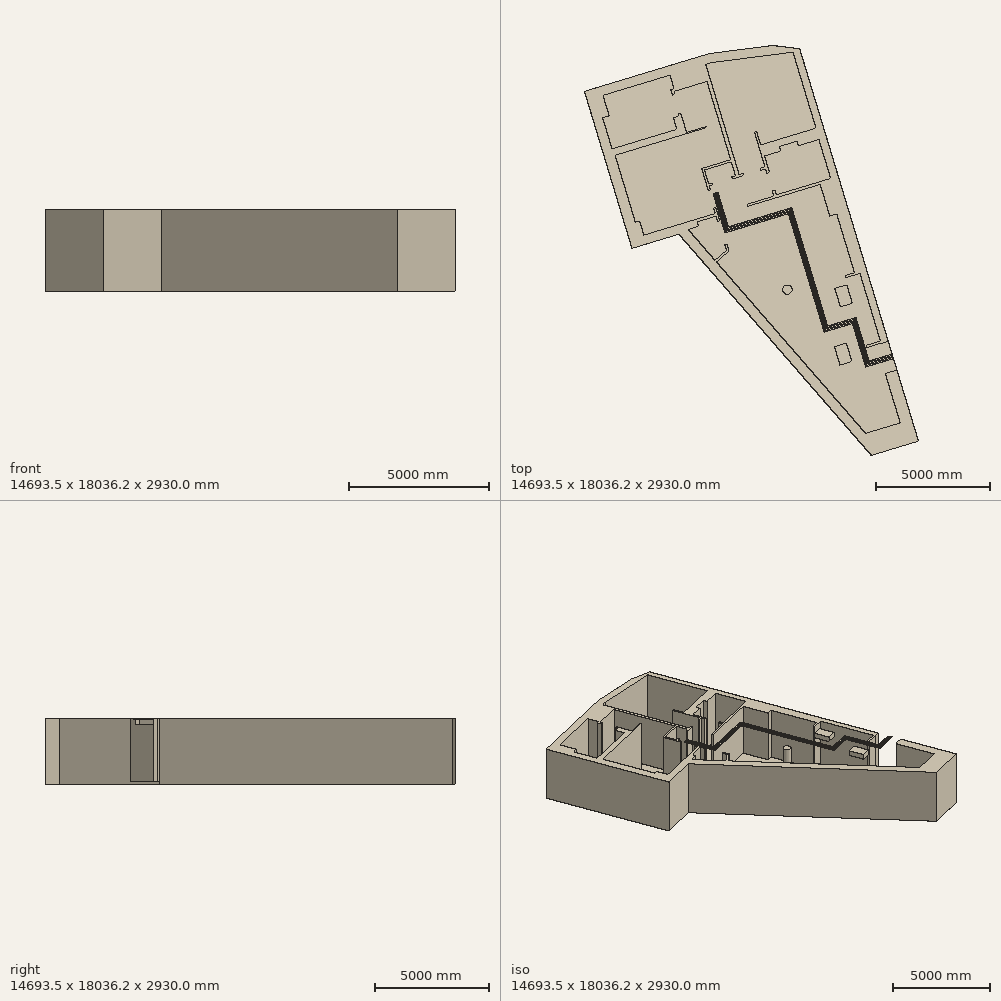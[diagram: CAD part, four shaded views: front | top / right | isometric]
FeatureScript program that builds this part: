
annotation { "Feature Type Name" : "Feature", "Feature Type Description" : "" }
export const myFeature = defineFeature(function(context is Context, id is Id, definition is map)
    precondition{}
    {
        {
            var Q0;
            Q0=qCreatedBy(makeId("Top.planeOp"),FACE);
            var sketch = newSketch(context, id + "F0", { "sketchPlane" : qUnion([Q0])});
            skLineSegment(sketch, "E0", {"start": v(688.47, 32038.93) * mm, "end": v(503.96, 32648.57) * mm});
            skLineSegment(sketch, "E1", {"start": v(503.96, 32648.57) * mm, "end": v(1685.98, 33006.34) * mm});
            skLineSegment(sketch, "E2", {"start": v(1685.98, 33006.34) * mm, "end": v(1870.5, 32396.71) * mm});
            skLineSegment(sketch, "E3", {"start": v(1870.5, 32396.71) * mm, "end": v(688.47, 32038.93) * mm});
            skLineSegment(sketch, "E4", {"start": v(975.28, 28670.43) * mm, "end": v(-209.3, 30031.2) * mm});
            skLineSegment(sketch, "E5", {"start": v(-209.3, 30031.2) * mm, "end": v(247, 30169.35) * mm});
            skLineSegment(sketch, "E6", {"start": v(247, 30169.35) * mm, "end": v(187.3, 30366.58) * mm});
            skLineSegment(sketch, "E7", {"start": v(187.3, 30366.58) * mm, "end": v(1017.23, 30617.78) * mm});
            skLineSegment(sketch, "E8", {"start": v(1017.23, 30617.78) * mm, "end": v(1474.96, 29105.4) * mm});
            skLineSegment(sketch, "E9", {"start": v(1474.96, 29105.4) * mm, "end": v(975.28, 28670.43) * mm});
            skLineSegment(sketch, "E10", {"start": v(2976.11, 33751) * mm, "end": v(2796.5, 34344.43) * mm});
            skLineSegment(sketch, "E11", {"start": v(2796.5, 34344.43) * mm, "end": v(5232.35, 35081.71) * mm});
            skLineSegment(sketch, "E12", {"start": v(5232.35, 35081.71) * mm, "end": v(5411.97, 34488.28) * mm});
            skLineSegment(sketch, "E13", {"start": v(5411.97, 34488.28) * mm, "end": v(2976.11, 33751) * mm});
            skLineSegment(sketch, "E14", {"start": v(1038.97, 28597.26) * mm, "end": v(1585.97, 29073.44) * mm});
            skLineSegment(sketch, "E15", {"start": v(1585.97, 29073.44) * mm, "end": v(1107.2, 30655.36) * mm});
            skLineSegment(sketch, "E16", {"start": v(1107.2, 30655.36) * mm, "end": v(5663.61, 32034.54) * mm});
            skLineSegment(sketch, "E17", {"start": v(5663.61, 32034.54) * mm, "end": v(6064.95, 30708.6) * mm});
            skLineSegment(sketch, "E18", {"start": v(6064.95, 30708.6) * mm, "end": v(6370.27, 30801.02) * mm});
            skLineSegment(sketch, "E19", {"start": v(6370.27, 30801.02) * mm, "end": v(7173.28, 28148.02) * mm});
            skLineSegment(sketch, "E20", {"start": v(7173.28, 28148.02) * mm, "end": v(2627.74, 26772.17) * mm});
            skLineSegment(sketch, "E21", {"start": v(2627.74, 26772.17) * mm, "end": v(1038.97, 28597.26) * mm});
            skLineSegment(sketch, "E22", {"start": v(7648.03, 21005.12) * mm, "end": v(9204.22, 21476.13) * mm});
            skLineSegment(sketch, "E23", {"start": v(9204.22, 21476.13) * mm, "end": v(8546.54, 23648.8) * mm});
            skLineSegment(sketch, "E24", {"start": v(8546.54, 23648.8) * mm, "end": v(8680.59, 23689.38) * mm});
            skLineSegment(sketch, "E25", {"start": v(8680.59, 23689.38) * mm, "end": v(8275.24, 25028.58) * mm});
            skLineSegment(sketch, "E26", {"start": v(8275.24, 25028.58) * mm, "end": v(7643.52, 24837.37) * mm});
            skLineSegment(sketch, "E27", {"start": v(7643.52, 24837.37) * mm, "end": v(7615.16, 24931.08) * mm});
            skLineSegment(sketch, "E28", {"start": v(7615.16, 24931.08) * mm, "end": v(8246.85, 25122.28) * mm});
            skLineSegment(sketch, "E29", {"start": v(8246.85, 25122.28) * mm, "end": v(7345.9, 28098.92) * mm});
            skLineSegment(sketch, "E30", {"start": v(7345.9, 28098.92) * mm, "end": v(6714.19, 27907.71) * mm});
            skLineSegment(sketch, "E31", {"start": v(6714.19, 27907.71) * mm, "end": v(6686.09, 28000.55) * mm});
            skLineSegment(sketch, "E32", {"start": v(6686.09, 28000.55) * mm, "end": v(2627.74, 26772.17) * mm});
            skLineSegment(sketch, "E33", {"start": v(2627.74, 26772.17) * mm, "end": v(7648.03, 21005.12) * mm});
            skLineSegment(sketch, "E34", {"start": v(1953.77, 32421.91) * mm, "end": v(484.9, 37274.77) * mm});
            skLineSegment(sketch, "E35", {"start": v(484.9, 37274.77) * mm, "end": v(817.35, 37375.45) * mm});
            skLineSegment(sketch, "E36", {"start": v(817.35, 37375.45) * mm, "end": v(4399.01, 37834.91) * mm});
            skLineSegment(sketch, "E37", {"start": v(4399.01, 37834.91) * mm, "end": v(5232.35, 35081.71) * mm});
            skLineSegment(sketch, "E38", {"start": v(5232.35, 35081.71) * mm, "end": v(2703.65, 34316.33) * mm});
            skLineSegment(sketch, "E39", {"start": v(2703.65, 34316.33) * mm, "end": v(3166, 32788.83) * mm});
            skLineSegment(sketch, "E40", {"start": v(3166, 32788.83) * mm, "end": v(1953.77, 32421.91) * mm});
            skLineSegment(sketch, "E41", {"start": v(-3492.5, 33275.5) * mm, "end": v(592.96, 34511.99) * mm});
            skLineSegment(sketch, "E42", {"start": v(592.96, 34511.99) * mm, "end": v(1074.07, 32922.48) * mm});
            skLineSegment(sketch, "E43", {"start": v(1074.07, 32922.48) * mm, "end": v(383.02, 32713.3) * mm});
            skLineSegment(sketch, "E44", {"start": v(383.02, 32713.3) * mm, "end": v(981.9, 30734.55) * mm});
            skLineSegment(sketch, "E45", {"start": v(981.9, 30734.55) * mm, "end": v(-2157.46, 29784.33) * mm});
            skLineSegment(sketch, "E46", {"start": v(-2157.46, 29784.33) * mm, "end": v(-2347.02, 30410.5) * mm});
            skLineSegment(sketch, "E47", {"start": v(-2347.02, 30410.5) * mm, "end": v(-2601.66, 30332.35) * mm});
            skLineSegment(sketch, "E48", {"start": v(-2601.66, 30332.35) * mm, "end": v(-3492.5, 33275.5) * mm});
            skLineSegment(sketch, "E49", {"start": v(-710, 34438.17) * mm, "end": v(-3559.9, 33575.84) * mm});
            skLineSegment(sketch, "E50", {"start": v(-3559.9, 33575.84) * mm, "end": v(-3973.74, 34943.1) * mm});
            skLineSegment(sketch, "E51", {"start": v(-3973.74, 34943.1) * mm, "end": v(-3685.65, 35030.3) * mm});
            skLineSegment(sketch, "E52", {"start": v(-3685.65, 35030.3) * mm, "end": v(-3957.95, 35930) * mm});
            skLineSegment(sketch, "E53", {"start": v(-3957.95, 35930) * mm, "end": v(-1009.44, 36822.46) * mm});
            skLineSegment(sketch, "E54", {"start": v(-1009.44, 36822.46) * mm, "end": v(-831.43, 36230.92) * mm});
            skLineSegment(sketch, "E55", {"start": v(-831.43, 36230.92) * mm, "end": v(-977.95, 36186.57) * mm});
            skLineSegment(sketch, "E56", {"start": v(-977.95, 36186.57) * mm, "end": v(-622.8, 35013.09) * mm});
            skLineSegment(sketch, "E57", {"start": v(-622.8, 35013.09) * mm, "end": v(-861.8, 34940.5) * mm});
            skLineSegment(sketch, "E58", {"start": v(-861.8, 34940.5) * mm, "end": v(-710, 34438.17) * mm});
            skLineSegment(sketch, "E59", {"start": v(1107.2, 30655.36) * mm, "end": v(2396.47, 31045.6) * mm});
            skLineSegment(sketch, "E60", {"start": v(2396.47, 31045.6) * mm, "end": v(2368.65, 31137.53) * mm});
            skLineSegment(sketch, "E61", {"start": v(2368.65, 31137.53) * mm, "end": v(3556.94, 31497.2) * mm});
            skLineSegment(sketch, "E62", {"start": v(3556.94, 31497.2) * mm, "end": v(3194.1, 32695.99) * mm});
            skLineSegment(sketch, "E63", {"start": v(3194.1, 32695.99) * mm, "end": v(716.57, 31946.1) * mm});
            skLineSegment(sketch, "E64", {"start": v(716.57, 31946.1) * mm, "end": v(1107.2, 30655.36) * mm});
            skLineSegment(sketch, "E65", {"start": v(-828.96, 36106.8) * mm, "end": v(-267.45, 34251.56) * mm});
            skLineSegment(sketch, "E66", {"start": v(-267.45, 34251.56) * mm, "end": v(583.39, 34509.09) * mm});
            skLineSegment(sketch, "E67", {"start": v(583.39, 34509.09) * mm, "end": v(1064.5, 32919.58) * mm});
            skLineSegment(sketch, "E68", {"start": v(1064.5, 32919.58) * mm, "end": v(1657.88, 33099.18) * mm});
            skLineSegment(sketch, "E69", {"start": v(1657.88, 33099.18) * mm, "end": v(615.22, 36543.93) * mm});
            skLineSegment(sketch, "E70", {"start": v(615.22, 36543.93) * mm, "end": v(-828.96, 36106.8) * mm});
            skLineSegment(sketch, "E71", {"start": v(2521, 36867.94) * mm, "end": v(2477.55, 37011.51) * mm});
            skLineSegment(sketch, "E72", {"start": v(2477.55, 37011.51) * mm, "end": v(2621.12, 37054.97) * mm});
            skLineSegment(sketch, "E73", {"start": v(2621.12, 37054.97) * mm, "end": v(2664.57, 36911.4) * mm});
            skLineSegment(sketch, "E74", {"start": v(2664.57, 36911.4) * mm, "end": v(2521, 36867.94) * mm});
            skCircle(sketch, "E75", {"center": v(2571.06, 36961.45) * mm, "radius": 75 * mm});
            skLineSegment(sketch, "E76", {"start": v(6682.01, 27897.97) * mm, "end": v(2720.36, 26698.86) * mm});
            skLineSegment(sketch, "E77", {"start": v(2845.75, 34181.7) * mm, "end": v(5281.61, 34918.98) * mm});
            skLineSegment(sketch, "E78", {"start": v(6128.04, 25871.52) * mm, "end": v(6340.42, 26268.26) * mm});
            skCircle(sketch, "E79", {"center": v(6234.23, 26069.9) * mm, "radius": 225 * mm});
            skCircle(sketch, "E80", {"center": v(-1847.03, 34397.83) * mm, "radius": 70 * mm});
            skCircle(sketch, "E81", {"center": v(-1031.48, 34644.68) * mm, "radius": 70 * mm});
            skCircle(sketch, "E82", {"center": v(-2662.4, 34151.03) * mm, "radius": 70 * mm});
            skCircle(sketch, "E83", {"center": v(-3282.71, 33963.28) * mm, "radius": 70 * mm});
            skCircle(sketch, "E84", {"center": v(1346.97, 36590.95) * mm, "radius": 70 * mm});
            skCircle(sketch, "E85", {"center": v(1919, 34705.78) * mm, "radius": 70 * mm});
            skCircle(sketch, "E86", {"center": v(4106.18, 35367.8) * mm, "radius": 70 * mm});
            skCircle(sketch, "E87", {"center": v(4291.3, 37482.1) * mm, "radius": 24.96 * mm});
            skCircle(sketch, "E88", {"center": v(4291.3, 37482.1) * mm, "radius": 89.6 * mm});
            skCircle(sketch, "E89", {"center": v(3702.85, 29215.68) * mm, "radius": 50 * mm});
            skLineSegment(sketch, "E90", {"start": v(3774.64, 29237.4) * mm, "end": v(3631.07, 29193.95) * mm});
            skLineSegment(sketch, "E91", {"start": v(3681.12, 29287.46) * mm, "end": v(3724.58, 29143.9) * mm});
            skLineSegment(sketch, "E92", {"start": v(4947.02, 28251.96) * mm, "end": v(4903.56, 28395.53) * mm});
            skLineSegment(sketch, "E93", {"start": v(4903.56, 28395.53) * mm, "end": v(5047.13, 28438.98) * mm});
            skLineSegment(sketch, "E94", {"start": v(5047.13, 28438.98) * mm, "end": v(5090.59, 28295.41) * mm});
            skLineSegment(sketch, "E95", {"start": v(5090.59, 28295.41) * mm, "end": v(4947.02, 28251.96) * mm});
            skCircle(sketch, "E96", {"center": v(4997.08, 28345.47) * mm, "radius": 75 * mm});
            skCircle(sketch, "E97", {"center": v(4647.16, 29501.5) * mm, "radius": 50 * mm});
            skCircle(sketch, "E98", {"center": v(4647.16, 29501.5) * mm, "radius": 185.02 * mm});
            skCircle(sketch, "E99", {"center": v(5731.95, 25917.86) * mm, "radius": 50 * mm});
            skCircle(sketch, "E100", {"center": v(5731.95, 25917.86) * mm, "radius": 185.02 * mm});
            skCircle(sketch, "E101", {"center": v(-1220.67, 35372.03) * mm, "radius": 23.22 * mm});
            skCircle(sketch, "E102", {"center": v(-3689, 35802.45) * mm, "radius": 52 * mm});
            skCircle(sketch, "E103", {"center": v(2856.43, 36018.65) * mm, "radius": 50 * mm});
            skLineSegment(sketch, "E104", {"start": v(2928.21, 36040.38) * mm, "end": v(2784.64, 35996.93) * mm});
            skLineSegment(sketch, "E105", {"start": v(2834.7, 36090.44) * mm, "end": v(2878.16, 35946.87) * mm});
            skCircle(sketch, "E106", {"center": v(2789.14, 31831.37) * mm, "radius": 70 * mm});
            skCircle(sketch, "E107", {"center": v(2325.79, 33360.78) * mm, "radius": 70 * mm});
            skCircle(sketch, "E108", {"center": v(-3089.6, 33189.85) * mm, "radius": 24.96 * mm});
            skCircle(sketch, "E109", {"center": v(-3089.61, 33189.85) * mm, "radius": 89.6 * mm});
            skCircle(sketch, "E110", {"center": v(-694.3, 33908.01) * mm, "radius": 24.96 * mm});
            skCircle(sketch, "E111", {"center": v(-694.3, 33908.01) * mm, "radius": 89.6 * mm});
            skCircle(sketch, "E112", {"center": v(5238.28, 31100.14) * mm, "radius": 70 * mm});
            skCircle(sketch, "E113", {"center": v(-2823.66, 32311.65) * mm, "radius": 70 * mm});
            skLineSegment(sketch, "E114", {"start": v(-1847.07, 31588.32) * mm, "end": v(-1803.62, 31444.75) * mm});
            skLineSegment(sketch, "E115", {"start": v(-1803.62, 31444.75) * mm, "end": v(-1947.18, 31401.3) * mm});
            skLineSegment(sketch, "E116", {"start": v(-1947.18, 31401.3) * mm, "end": v(-1990.64, 31544.87) * mm});
            skLineSegment(sketch, "E117", {"start": v(-1990.64, 31544.87) * mm, "end": v(-1847.07, 31588.32) * mm});
            skCircle(sketch, "E118", {"center": v(-1897.13, 31494.81) * mm, "radius": 75 * mm});
            skLineSegment(sketch, "E119", {"start": v(-798.77, 31748.9) * mm, "end": v(-842.22, 31892.47) * mm});
            skLineSegment(sketch, "E120", {"start": v(-842.22, 31892.47) * mm, "end": v(-698.66, 31935.92) * mm});
            skLineSegment(sketch, "E121", {"start": v(-698.66, 31935.92) * mm, "end": v(-655.2, 31792.36) * mm});
            skLineSegment(sketch, "E122", {"start": v(-655.2, 31792.36) * mm, "end": v(-798.77, 31748.9) * mm});
            skCircle(sketch, "E123", {"center": v(-748.71, 31842.41) * mm, "radius": 75 * mm});
            skCircle(sketch, "E124", {"center": v(-1322.96, 31668.6) * mm, "radius": 50 * mm});
            skLineSegment(sketch, "E125", {"start": v(-1251.18, 31690.33) * mm, "end": v(-1394.75, 31646.87) * mm});
            skLineSegment(sketch, "E126", {"start": v(-1344.7, 31740.38) * mm, "end": v(-1301.24, 31596.82) * mm});
            skCircle(sketch, "E127", {"center": v(1916.85, 30094.8) * mm, "radius": 70 * mm});
            skLineSegment(sketch, "E128", {"start": v(5408.3, 27246.02) * mm, "end": v(5451.75, 27102.45) * mm});
            skLineSegment(sketch, "E129", {"start": v(5451.75, 27102.45) * mm, "end": v(5308.19, 27059) * mm});
            skLineSegment(sketch, "E130", {"start": v(5308.19, 27059) * mm, "end": v(5264.73, 27202.57) * mm});
            skLineSegment(sketch, "E131", {"start": v(5264.73, 27202.57) * mm, "end": v(5408.3, 27246.02) * mm});
            skCircle(sketch, "E132", {"center": v(5358.24, 27152.51) * mm, "radius": 75 * mm});
            skCircle(sketch, "E133", {"center": v(7896.13, 22311.4) * mm, "radius": 50 * mm});
            skLineSegment(sketch, "E134", {"start": v(7967.91, 22333.12) * mm, "end": v(7824.34, 22289.67) * mm});
            skLineSegment(sketch, "E135", {"start": v(7874.4, 22383.18) * mm, "end": v(7917.86, 22239.6) * mm});
            skLineSegment(sketch, "E136", {"start": v(7346.13, 23869.61) * mm, "end": v(7302.67, 24013.18) * mm});
            skLineSegment(sketch, "E137", {"start": v(7302.67, 24013.18) * mm, "end": v(7446.24, 24056.63) * mm});
            skLineSegment(sketch, "E138", {"start": v(7446.24, 24056.63) * mm, "end": v(7489.7, 23913.07) * mm});
            skLineSegment(sketch, "E139", {"start": v(7489.7, 23913.07) * mm, "end": v(7346.13, 23869.61) * mm});
            skCircle(sketch, "E140", {"center": v(7396.18, 23963.12) * mm, "radius": 75 * mm});
            skCircle(sketch, "E141", {"center": v(7193.06, 26360.11) * mm, "radius": 50 * mm});
            skLineSegment(sketch, "E142", {"start": v(7240.92, 26374.6) * mm, "end": v(7514.25, 26457.33) * mm});
            skLineSegment(sketch, "E143", {"start": v(7365.6, 26307.86) * mm, "end": v(7240.92, 26374.6) * mm});
            skLineSegment(sketch, "E144", {"start": v(7240.92, 26374.6) * mm, "end": v(7307.66, 26499.27) * mm});
            skLineSegment(sketch, "E145", {"start": v(7307.66, 26499.27) * mm, "end": v(7365.6, 26307.86) * mm});
            skLineSegment(sketch, "E146", {"start": v(575.66, 33236.57) * mm, "end": v(546.8, 33331.8) * mm});
            skLineSegment(sketch, "E147", {"start": v(546.8, 33331.8) * mm, "end": v(655.88, 33364.87) * mm});
            skLineSegment(sketch, "E148", {"start": v(655.88, 33364.87) * mm, "end": v(684.75, 33269.65) * mm});
            skLineSegment(sketch, "E149", {"start": v(684.75, 33269.65) * mm, "end": v(575.66, 33236.57) * mm});
            skLineSegment(sketch, "E150", {"start": v(546.79, 33331.8) * mm, "end": v(517.92, 33427.01) * mm});
            skLineSegment(sketch, "E151", {"start": v(517.92, 33427.01) * mm, "end": v(627.01, 33460.09) * mm});
            skLineSegment(sketch, "E152", {"start": v(627.01, 33460.09) * mm, "end": v(655.88, 33364.87) * mm});
            skLineSegment(sketch, "E153", {"start": v(655.88, 33364.87) * mm, "end": v(546.79, 33331.8) * mm});
            skLineSegment(sketch, "E154", {"start": v(3585.52, 37346.87) * mm, "end": v(3628.97, 37203.3) * mm});
            skLineSegment(sketch, "E155", {"start": v(3628.97, 37203.3) * mm, "end": v(3485.4, 37159.85) * mm});
            skLineSegment(sketch, "E156", {"start": v(3485.4, 37159.85) * mm, "end": v(3441.95, 37303.42) * mm});
            skLineSegment(sketch, "E157", {"start": v(3441.95, 37303.42) * mm, "end": v(3585.52, 37346.87) * mm});
            skCircle(sketch, "E158", {"center": v(3535.46, 37253.36) * mm, "radius": 75 * mm});
            skLineSegment(sketch, "E159", {"start": v(-4301.45, 33405.9) * mm, "end": v(-4393.43, 33709.79) * mm});
            skEllipse(sketch, "E160", {"center": v(-4253.27, 33246.73) * mm, "majorRadius": 182.04 * mm, "minorRadius": 182.04 * mm, "majorAxis": v(0.7, 0.7)});
            skLineSegment(sketch, "E161", {"start": v(-4393.43, 33709.79) * mm, "end": v(-3952.33, 34533.82) * mm});
            skLineSegment(sketch, "E162", {"start": v(-4064.75, 34413.93) * mm, "end": v(-3952.33, 34533.82) * mm});
            skLineSegment(sketch, "E163", {"start": v(-3952.33, 34533.82) * mm, "end": v(-3989.74, 34373.78) * mm});
            skLineSegment(sketch, "E164", {"start": v(-3989.74, 34373.78) * mm, "end": v(-4064.75, 34413.93) * mm});
            skLineSegment(sketch, "E165", {"start": v(-3654.18, 34799.3) * mm, "end": v(-3257.44, 34586.93) * mm});
            skCircle(sketch, "E166", {"center": v(-3455.8, 34693.11) * mm, "radius": 225 * mm});
            skLineSegment(sketch, "E167", {"start": v(-2284.17, 37866.22) * mm, "end": v(-2192.19, 37562.34) * mm});
            skEllipse(sketch, "E168", {"center": v(-2332.35, 38025.4) * mm, "majorRadius": 182.04 * mm, "minorRadius": 182.04 * mm, "majorAxis": v(1, 0)});
            skLineSegment(sketch, "E169", {"start": v(-2192.19, 37562.34) * mm, "end": v(-2055.36, 37110.28) * mm});
            skLineSegment(sketch, "E170", {"start": v(-2060.64, 37274.55) * mm, "end": v(-2055.36, 37110.28) * mm});
            skLineSegment(sketch, "E171", {"start": v(-2055.36, 37110.28) * mm, "end": v(-2142.06, 37249.9) * mm});
            skLineSegment(sketch, "E172", {"start": v(-2142.06, 37249.9) * mm, "end": v(-2060.64, 37274.55) * mm});
            skLineSegment(sketch, "E173", {"start": v(6324.7, 31290.66) * mm, "end": v(6411.61, 31003.53) * mm});
            skLineSegment(sketch, "E174", {"start": v(6411.61, 31003.53) * mm, "end": v(6124.47, 30916.62) * mm});
            skLineSegment(sketch, "E175", {"start": v(6124.47, 30916.62) * mm, "end": v(6037.56, 31203.75) * mm});
            skLineSegment(sketch, "E176", {"start": v(6037.56, 31203.75) * mm, "end": v(6324.7, 31290.66) * mm});
            skLineSegment(sketch, "E177", {"start": v(6324.7, 31290.66) * mm, "end": v(6124.47, 30916.62) * mm});
            skCircle(sketch, "E178", {"center": v(-3095.59, 35982.06) * mm, "radius": 52 * mm});
            skCircle(sketch, "E179", {"center": v(-2502.17, 36161.68) * mm, "radius": 52 * mm});
            skCircle(sketch, "E180", {"center": v(-1908.76, 36341.3) * mm, "radius": 52 * mm});
            skCircle(sketch, "E181", {"center": v(-1315.35, 36520.9) * mm, "radius": 52 * mm});
            skCircle(sketch, "E182", {"center": v(2532.3, 27643.33) * mm, "radius": 70 * mm});
            skCircle(sketch, "E183", {"center": v(1875.7, 28397.58) * mm, "radius": 70 * mm});
            skLineSegment(sketch, "E184", {"start": v(1609.88, 32773.32) * mm, "end": v(1696.79, 32486.2) * mm});
            skLineSegment(sketch, "E185", {"start": v(1696.79, 32486.2) * mm, "end": v(1409.64, 32399.28) * mm});
            skLineSegment(sketch, "E186", {"start": v(1409.64, 32399.28) * mm, "end": v(1322.74, 32686.4) * mm});
            skLineSegment(sketch, "E187", {"start": v(1322.74, 32686.4) * mm, "end": v(1609.88, 32773.32) * mm});
            skLineSegment(sketch, "E188", {"start": v(1609.88, 32773.32) * mm, "end": v(1409.64, 32399.28) * mm});
            skCircle(sketch, "E189", {"center": v(6011.32, 23646.8) * mm, "radius": 70 * mm});
            skCircle(sketch, "E190", {"center": v(3459.78, 26577.88) * mm, "radius": 70 * mm});
            skCircle(sketch, "E191", {"center": v(8590.03, 22521.42) * mm, "radius": 70 * mm});
            skCircle(sketch, "E192", {"center": v(6714.5, 26215.26) * mm, "radius": 70 * mm});
            skCircle(sketch, "E193", {"center": v(7043.04, 25129.83) * mm, "radius": 70 * mm});
            skCircle(sketch, "E194", {"center": v(4413.86, 26866.66) * mm, "radius": 50 * mm});
            skLineSegment(sketch, "E195", {"start": v(4485.64, 26888.4) * mm, "end": v(4342.07, 26844.94) * mm});
            skLineSegment(sketch, "E196", {"start": v(4392.13, 26938.45) * mm, "end": v(4435.58, 26794.88) * mm});
            skCircle(sketch, "E197", {"center": v(5979.71, 28642.9) * mm, "radius": 70 * mm});
            skLineSegment(sketch, "E198", {"start": v(1029.24, 34682.5) * mm, "end": v(1116.14, 34395.38) * mm});
            skLineSegment(sketch, "E199", {"start": v(1116.14, 34395.38) * mm, "end": v(829, 34308.46) * mm});
            skLineSegment(sketch, "E200", {"start": v(829, 34308.46) * mm, "end": v(742.1, 34595.59) * mm});
            skLineSegment(sketch, "E201", {"start": v(742.1, 34595.59) * mm, "end": v(1029.24, 34682.5) * mm});
            skLineSegment(sketch, "E202", {"start": v(1029.24, 34682.5) * mm, "end": v(829, 34308.46) * mm});
            skLineSegment(sketch, "E203", {"start": v(3855.94, 24986.4) * mm, "end": v(3968.37, 25106.3) * mm});
            skLineSegment(sketch, "E204", {"start": v(3968.37, 25106.3) * mm, "end": v(3930.95, 24946.26) * mm});
            skLineSegment(sketch, "E205", {"start": v(3930.95, 24946.26) * mm, "end": v(3855.94, 24986.4) * mm});
            skLineSegment(sketch, "E206", {"start": v(6167.02, 21051.64) * mm, "end": v(6075.04, 21355.52) * mm});
            skEllipse(sketch, "E207", {"center": v(6215.2, 20892.46) * mm, "majorRadius": 182.04 * mm, "minorRadius": 182.04 * mm, "majorAxis": v(0.7, 0.7)});
            skLineSegment(sketch, "E208", {"start": v(6075.04, 21355.52) * mm, "end": v(6516.14, 22179.55) * mm});
            skLineSegment(sketch, "E209", {"start": v(6403.72, 22059.66) * mm, "end": v(6516.14, 22179.55) * mm});
            skLineSegment(sketch, "E210", {"start": v(6516.14, 22179.55) * mm, "end": v(6478.72, 22019.51) * mm});
            skLineSegment(sketch, "E211", {"start": v(6478.72, 22019.51) * mm, "end": v(6403.72, 22059.66) * mm});
            skLineSegment(sketch, "E212", {"start": v(-3715.4, 37697.94) * mm, "end": v(-2680.13, 36361.95) * mm});
            skLineSegment(sketch, "E213", {"start": v(-2743.75, 36513.49) * mm, "end": v(-2680.13, 36361.95) * mm});
            skLineSegment(sketch, "E214", {"start": v(-2680.13, 36361.95) * mm, "end": v(-2811, 36461.38) * mm});
            skLineSegment(sketch, "E215", {"start": v(-2811, 36461.38) * mm, "end": v(-2743.75, 36513.49) * mm});
            skLineSegment(sketch, "E216", {"start": v(6668.7, 25183.66) * mm, "end": v(6456.33, 24786.93) * mm});
            skCircle(sketch, "E217", {"center": v(6562.52, 24985.3) * mm, "radius": 225 * mm});
            skCircle(sketch, "E218", {"center": v(860.2, 30103.67) * mm, "radius": 50 * mm});
            skLineSegment(sketch, "E219", {"start": v(908.05, 30118.16) * mm, "end": v(1181.38, 30200.89) * mm});
            skLineSegment(sketch, "E220", {"start": v(1032.72, 30051.42) * mm, "end": v(908.05, 30118.16) * mm});
            skLineSegment(sketch, "E221", {"start": v(908.05, 30118.16) * mm, "end": v(974.79, 30242.83) * mm});
            skLineSegment(sketch, "E222", {"start": v(974.79, 30242.83) * mm, "end": v(1032.72, 30051.42) * mm});
            skLineSegment(sketch, "E223", {"start": v(3665, 31553.41) * mm, "end": v(3146.69, 33265.8) * mm});
            skLineSegment(sketch, "E224", {"start": v(3146.69, 33265.8) * mm, "end": v(3864.66, 33483.1) * mm});
            skLineSegment(sketch, "E225", {"start": v(3864.66, 33483.1) * mm, "end": v(3803.84, 33684.03) * mm});
            skLineSegment(sketch, "E226", {"start": v(3803.84, 33684.03) * mm, "end": v(4569.53, 33915.8) * mm});
            skLineSegment(sketch, "E227", {"start": v(4569.53, 33915.8) * mm, "end": v(4630.34, 33714.9) * mm});
            skLineSegment(sketch, "E228", {"start": v(4630.34, 33714.9) * mm, "end": v(5539.28, 33990.02) * mm});
            skLineSegment(sketch, "E229", {"start": v(5539.28, 33990.02) * mm, "end": v(6057.79, 32277.66) * mm});
            skLineSegment(sketch, "E230", {"start": v(6057.79, 32277.66) * mm, "end": v(3665, 31553.41) * mm});
            skCircle(sketch, "E231", {"center": v(3988.93, 33314.17) * mm, "radius": 70 * mm});
            skCircle(sketch, "E232", {"center": v(5732.52, 32722.3) * mm, "radius": 52 * mm});
            skCircle(sketch, "E233", {"center": v(5479.1, 33559.56) * mm, "radius": 52 * mm});
            skCircle(sketch, "E234", {"center": v(3586.94, 33192.5) * mm, "radius": 70 * mm});
            skCircle(sketch, "E235", {"center": v(5058.95, 32518.43) * mm, "radius": 50 * mm});
            skLineSegment(sketch, "E236", {"start": v(5035.58, 32474.22) * mm, "end": v(4902.1, 32221.76) * mm});
            skLineSegment(sketch, "E237", {"start": v(4900.44, 32432.56) * mm, "end": v(5035.58, 32474.22) * mm});
            skLineSegment(sketch, "E238", {"start": v(5035.58, 32474.22) * mm, "end": v(5077.24, 32339.09) * mm});
            skLineSegment(sketch, "E239", {"start": v(5077.24, 32339.09) * mm, "end": v(4900.44, 32432.56) * mm});
            skCircle(sketch, "E240", {"center": v(3482.78, 32663.76) * mm, "radius": 23.22 * mm});
            skLineSegment(sketch, "E241", {"start": v(1963.34, 32424.81) * mm, "end": v(494.48, 37277.66) * mm});
            skLineSegment(sketch, "E242", {"start": v(494.48, 37277.66) * mm, "end": v(561.48, 37297.94) * mm});
            skLineSegment(sketch, "E243", {"start": v(561.48, 37297.94) * mm, "end": v(2030.34, 32445.09) * mm});
            skLineSegment(sketch, "E244", {"start": v(2030.34, 32445.09) * mm, "end": v(1963.34, 32424.81) * mm});
            skLineSegment(sketch, "E245", {"start": v(-3492.5, 33275.5) * mm, "end": v(-3425.5, 33295.77) * mm});
            skLineSegment(sketch, "E246", {"start": v(-3425.5, 33295.77) * mm, "end": v(-2534.67, 30352.63) * mm});
            skLineSegment(sketch, "E247", {"start": v(-2534.67, 30352.63) * mm, "end": v(-2601.66, 30332.35) * mm});
            skLineSegment(sketch, "E248", {"start": v(7627.75, 21072.12) * mm, "end": v(9116.94, 21522.85) * mm});
            skLineSegment(sketch, "E249", {"start": v(9116.94, 21522.85) * mm, "end": v(8459.27, 23695.52) * mm});
            skLineSegment(sketch, "E250", {"start": v(8459.27, 23695.52) * mm, "end": v(8660.3, 23756.37) * mm});
            skLineSegment(sketch, "E251", {"start": v(8660.3, 23756.37) * mm, "end": v(8680.59, 23689.38) * mm});
            skLineSegment(sketch, "E252", {"start": v(8680.59, 23689.38) * mm, "end": v(8546.54, 23648.8) * mm});
            skLineSegment(sketch, "E253", {"start": v(8546.54, 23648.8) * mm, "end": v(9204.22, 21476.13) * mm});
            skLineSegment(sketch, "E254", {"start": v(9204.22, 21476.13) * mm, "end": v(7648.03, 21005.12) * mm});
            skLineSegment(sketch, "E255", {"start": v(7648.03, 21005.12) * mm, "end": v(7627.75, 21072.12) * mm});
            skLineSegment(sketch, "E256", {"start": v(7173.28, 28148.02) * mm, "end": v(7106.28, 28127.74) * mm});
            skLineSegment(sketch, "E257", {"start": v(7106.28, 28127.74) * mm, "end": v(6323.55, 30713.74) * mm});
            skLineSegment(sketch, "E258", {"start": v(6323.55, 30713.74) * mm, "end": v(6018.23, 30621.33) * mm});
            skLineSegment(sketch, "E259", {"start": v(6018.23, 30621.33) * mm, "end": v(5596.86, 32013.45) * mm});
            skLineSegment(sketch, "E260", {"start": v(5596.86, 32013.45) * mm, "end": v(5663.86, 32033.73) * mm});
            skLineSegment(sketch, "E261", {"start": v(5663.86, 32033.73) * mm, "end": v(6064.95, 30708.6) * mm});
            skLineSegment(sketch, "E262", {"start": v(-6.74, 35160.65) * mm, "end": v(-35.61, 35255.87) * mm});
            skLineSegment(sketch, "E263", {"start": v(-35.61, 35255.87) * mm, "end": v(73.48, 35288.95) * mm});
            skLineSegment(sketch, "E264", {"start": v(73.48, 35288.95) * mm, "end": v(102.35, 35193.73) * mm});
            skLineSegment(sketch, "E265", {"start": v(102.35, 35193.73) * mm, "end": v(-6.74, 35160.65) * mm});
            skLineSegment(sketch, "E266", {"start": v(-35.61, 35255.87) * mm, "end": v(-64.48, 35351.09) * mm});
            skLineSegment(sketch, "E267", {"start": v(-64.48, 35351.09) * mm, "end": v(44.6, 35384.16) * mm});
            skLineSegment(sketch, "E268", {"start": v(44.6, 35384.16) * mm, "end": v(73.48, 35288.95) * mm});
            skLineSegment(sketch, "E269", {"start": v(73.48, 35288.95) * mm, "end": v(-35.61, 35255.87) * mm});
            skLineSegment(sketch, "E270", {"start": v(-281.93, 34299.42) * mm, "end": v(578.47, 34559.84) * mm});
            skLineSegment(sketch, "E271", {"start": v(8380.43, 21227.85) * mm, "end": v(8462.74, 21252.76) * mm});
            skArc(sketch, "E272", {"start": v(8462.74, 21252.76) * mm, "mid": v(8409.13, 21281.46) * mm, "end": v(8380.43, 21227.85) * mm});
            skLineSegment(sketch, "E273", {"start": v(8421.58, 21240.3) * mm, "end": v(8392.62, 21336.02) * mm});
            skLineSegment(sketch, "E274", {"start": v(8462.74, 21252.76) * mm, "end": v(8380.43, 21227.85) * mm});
            skLineSegment(sketch, "E275", {"start": v(8380.43, 21227.85) * mm, "end": v(8377.53, 21237.42) * mm});
            skLineSegment(sketch, "E276", {"start": v(8377.53, 21237.42) * mm, "end": v(8459.84, 21262.33) * mm});
            skLineSegment(sketch, "E277", {"start": v(8459.84, 21262.33) * mm, "end": v(8462.74, 21252.76) * mm});
            skCircle(sketch, "E278", {"center": v(6340.55, 27450.74) * mm, "radius": 70 * mm});
            skCircle(sketch, "E279", {"center": v(8090.05, 24173.16) * mm, "radius": 70 * mm});
            skCircle(sketch, "E280", {"center": v(4698.2, 25155.24) * mm, "radius": 70 * mm});
            skLineSegment(sketch, "E281", {"start": v(1306.25, 28829.94) * mm, "end": v(1241.38, 28773.47) * mm});
            skArc(sketch, "E282", {"start": v(1241.38, 28773.47) * mm, "mid": v(1302.05, 28769.27) * mm, "end": v(1306.25, 28829.94) * mm});
            skLineSegment(sketch, "E283", {"start": v(1273.82, 28801.7) * mm, "end": v(1339.47, 28726.28) * mm});
            skLineSegment(sketch, "E284", {"start": v(1241.38, 28773.47) * mm, "end": v(1306.25, 28829.94) * mm});
            skLineSegment(sketch, "E285", {"start": v(1306.25, 28829.94) * mm, "end": v(1312.81, 28822.4) * mm});
            skLineSegment(sketch, "E286", {"start": v(1312.81, 28822.4) * mm, "end": v(1247.95, 28765.93) * mm});
            skLineSegment(sketch, "E287", {"start": v(1247.95, 28765.93) * mm, "end": v(1241.38, 28773.47) * mm});
            skCircle(sketch, "E288", {"center": v(5629.8, 29798.92) * mm, "radius": 70 * mm});
            skLineSegment(sketch, "E289", {"start": v(6948.35, 28891.15) * mm, "end": v(6923.43, 28973.47) * mm});
            skArc(sketch, "E290", {"start": v(6923.43, 28973.47) * mm, "mid": v(6894.73, 28919.85) * mm, "end": v(6948.35, 28891.15) * mm});
            skLineSegment(sketch, "E291", {"start": v(6935.9, 28932.31) * mm, "end": v(6840.18, 28903.34) * mm});
            skLineSegment(sketch, "E292", {"start": v(6923.43, 28973.47) * mm, "end": v(6948.35, 28891.15) * mm});
            skLineSegment(sketch, "E293", {"start": v(6948.35, 28891.15) * mm, "end": v(6938.78, 28888.26) * mm});
            skLineSegment(sketch, "E294", {"start": v(6938.78, 28888.26) * mm, "end": v(6913.86, 28970.57) * mm});
            skLineSegment(sketch, "E295", {"start": v(6913.86, 28970.57) * mm, "end": v(6923.43, 28973.47) * mm});
            skCircle(sketch, "E296", {"center": v(1508.54, 31443.79) * mm, "radius": 70 * mm});
            skLineSegment(sketch, "E297", {"start": v(-746.1, 30211.52) * mm, "end": v(-663.8, 30236.44) * mm});
            skArc(sketch, "E298", {"start": v(-663.8, 30236.44) * mm, "mid": v(-717.4, 30265.14) * mm, "end": v(-746.1, 30211.52) * mm});
            skLineSegment(sketch, "E299", {"start": v(-704.95, 30223.98) * mm, "end": v(-733.92, 30319.7) * mm});
            skLineSegment(sketch, "E300", {"start": v(-663.8, 30236.44) * mm, "end": v(-746.1, 30211.52) * mm});
            skLineSegment(sketch, "E301", {"start": v(-746.1, 30211.52) * mm, "end": v(-749, 30221.1) * mm});
            skLineSegment(sketch, "E302", {"start": v(-749, 30221.1) * mm, "end": v(-666.69, 30246) * mm});
            skLineSegment(sketch, "E303", {"start": v(-666.69, 30246) * mm, "end": v(-663.8, 30236.44) * mm});
            skLineSegment(sketch, "E304", {"start": v(-2321.17, 30329.54) * mm, "end": v(-2296.26, 30247.23) * mm});
            skArc(sketch, "E305", {"start": v(-2296.26, 30247.23) * mm, "mid": v(-2267.56, 30300.84) * mm, "end": v(-2321.17, 30329.54) * mm});
            skLineSegment(sketch, "E306", {"start": v(-2308.72, 30288.38) * mm, "end": v(-2213, 30317.35) * mm});
            skLineSegment(sketch, "E307", {"start": v(-2296.26, 30247.23) * mm, "end": v(-2321.17, 30329.54) * mm});
            skLineSegment(sketch, "E308", {"start": v(-2321.17, 30329.54) * mm, "end": v(-2311.6, 30332.44) * mm});
            skLineSegment(sketch, "E309", {"start": v(-2311.6, 30332.44) * mm, "end": v(-2286.69, 30250.12) * mm});
            skLineSegment(sketch, "E310", {"start": v(-2286.69, 30250.12) * mm, "end": v(-2296.26, 30247.23) * mm});
            skCircle(sketch, "E311", {"center": v(-2520.05, 31308.13) * mm, "radius": 70 * mm});
            skCircle(sketch, "E312", {"center": v(174.15, 31038.83) * mm, "radius": 70 * mm});
            skLineSegment(sketch, "E313", {"start": v(-3106, 33392.47) * mm, "end": v(-3188.32, 33367.55) * mm});
            skArc(sketch, "E314", {"start": v(-3188.32, 33367.55) * mm, "mid": v(-3134.7, 33338.85) * mm, "end": v(-3106, 33392.47) * mm});
            skLineSegment(sketch, "E315", {"start": v(-3147.16, 33380) * mm, "end": v(-3118.2, 33284.3) * mm});
            skLineSegment(sketch, "E316", {"start": v(-3188.32, 33367.55) * mm, "end": v(-3106, 33392.47) * mm});
            skLineSegment(sketch, "E317", {"start": v(-3106, 33392.47) * mm, "end": v(-3103.11, 33382.9) * mm});
            skLineSegment(sketch, "E318", {"start": v(-3103.11, 33382.9) * mm, "end": v(-3185.42, 33357.98) * mm});
            skLineSegment(sketch, "E319", {"start": v(-3185.42, 33357.98) * mm, "end": v(-3188.32, 33367.55) * mm});
            skLineSegment(sketch, "E320", {"start": v(-712.6, 34116.9) * mm, "end": v(-794.9, 34092) * mm});
            skArc(sketch, "E321", {"start": v(-794.9, 34092) * mm, "mid": v(-741.29, 34063.3) * mm, "end": v(-712.6, 34116.9) * mm});
            skLineSegment(sketch, "E322", {"start": v(-753.75, 34104.45) * mm, "end": v(-724.78, 34008.74) * mm});
            skLineSegment(sketch, "E323", {"start": v(-794.9, 34092) * mm, "end": v(-712.6, 34116.9) * mm});
            skLineSegment(sketch, "E324", {"start": v(-712.6, 34116.9) * mm, "end": v(-709.7, 34107.33) * mm});
            skLineSegment(sketch, "E325", {"start": v(-709.7, 34107.33) * mm, "end": v(-792, 34082.42) * mm});
            skLineSegment(sketch, "E326", {"start": v(-792, 34082.42) * mm, "end": v(-794.9, 34092) * mm});
            skLineSegment(sketch, "E327", {"start": v(4535.84, 37382.88) * mm, "end": v(4510.92, 37465.2) * mm});
            skArc(sketch, "E328", {"start": v(4510.92, 37465.2) * mm, "mid": v(4482.23, 37411.58) * mm, "end": v(4535.84, 37382.88) * mm});
            skLineSegment(sketch, "E329", {"start": v(4523.38, 37424.04) * mm, "end": v(4427.67, 37395.06) * mm});
            skLineSegment(sketch, "E330", {"start": v(4510.92, 37465.2) * mm, "end": v(4535.84, 37382.88) * mm});
            skLineSegment(sketch, "E331", {"start": v(4535.84, 37382.88) * mm, "end": v(4526.27, 37379.99) * mm});
            skLineSegment(sketch, "E332", {"start": v(4526.27, 37379.99) * mm, "end": v(4501.35, 37462.3) * mm});
            skLineSegment(sketch, "E333", {"start": v(4501.35, 37462.3) * mm, "end": v(4510.92, 37465.2) * mm});
            skLineSegment(sketch, "E334", {"start": v(5039.15, 35719.61) * mm, "end": v(5014.23, 35801.92) * mm});
            skArc(sketch, "E335", {"start": v(5014.23, 35801.92) * mm, "mid": v(4985.53, 35748.3) * mm, "end": v(5039.15, 35719.61) * mm});
            skLineSegment(sketch, "E336", {"start": v(5026.69, 35760.77) * mm, "end": v(4930.98, 35731.8) * mm});
            skLineSegment(sketch, "E337", {"start": v(5014.23, 35801.92) * mm, "end": v(5039.15, 35719.61) * mm});
            skLineSegment(sketch, "E338", {"start": v(5039.15, 35719.61) * mm, "end": v(5029.58, 35716.72) * mm});
            skLineSegment(sketch, "E339", {"start": v(5029.58, 35716.72) * mm, "end": v(5004.66, 35799.03) * mm});
            skLineSegment(sketch, "E340", {"start": v(5004.66, 35799.03) * mm, "end": v(5014.23, 35801.92) * mm});
            skCircle(sketch, "E341", {"center": v(4857.02, 35595.06) * mm, "radius": 24.96 * mm});
            skCircle(sketch, "E342", {"center": v(4857.02, 35595.06) * mm, "radius": 89.6 * mm});
            skLineSegment(sketch, "E343", {"start": v(578.84, 36955.8) * mm, "end": v(603.76, 36873.5) * mm});
            skArc(sketch, "E344", {"start": v(603.76, 36873.5) * mm, "mid": v(632.45, 36927.1) * mm, "end": v(578.84, 36955.8) * mm});
            skLineSegment(sketch, "E345", {"start": v(591.3, 36914.65) * mm, "end": v(687, 36943.62) * mm});
            skLineSegment(sketch, "E346", {"start": v(603.76, 36873.5) * mm, "end": v(578.84, 36955.8) * mm});
            skLineSegment(sketch, "E347", {"start": v(578.84, 36955.8) * mm, "end": v(588.41, 36958.7) * mm});
            skLineSegment(sketch, "E348", {"start": v(588.41, 36958.7) * mm, "end": v(613.33, 36876.4) * mm});
            skLineSegment(sketch, "E349", {"start": v(613.33, 36876.4) * mm, "end": v(603.76, 36873.5) * mm});
            skCircle(sketch, "E350", {"center": v(4620.62, 33505.38) * mm, "radius": 70 * mm});
            skArc(sketch, "E351", {"start": v(4956.81, 34398.56) * mm, "mid": v(4763.36, 34417.74) * mm, "end": v(4640.12, 34568.09) * mm});
            skArc(sketch, "E352", {"start": v(4640.12, 34568.09) * mm, "mid": v(4659.3, 34761.54) * mm, "end": v(4809.65, 34884.78) * mm});
            skArc(sketch, "E353", {"start": v(4809.65, 34884.78) * mm, "mid": v(5003.1, 34865.6) * mm, "end": v(5126.34, 34715.25) * mm});
            skArc(sketch, "E354", {"start": v(5126.34, 34715.25) * mm, "mid": v(5107.16, 34521.8) * mm, "end": v(4956.81, 34398.56) * mm});
            skLineSegment(sketch, "E355", {"start": v(4956.81, 34398.56) * mm, "end": v(4809.65, 34884.78) * mm});
            skArc(sketch, "E356", {"start": v(-1994.08, 35626.89) * mm, "mid": v(-1974.9, 35820.34) * mm, "end": v(-1824.55, 35943.58) * mm});
            skArc(sketch, "E357", {"start": v(4471.25, 25817.53) * mm, "mid": v(4277.8, 25836.7) * mm, "end": v(4154.56, 25987.06) * mm});
            skArc(sketch, "E358", {"start": v(4154.56, 25987.06) * mm, "mid": v(4173.74, 26180.51) * mm, "end": v(4324.09, 26303.75) * mm});
            skArc(sketch, "E359", {"start": v(4324.09, 26303.75) * mm, "mid": v(4517.54, 26284.58) * mm, "end": v(4640.78, 26134.23) * mm});
            skArc(sketch, "E360", {"start": v(4640.78, 26134.23) * mm, "mid": v(4621.6, 25940.77) * mm, "end": v(4471.25, 25817.53) * mm});
            skLineSegment(sketch, "E361", {"start": v(4471.25, 25817.53) * mm, "end": v(4324.09, 26303.75) * mm});
            skArc(sketch, "E362", {"start": v(273.35, 36589.26) * mm, "mid": v(79.9, 36608.44) * mm, "end": v(-43.34, 36758.79) * mm});
            skCircle(sketch, "E363", {"center": v(3141.78, 35075.9) * mm, "radius": 70 * mm});
            skCircle(sketch, "E364", {"center": v(-35072.5, -36736.78) * mm, "radius": 1927.6 * mm});
            skLineSegment(sketch, "E365", {"start": v(-35072.5, -31736.78) * mm, "end": v(-35072.5, -41736.78) * mm});
            skLineSegment(sketch, "E366", {"start": v(-30072.5, -36736.78) * mm, "end": v(-40072.5, -36736.78) * mm});
            skLineSegment(sketch, "E367", {"start": v(9242.48, 21401.51) * mm, "end": v(8565.25, 23638.8) * mm});
            skLineSegment(sketch, "E368", {"start": v(9228.12, 21397.17) * mm, "end": v(8546.54, 23648.8) * mm});
            skLineSegment(sketch, "E369", {"start": v(9256.83, 21405.86) * mm, "end": v(8583.95, 23628.78) * mm});
            skLineSegment(sketch, "E370", {"start": v(9271.19, 21410.2) * mm, "end": v(8602.65, 23618.77) * mm});
            skLineSegment(sketch, "E371", {"start": v(9357.33, 21436.28) * mm, "end": v(8714.87, 23558.7) * mm});
            skLineSegment(sketch, "E372", {"start": v(9288.42, 21415.42) * mm, "end": v(8625.1, 23606.76) * mm});
            skLineSegment(sketch, "E373", {"start": v(9386.04, 21444.97) * mm, "end": v(8752.27, 23538.68) * mm});
            skLineSegment(sketch, "E374", {"start": v(-555.06, 29916.66) * mm, "end": v(7885.74, 20220.31) * mm});
            skLineSegment(sketch, "E375", {"start": v(7885.74, 20220.31) * mm, "end": v(7849.46, 20094.46) * mm});
            skLineSegment(sketch, "E376", {"start": v(7849.46, 20094.46) * mm, "end": v(-620.1, 29823.84) * mm});
            skLineSegment(sketch, "E377", {"start": v(-620.1, 29823.84) * mm, "end": v(-555.06, 29916.66) * mm});
            skLineSegment(sketch, "E378", {"start": v(7849.46, 20094.46) * mm, "end": v(7885.66, 20220.35) * mm});
            skLineSegment(sketch, "E379", {"start": v(-2682.94, 29199.46) * mm, "end": v(-2636.22, 29286.74) * mm});
            skLineSegment(sketch, "E380", {"start": v(-555.06, 29916.66) * mm, "end": v(-620.1, 29823.84) * mm});
            skLineSegment(sketch, "E381", {"start": v(-620.1, 29823.84) * mm, "end": v(-2682.94, 29199.46) * mm});
            skLineSegment(sketch, "E382", {"start": v(3515.53, 38130.64) * mm, "end": v(3524.41, 38061.2) * mm});
            skLineSegment(sketch, "E383", {"start": v(3524.41, 38061.2) * mm, "end": v(743.5, 37705.2) * mm});
            skLineSegment(sketch, "E384", {"start": v(743.5, 37705.2) * mm, "end": v(743.46, 37705.55) * mm});
            skLineSegment(sketch, "E385", {"start": v(743.46, 37705.55) * mm, "end": v(-4686.9, 36060.36) * mm});
            skLineSegment(sketch, "E386", {"start": v(-4686.9, 36060.36) * mm, "end": v(-2636.07, 29286.24) * mm});
            skLineSegment(sketch, "E387", {"start": v(-2636.07, 29286.24) * mm, "end": v(-2682.94, 29199.46) * mm});
            skLineSegment(sketch, "E388", {"start": v(-2682.94, 29199.46) * mm, "end": v(-4757.89, 36053.23) * mm});
            skLineSegment(sketch, "E389", {"start": v(-4757.89, 36053.23) * mm, "end": v(-4774.2, 36107.06) * mm});
            skLineSegment(sketch, "E390", {"start": v(-4774.2, 36107.06) * mm, "end": v(-4774.18, 36107.06) * mm});
            skLineSegment(sketch, "E391", {"start": v(-4774.18, 36107.06) * mm, "end": v(-4774.19, 36107.07) * mm});
            skLineSegment(sketch, "E392", {"start": v(-4774.19, 36107.07) * mm, "end": v(-4750.75, 36114.16) * mm});
            skLineSegment(sketch, "E393", {"start": v(-4750.75, 36114.16) * mm, "end": v(734.23, 37775.9) * mm});
            skLineSegment(sketch, "E394", {"start": v(734.23, 37775.9) * mm, "end": v(734.61, 37774.63) * mm});
            skLineSegment(sketch, "E395", {"start": v(734.61, 37774.63) * mm, "end": v(3515.53, 38130.64) * mm});
            skLineSegment(sketch, "E396", {"start": v(3768.72, 38142.6) * mm, "end": v(3798.48, 38146.42) * mm});
            skLineSegment(sketch, "E397", {"start": v(3606.47, 38071.38) * mm, "end": v(3600.1, 38120.97) * mm});
            skLineSegment(sketch, "E398", {"start": v(3768.72, 38142.6) * mm, "end": v(3741.51, 38118.95) * mm});
            skLineSegment(sketch, "E399", {"start": v(3741.51, 38118.95) * mm, "end": v(3602.65, 38101.14) * mm});
            skLineSegment(sketch, "E400", {"start": v(3804.84, 38096.83) * mm, "end": v(3798.48, 38146.42) * mm});
            skLineSegment(sketch, "E401", {"start": v(3408.1, 38045.93) * mm, "end": v(3404.28, 38075.69) * mm});
            skLineSegment(sketch, "E402", {"start": v(3543.14, 38093.5) * mm, "end": v(3404.28, 38075.69) * mm});
            skLineSegment(sketch, "E403", {"start": v(3570.35, 38117.16) * mm, "end": v(3543.14, 38093.5) * mm});
            skLineSegment(sketch, "E404", {"start": v(3600.1, 38120.97) * mm, "end": v(3570.35, 38117.16) * mm});
            skLineSegment(sketch, "E405", {"start": v(3408.1, 38045.93) * mm, "end": v(4737.2, 38216.43) * mm});
            skLineSegment(sketch, "E406", {"start": v(3801.03, 38126.58) * mm, "end": v(3939.89, 38144.4) * mm});
            skLineSegment(sketch, "E407", {"start": v(3967.1, 38168.05) * mm, "end": v(3939.89, 38144.4) * mm});
            skLineSegment(sketch, "E408", {"start": v(3996.85, 38171.87) * mm, "end": v(3967.1, 38168.05) * mm});
            skLineSegment(sketch, "E409", {"start": v(4003.22, 38122.28) * mm, "end": v(3996.85, 38171.87) * mm});
            skLineSegment(sketch, "E410", {"start": v(4201.6, 38147.72) * mm, "end": v(4195.23, 38197.32) * mm});
            skLineSegment(sketch, "E411", {"start": v(4733.39, 38246.19) * mm, "end": v(4197.77, 38177.48) * mm});
            skLineSegment(sketch, "E412", {"start": v(3348.58, 38038.33) * mm, "end": v(3342.21, 38087.92) * mm});
            skLineSegment(sketch, "E413", {"start": v(3371.97, 38091.74) * mm, "end": v(3342.21, 38087.92) * mm});
            skLineSegment(sketch, "E414", {"start": v(3348.58, 38038.33) * mm, "end": v(3408.1, 38045.93) * mm});
            skLineSegment(sketch, "E415", {"start": v(3404.28, 38075.69) * mm, "end": v(3371.97, 38091.74) * mm});
            skLineSegment(sketch, "E416", {"start": v(4165.47, 38193.5) * mm, "end": v(4138.26, 38169.84) * mm});
            skLineSegment(sketch, "E417", {"start": v(4195.23, 38197.32) * mm, "end": v(4165.47, 38193.5) * mm});
            skLineSegment(sketch, "E418", {"start": v(4138.26, 38169.84) * mm, "end": v(3999.4, 38152.03) * mm});
            skLineSegment(sketch, "E419", {"start": v(4790.35, 38273.7) * mm, "end": v(4796.71, 38224.1) * mm});
            skLineSegment(sketch, "E420", {"start": v(4733.39, 38246.19) * mm, "end": v(4737.2, 38216.43) * mm});
            skLineSegment(sketch, "E421", {"start": v(4760.6, 38269.87) * mm, "end": v(4733.39, 38246.19) * mm});
            skLineSegment(sketch, "E422", {"start": v(4790.35, 38273.7) * mm, "end": v(4760.6, 38269.87) * mm});
            skLineSegment(sketch, "E423", {"start": v(4737.2, 38216.43) * mm, "end": v(4796.71, 38224.1) * mm});
            skLineSegment(sketch, "E424", {"start": v(2753.45, 37961.99) * mm, "end": v(2747.1, 38011.58) * mm});
            skLineSegment(sketch, "E425", {"start": v(2812.97, 37969.6) * mm, "end": v(2753.45, 37961.99) * mm});
            skLineSegment(sketch, "E426", {"start": v(2809.15, 37999.35) * mm, "end": v(2776.85, 38015.4) * mm});
            skLineSegment(sketch, "E427", {"start": v(2776.85, 38015.4) * mm, "end": v(2747.1, 38011.58) * mm});
            skLineSegment(sketch, "E428", {"start": v(2812.97, 37969.6) * mm, "end": v(3348.58, 38038.3) * mm});
            skLineSegment(sketch, "E429", {"start": v(2809.15, 37999.35) * mm, "end": v(2812.97, 37969.6) * mm});
            skLineSegment(sketch, "E430", {"start": v(3344.76, 38068.05) * mm, "end": v(2809.15, 37999.35) * mm});
            skLineSegment(sketch, "E431", {"start": v(3348.58, 38038.3) * mm, "end": v(3344.76, 38068.05) * mm});
            skLineSegment(sketch, "E432", {"start": v(2471.88, 26438.95) * mm, "end": v(2603.24, 26288.13) * mm});
            skLineSegment(sketch, "E433", {"start": v(2603.24, 26288.13) * mm, "end": v(2580.61, 26268.42) * mm});
            skLineSegment(sketch, "E434", {"start": v(2580.61, 26268.42) * mm, "end": v(2488.67, 26374) * mm});
            skLineSegment(sketch, "E435", {"start": v(2488.67, 26374) * mm, "end": v(2423.72, 26357.21) * mm});
            skLineSegment(sketch, "E436", {"start": v(2423.72, 26357.21) * mm, "end": v(2404.02, 26379.84) * mm});
            skLineSegment(sketch, "E437", {"start": v(2404.02, 26379.84) * mm, "end": v(2471.88, 26438.95) * mm});
            skLineSegment(sketch, "E438", {"start": v(2603.24, 26288.13) * mm, "end": v(2734.6, 26137.3) * mm});
            skLineSegment(sketch, "E439", {"start": v(2734.6, 26137.3) * mm, "end": v(2711.97, 26117.6) * mm});
            skLineSegment(sketch, "E440", {"start": v(2711.97, 26117.6) * mm, "end": v(2620.02, 26223.18) * mm});
            skLineSegment(sketch, "E441", {"start": v(2620.02, 26223.18) * mm, "end": v(2555.07, 26206.4) * mm});
            skLineSegment(sketch, "E442", {"start": v(2555.07, 26206.4) * mm, "end": v(2535.37, 26229.02) * mm});
            skLineSegment(sketch, "E443", {"start": v(2535.37, 26229.02) * mm, "end": v(2603.24, 26288.13) * mm});
            skLineSegment(sketch, "E444", {"start": v(2734.6, 26137.3) * mm, "end": v(2865.94, 25986.49) * mm});
            skLineSegment(sketch, "E445", {"start": v(2865.94, 25986.49) * mm, "end": v(2843.32, 25966.79) * mm});
            skLineSegment(sketch, "E446", {"start": v(2843.32, 25966.79) * mm, "end": v(2751.37, 26072.36) * mm});
            skLineSegment(sketch, "E447", {"start": v(2751.37, 26072.36) * mm, "end": v(2686.43, 26055.58) * mm});
            skLineSegment(sketch, "E448", {"start": v(2686.43, 26055.58) * mm, "end": v(2666.72, 26078.2) * mm});
            skLineSegment(sketch, "E449", {"start": v(2666.72, 26078.2) * mm, "end": v(2734.6, 26137.3) * mm});
            skLineSegment(sketch, "E450", {"start": v(2865.94, 25986.49) * mm, "end": v(2997.3, 25835.67) * mm});
            skLineSegment(sketch, "E451", {"start": v(2997.3, 25835.67) * mm, "end": v(2974.67, 25815.97) * mm});
            skLineSegment(sketch, "E452", {"start": v(2974.67, 25815.97) * mm, "end": v(2882.73, 25921.54) * mm});
            skLineSegment(sketch, "E453", {"start": v(2882.73, 25921.54) * mm, "end": v(2817.78, 25904.76) * mm});
            skLineSegment(sketch, "E454", {"start": v(2817.78, 25904.76) * mm, "end": v(2798.08, 25927.38) * mm});
            skLineSegment(sketch, "E455", {"start": v(2798.08, 25927.38) * mm, "end": v(2865.94, 25986.49) * mm});
            skLineSegment(sketch, "E456", {"start": v(2077.55, 26891.72) * mm, "end": v(2116.95, 26846.47) * mm});
            skLineSegment(sketch, "E457", {"start": v(2116.95, 26846.47) * mm, "end": v(2094.33, 26826.77) * mm});
            skLineSegment(sketch, "E458", {"start": v(2094.33, 26826.77) * mm, "end": v(2029.38, 26809.99) * mm});
            skLineSegment(sketch, "E459", {"start": v(2029.38, 26809.99) * mm, "end": v(2009.68, 26832.6) * mm});
            skLineSegment(sketch, "E460", {"start": v(2009.68, 26832.6) * mm, "end": v(2077.55, 26891.72) * mm});
            skLineSegment(sketch, "E461", {"start": v(2471.6, 26439.26) * mm, "end": v(2116.95, 26846.47) * mm});
            skLineSegment(sketch, "E462", {"start": v(2094.33, 26826.77) * mm, "end": v(2448.99, 26419.56) * mm});
            skLineSegment(sketch, "E463", {"start": v(2448.99, 26419.56) * mm, "end": v(2471.6, 26439.26) * mm});
            skLineSegment(sketch, "E464", {"start": v(3036.7, 25790.42) * mm, "end": v(2997.3, 25835.67) * mm});
            skLineSegment(sketch, "E465", {"start": v(2974.67, 25815.97) * mm, "end": v(2949.13, 25753.94) * mm});
            skLineSegment(sketch, "E466", {"start": v(2949.13, 25753.94) * mm, "end": v(2968.83, 25731.32) * mm});
            skLineSegment(sketch, "E467", {"start": v(2968.83, 25731.32) * mm, "end": v(3036.7, 25790.42) * mm});
            skLineSegment(sketch, "E468", {"start": v(3430.76, 25337.97) * mm, "end": v(3391.36, 25383.21) * mm});
            skLineSegment(sketch, "E469", {"start": v(3391.36, 25383.21) * mm, "end": v(3368.73, 25363.51) * mm});
            skLineSegment(sketch, "E470", {"start": v(3368.73, 25363.51) * mm, "end": v(3343.2, 25301.48) * mm});
            skLineSegment(sketch, "E471", {"start": v(3343.2, 25301.48) * mm, "end": v(3362.9, 25278.86) * mm});
            skLineSegment(sketch, "E472", {"start": v(3362.9, 25278.86) * mm, "end": v(3430.76, 25337.97) * mm});
            skLineSegment(sketch, "E473", {"start": v(3014.08, 25770.72) * mm, "end": v(3368.73, 25363.51) * mm});
            skLineSegment(sketch, "E474", {"start": v(3368.73, 25363.51) * mm, "end": v(3391.36, 25383.21) * mm});
            skLineSegment(sketch, "E475", {"start": v(3391.36, 25383.21) * mm, "end": v(3036.7, 25790.42) * mm});
            skLineSegment(sketch, "E476", {"start": v(3036.7, 25790.42) * mm, "end": v(3014.08, 25770.72) * mm});
            skLineSegment(sketch, "E477", {"start": v(-2910.05, 30088.31) * mm, "end": v(-2881.33, 30097) * mm});
            skLineSegment(sketch, "E478", {"start": v(-2881.33, 30097) * mm, "end": v(-2636.22, 29286.74) * mm});
            skLineSegment(sketch, "E479", {"start": v(-2636.22, 29286.74) * mm, "end": v(-2656.24, 29249.34) * mm});
            skLineSegment(sketch, "E480", {"start": v(-2656.24, 29249.34) * mm, "end": v(-2910.05, 30088.31) * mm});
            skLineSegment(sketch, "E481", {"start": v(-2088.4, 29452.6) * mm, "end": v(-2079.7, 29423.88) * mm});
            skLineSegment(sketch, "E482", {"start": v(-2079.7, 29423.88) * mm, "end": v(-2656.24, 29249.34) * mm});
            skLineSegment(sketch, "E483", {"start": v(-2656.24, 29249.34) * mm, "end": v(-2636.22, 29286.74) * mm});
            skLineSegment(sketch, "E484", {"start": v(-2636.22, 29286.74) * mm, "end": v(-2088.4, 29452.6) * mm});
            skLineSegment(sketch, "E485", {"start": v(-2030.96, 29469.96) * mm, "end": v(-2016.46, 29422.11) * mm});
            skLineSegment(sketch, "E486", {"start": v(-2016.46, 29422.11) * mm, "end": v(-2045.17, 29413.41) * mm});
            skLineSegment(sketch, "E487", {"start": v(-2045.17, 29413.41) * mm, "end": v(-2079.7, 29423.88) * mm});
            skLineSegment(sketch, "E488", {"start": v(-2079.7, 29423.88) * mm, "end": v(-2088.4, 29452.6) * mm});
            skLineSegment(sketch, "E489", {"start": v(-2088.4, 29452.6) * mm, "end": v(-2030.96, 29469.96) * mm});
            skLineSegment(sketch, "E490", {"start": v(-2898.85, 30154.38) * mm, "end": v(-2946.71, 30139.92) * mm});
            skLineSegment(sketch, "E491", {"start": v(-2946.71, 30139.92) * mm, "end": v(-2938.04, 30111.2) * mm});
            skLineSegment(sketch, "E492", {"start": v(-2938.04, 30111.2) * mm, "end": v(-2910.18, 30088.28) * mm});
            skLineSegment(sketch, "E493", {"start": v(-2910.18, 30088.28) * mm, "end": v(-2881.47, 30096.96) * mm});
            skLineSegment(sketch, "E494", {"start": v(-2881.47, 30096.96) * mm, "end": v(-2898.85, 30154.38) * mm});
            skLineSegment(sketch, "E495", {"start": v(-4686.52, 36060.6) * mm, "end": v(-4635.85, 35893.73) * mm});
            skLineSegment(sketch, "E496", {"start": v(-4635.85, 35893.73) * mm, "end": v(-4664.56, 35885.04) * mm});
            skLineSegment(sketch, "E497", {"start": v(-4664.56, 35885.04) * mm, "end": v(-4723.92, 36080.62) * mm});
            skLineSegment(sketch, "E498", {"start": v(-4723.92, 36080.62) * mm, "end": v(-4399.26, 36178.88) * mm});
            skLineSegment(sketch, "E499", {"start": v(-4399.26, 36178.88) * mm, "end": v(-4390.57, 36150.17) * mm});
            skLineSegment(sketch, "E500", {"start": v(-4390.57, 36150.17) * mm, "end": v(-4686.52, 36060.6) * mm});
            skLineSegment(sketch, "E501", {"start": v(-3950.3, 36283.42) * mm, "end": v(-4141.72, 36225.48) * mm});
            skLineSegment(sketch, "E502", {"start": v(-4141.72, 36225.48) * mm, "end": v(-4150.4, 36254.2) * mm});
            skLineSegment(sketch, "E503", {"start": v(-4150.4, 36254.2) * mm, "end": v(-4016.41, 36294.75) * mm});
            skLineSegment(sketch, "E504", {"start": v(-4016.41, 36294.75) * mm, "end": v(-3993.49, 36322.58) * mm});
            skLineSegment(sketch, "E505", {"start": v(-3993.49, 36322.58) * mm, "end": v(-3964.78, 36331.27) * mm});
            skLineSegment(sketch, "E506", {"start": v(-3964.78, 36331.27) * mm, "end": v(-3950.3, 36283.42) * mm});
            skLineSegment(sketch, "E507", {"start": v(-4141.72, 36225.48) * mm, "end": v(-4333.14, 36167.55) * mm});
            skLineSegment(sketch, "E508", {"start": v(-4333.14, 36167.55) * mm, "end": v(-4341.83, 36196.26) * mm});
            skLineSegment(sketch, "E509", {"start": v(-4341.83, 36196.26) * mm, "end": v(-4207.84, 36236.81) * mm});
            skLineSegment(sketch, "E510", {"start": v(-4207.84, 36236.81) * mm, "end": v(-4184.91, 36264.65) * mm});
            skLineSegment(sketch, "E511", {"start": v(-4184.91, 36264.65) * mm, "end": v(-4156.2, 36273.34) * mm});
            skLineSegment(sketch, "E512", {"start": v(-4156.2, 36273.34) * mm, "end": v(-4141.72, 36225.48) * mm});
            skLineSegment(sketch, "E513", {"start": v(-3758.87, 36341.35) * mm, "end": v(-3950.3, 36283.42) * mm});
            skLineSegment(sketch, "E514", {"start": v(-3950.3, 36283.42) * mm, "end": v(-3958.98, 36312.13) * mm});
            skLineSegment(sketch, "E515", {"start": v(-3958.98, 36312.13) * mm, "end": v(-3824.98, 36352.68) * mm});
            skLineSegment(sketch, "E516", {"start": v(-3824.98, 36352.68) * mm, "end": v(-3802.06, 36380.52) * mm});
            skLineSegment(sketch, "E517", {"start": v(-3802.06, 36380.52) * mm, "end": v(-3773.35, 36389.2) * mm});
            skLineSegment(sketch, "E518", {"start": v(-3773.35, 36389.2) * mm, "end": v(-3758.87, 36341.35) * mm});
            skLineSegment(sketch, "E519", {"start": v(-3050.6, 36555.7) * mm, "end": v(-3567.44, 36399.28) * mm});
            skLineSegment(sketch, "E520", {"start": v(-3567.44, 36399.28) * mm, "end": v(-3576.13, 36428) * mm});
            skLineSegment(sketch, "E521", {"start": v(-3576.13, 36428) * mm, "end": v(-3059.28, 36584.42) * mm});
            skLineSegment(sketch, "E522", {"start": v(-3059.28, 36584.42) * mm, "end": v(-3050.6, 36555.7) * mm});
            skLineSegment(sketch, "E523", {"start": v(-4405.06, 36198.05) * mm, "end": v(-4376.35, 36206.74) * mm});
            skLineSegment(sketch, "E524", {"start": v(-4376.35, 36206.74) * mm, "end": v(-4341.83, 36196.26) * mm});
            skLineSegment(sketch, "E525", {"start": v(-4341.83, 36196.26) * mm, "end": v(-4333.14, 36167.55) * mm});
            skLineSegment(sketch, "E526", {"start": v(-4333.14, 36167.55) * mm, "end": v(-4390.58, 36150.2) * mm});
            skLineSegment(sketch, "E527", {"start": v(-4390.58, 36150.2) * mm, "end": v(-4405.06, 36198.05) * mm});
            skLineSegment(sketch, "E528", {"start": v(-3567.44, 36399.28) * mm, "end": v(-3758.87, 36341.35) * mm});
            skLineSegment(sketch, "E529", {"start": v(-3758.87, 36341.35) * mm, "end": v(-3767.56, 36370.06) * mm});
            skLineSegment(sketch, "E530", {"start": v(-3767.56, 36370.06) * mm, "end": v(-3633.56, 36410.62) * mm});
            skLineSegment(sketch, "E531", {"start": v(-3633.56, 36410.62) * mm, "end": v(-3610.64, 36438.45) * mm});
            skLineSegment(sketch, "E532", {"start": v(-3610.64, 36438.45) * mm, "end": v(-3581.93, 36447.14) * mm});
            skLineSegment(sketch, "E533", {"start": v(-3581.93, 36447.14) * mm, "end": v(-3567.44, 36399.28) * mm});
            skLineSegment(sketch, "E534", {"start": v(-2993.18, 36573.12) * mm, "end": v(-3050.6, 36555.7) * mm});
            skLineSegment(sketch, "E535", {"start": v(-3050.6, 36555.7) * mm, "end": v(-3059.28, 36584.42) * mm});
            skLineSegment(sketch, "E536", {"start": v(-3059.28, 36584.42) * mm, "end": v(-3036.37, 36612.28) * mm});
            skLineSegment(sketch, "E537", {"start": v(-3036.37, 36612.28) * mm, "end": v(-3007.66, 36620.97) * mm});
            skLineSegment(sketch, "E538", {"start": v(-3007.66, 36620.97) * mm, "end": v(-2993.18, 36573.12) * mm});
            skLineSegment(sketch, "E539", {"start": v(-4619.02, 35836.13) * mm, "end": v(-4636.37, 35893.57) * mm});
            skLineSegment(sketch, "E540", {"start": v(-4636.37, 35893.57) * mm, "end": v(-4665.08, 35884.88) * mm});
            skLineSegment(sketch, "E541", {"start": v(-4665.08, 35884.88) * mm, "end": v(-4675.57, 35850.36) * mm});
            skLineSegment(sketch, "E542", {"start": v(-4675.57, 35850.36) * mm, "end": v(-4666.88, 35821.65) * mm});
            skLineSegment(sketch, "E543", {"start": v(-4666.88, 35821.65) * mm, "end": v(-4619.02, 35836.13) * mm});
            skLineSegment(sketch, "E544", {"start": v(-1686.93, 37020.72) * mm, "end": v(-1666.83, 37026.8) * mm});
            skLineSegment(sketch, "E545", {"start": v(-1718.45, 36990.25) * mm, "end": v(-1686.93, 37020.72) * mm});
            skLineSegment(sketch, "E546", {"start": v(-1709.76, 36961.54) * mm, "end": v(-1718.45, 36990.25) * mm});
            skLineSegment(sketch, "E547", {"start": v(-1652.34, 36978.95) * mm, "end": v(-1709.76, 36961.54) * mm});
            skLineSegment(sketch, "E548", {"start": v(-1666.83, 37026.8) * mm, "end": v(-1652.34, 36978.95) * mm});
            skLineSegment(sketch, "E549", {"start": v(-2452.62, 36788.96) * mm, "end": v(-2432.52, 36795.05) * mm});
            skLineSegment(sketch, "E550", {"start": v(-2484.15, 36758.5) * mm, "end": v(-2452.62, 36788.96) * mm});
            skLineSegment(sketch, "E551", {"start": v(-2475.46, 36729.78) * mm, "end": v(-2484.15, 36758.5) * mm});
            skLineSegment(sketch, "E552", {"start": v(-2418.04, 36747.2) * mm, "end": v(-2475.46, 36729.78) * mm});
            skLineSegment(sketch, "E553", {"start": v(-2432.52, 36795.05) * mm, "end": v(-2418.04, 36747.2) * mm});
            skLineSegment(sketch, "E554", {"start": v(6158.14, 38449.15) * mm, "end": v(6178.97, 38451.82) * mm});
            skLineSegment(sketch, "E555", {"start": v(6122, 38424.32) * mm, "end": v(6158.14, 38449.15) * mm});
            skLineSegment(sketch, "E556", {"start": v(6125.82, 38394.56) * mm, "end": v(6122, 38424.32) * mm});
            skLineSegment(sketch, "E557", {"start": v(6185.33, 38402.23) * mm, "end": v(6125.82, 38394.56) * mm});
            skLineSegment(sketch, "E558", {"start": v(6178.97, 38451.82) * mm, "end": v(6185.33, 38402.23) * mm});
            skLineSegment(sketch, "E559", {"start": v(5364.64, 38347.36) * mm, "end": v(5385.47, 38350.03) * mm});
            skLineSegment(sketch, "E560", {"start": v(5328.5, 38322.53) * mm, "end": v(5364.64, 38347.36) * mm});
            skLineSegment(sketch, "E561", {"start": v(5332.33, 38292.77) * mm, "end": v(5328.5, 38322.53) * mm});
            skLineSegment(sketch, "E562", {"start": v(5391.83, 38300.44) * mm, "end": v(5332.33, 38292.77) * mm});
            skLineSegment(sketch, "E563", {"start": v(5385.47, 38350.03) * mm, "end": v(5391.83, 38300.44) * mm});
            skLineSegment(sketch, "E564", {"start": v(2190.65, 37940.2) * mm, "end": v(2211.48, 37942.87) * mm});
            skLineSegment(sketch, "E565", {"start": v(2154.52, 37915.37) * mm, "end": v(2190.65, 37940.2) * mm});
            skLineSegment(sketch, "E566", {"start": v(2158.33, 37885.61) * mm, "end": v(2154.52, 37915.37) * mm});
            skLineSegment(sketch, "E567", {"start": v(2217.84, 37893.28) * mm, "end": v(2158.33, 37885.61) * mm});
            skLineSegment(sketch, "E568", {"start": v(2211.48, 37942.87) * mm, "end": v(2217.84, 37893.28) * mm});
            skLineSegment(sketch, "E569", {"start": v(1397.15, 37838.41) * mm, "end": v(1417.98, 37841.08) * mm});
            skLineSegment(sketch, "E570", {"start": v(1361.02, 37813.58) * mm, "end": v(1397.15, 37838.41) * mm});
            skLineSegment(sketch, "E571", {"start": v(1364.84, 37783.82) * mm, "end": v(1361.02, 37813.58) * mm});
            skLineSegment(sketch, "E572", {"start": v(1424.35, 37791.49) * mm, "end": v(1364.84, 37783.82) * mm});
            skLineSegment(sketch, "E573", {"start": v(1417.98, 37841.08) * mm, "end": v(1424.35, 37791.49) * mm});
            skLineSegment(sketch, "E574", {"start": v(-3807.12, 32982.54) * mm, "end": v(-3815.8, 33011.25) * mm});
            skLineSegment(sketch, "E575", {"start": v(-3710.01, 32834.31) * mm, "end": v(-3757.87, 32819.83) * mm});
            skLineSegment(sketch, "E576", {"start": v(-3807.12, 32982.54) * mm, "end": v(-3779.28, 32959.62) * mm});
            skLineSegment(sketch, "E577", {"start": v(-3779.28, 32959.62) * mm, "end": v(-3738.72, 32825.62) * mm});
            skLineSegment(sketch, "E578", {"start": v(-3767.95, 33025.74) * mm, "end": v(-3815.8, 33011.25) * mm});
            skLineSegment(sketch, "E579", {"start": v(-3652.07, 32642.9) * mm, "end": v(-3680.78, 32634.2) * mm});
            skLineSegment(sketch, "E580", {"start": v(-3721.34, 32768.2) * mm, "end": v(-3680.78, 32634.2) * mm});
            skLineSegment(sketch, "E581", {"start": v(-3749.18, 32791.12) * mm, "end": v(-3721.34, 32768.2) * mm});
            skLineSegment(sketch, "E582", {"start": v(-3757.87, 32819.83) * mm, "end": v(-3749.18, 32791.12) * mm});
            skLineSegment(sketch, "E583", {"start": v(-3652.07, 32642.9) * mm, "end": v(-4040.27, 33925.43) * mm});
            skLineSegment(sketch, "E584", {"start": v(-3796.66, 33017.05) * mm, "end": v(-3837.22, 33151.04) * mm});
            skLineSegment(sketch, "E585", {"start": v(-3865.06, 33173.96) * mm, "end": v(-3837.22, 33151.04) * mm});
            skLineSegment(sketch, "E586", {"start": v(-3873.75, 33202.68) * mm, "end": v(-3865.06, 33173.96) * mm});
            skLineSegment(sketch, "E587", {"start": v(-3825.9, 33217.16) * mm, "end": v(-3873.75, 33202.68) * mm});
            skLineSegment(sketch, "E588", {"start": v(-3883.83, 33408.58) * mm, "end": v(-3931.69, 33394.1) * mm});
            skLineSegment(sketch, "E589", {"start": v(-4068.98, 33916.74) * mm, "end": v(-3912.54, 33399.9) * mm});
            skLineSegment(sketch, "E590", {"start": v(-3634.72, 32585.45) * mm, "end": v(-3682.58, 32570.97) * mm});
            skLineSegment(sketch, "E591", {"start": v(-3691.27, 32599.68) * mm, "end": v(-3682.58, 32570.97) * mm});
            skLineSegment(sketch, "E592", {"start": v(-3634.72, 32585.45) * mm, "end": v(-3652.07, 32642.9) * mm});
            skLineSegment(sketch, "E593", {"start": v(-3680.78, 32634.2) * mm, "end": v(-3691.27, 32599.68) * mm});
            skLineSegment(sketch, "E594", {"start": v(-3923, 33365.39) * mm, "end": v(-3895.16, 33342.47) * mm});
            skLineSegment(sketch, "E595", {"start": v(-3931.69, 33394.1) * mm, "end": v(-3923, 33365.39) * mm});
            skLineSegment(sketch, "E596", {"start": v(-3895.16, 33342.47) * mm, "end": v(-3854.6, 33208.47) * mm});
            skLineSegment(sketch, "E597", {"start": v(-4105.54, 33968.36) * mm, "end": v(-4057.68, 33982.85) * mm});
            skLineSegment(sketch, "E598", {"start": v(-4068.98, 33916.74) * mm, "end": v(-4040.27, 33925.43) * mm});
            skLineSegment(sketch, "E599", {"start": v(-4096.85, 33939.65) * mm, "end": v(-4068.98, 33916.74) * mm});
            skLineSegment(sketch, "E600", {"start": v(-4105.54, 33968.36) * mm, "end": v(-4096.85, 33939.65) * mm});
            skLineSegment(sketch, "E601", {"start": v(-4040.27, 33925.43) * mm, "end": v(-4057.68, 33982.85) * mm});
            skLineSegment(sketch, "E602", {"start": v(-3460.9, 32011.18) * mm, "end": v(-3508.76, 31996.7) * mm});
            skLineSegment(sketch, "E603", {"start": v(-3478.25, 32068.62) * mm, "end": v(-3460.9, 32011.18) * mm});
            skLineSegment(sketch, "E604", {"start": v(-3506.96, 32059.93) * mm, "end": v(-3517.45, 32025.41) * mm});
            skLineSegment(sketch, "E605", {"start": v(-3517.45, 32025.41) * mm, "end": v(-3508.76, 31996.7) * mm});
            skLineSegment(sketch, "E606", {"start": v(-3478.25, 32068.62) * mm, "end": v(-3634.69, 32585.46) * mm});
            skLineSegment(sketch, "E607", {"start": v(-3506.96, 32059.93) * mm, "end": v(-3478.25, 32068.62) * mm});
            skLineSegment(sketch, "E608", {"start": v(-3663.4, 32576.77) * mm, "end": v(-3506.96, 32059.93) * mm});
            skLineSegment(sketch, "E609", {"start": v(-3634.69, 32585.46) * mm, "end": v(-3663.4, 32576.77) * mm});
            skLineSegment(sketch, "E610", {"start": v(-3460.87, 32011.2) * mm, "end": v(-3304.43, 31494.35) * mm});
            skLineSegment(sketch, "E611", {"start": v(-3304.43, 31494.35) * mm, "end": v(-3333.14, 31485.66) * mm});
            skLineSegment(sketch, "E612", {"start": v(-3333.14, 31485.66) * mm, "end": v(-3489.58, 32002.5) * mm});
            skLineSegment(sketch, "E613", {"start": v(-3489.58, 32002.5) * mm, "end": v(-3460.87, 32011.2) * mm});
            skLineSegment(sketch, "E614", {"start": v(-3120.56, 30714.16) * mm, "end": v(-3114.47, 30694.06) * mm});
            skLineSegment(sketch, "E615", {"start": v(-3114.47, 30694.06) * mm, "end": v(-3084, 30662.54) * mm});
            skLineSegment(sketch, "E616", {"start": v(-3084, 30662.54) * mm, "end": v(-3055.29, 30671.23) * mm});
            skLineSegment(sketch, "E617", {"start": v(-3055.29, 30671.23) * mm, "end": v(-3072.7, 30728.65) * mm});
            skLineSegment(sketch, "E618", {"start": v(-3072.7, 30728.65) * mm, "end": v(-3120.56, 30714.16) * mm});
            skLineSegment(sketch, "E619", {"start": v(-3055.29, 30671.23) * mm, "end": v(-2898.85, 30154.38) * mm});
            skLineSegment(sketch, "E620", {"start": v(-2898.85, 30154.38) * mm, "end": v(-2927.56, 30145.7) * mm});
            skLineSegment(sketch, "E621", {"start": v(-2927.56, 30145.7) * mm, "end": v(-3084, 30662.54) * mm});
            skLineSegment(sketch, "E622", {"start": v(-3334.94, 31422.43) * mm, "end": v(-3341.02, 31442.53) * mm});
            skLineSegment(sketch, "E623", {"start": v(-3341.02, 31442.53) * mm, "end": v(-3333.14, 31485.66) * mm});
            skLineSegment(sketch, "E624", {"start": v(-3333.14, 31485.66) * mm, "end": v(-3304.43, 31494.35) * mm});
            skLineSegment(sketch, "E625", {"start": v(-3304.43, 31494.35) * mm, "end": v(-3287.08, 31436.91) * mm});
            skLineSegment(sketch, "E626", {"start": v(-3287.08, 31436.91) * mm, "end": v(-3334.94, 31422.43) * mm});
            skLineSegment(sketch, "E627", {"start": v(-3287.05, 31436.92) * mm, "end": v(-3072.67, 30728.66) * mm});
            skLineSegment(sketch, "E628", {"start": v(-3072.67, 30728.66) * mm, "end": v(-3101.38, 30719.96) * mm});
            skLineSegment(sketch, "E629", {"start": v(-3101.38, 30719.96) * mm, "end": v(-3315.76, 31428.23) * mm});
            skLineSegment(sketch, "E630", {"start": v(-3315.76, 31428.23) * mm, "end": v(-3287.05, 31436.92) * mm});
            skLineSegment(sketch, "E631", {"start": v(-4619.67, 35839.66) * mm, "end": v(-4463.23, 35322.82) * mm});
            skLineSegment(sketch, "E632", {"start": v(-4463.23, 35322.82) * mm, "end": v(-4491.94, 35314.13) * mm});
            skLineSegment(sketch, "E633", {"start": v(-4491.94, 35314.13) * mm, "end": v(-4648.38, 35830.97) * mm});
            skLineSegment(sketch, "E634", {"start": v(-4648.38, 35830.97) * mm, "end": v(-4619.67, 35839.66) * mm});
            skLineSegment(sketch, "E635", {"start": v(-4279.36, 34542.63) * mm, "end": v(-4273.27, 34522.53) * mm});
            skLineSegment(sketch, "E636", {"start": v(-4273.27, 34522.53) * mm, "end": v(-4242.8, 34491) * mm});
            skLineSegment(sketch, "E637", {"start": v(-4242.8, 34491) * mm, "end": v(-4214.09, 34499.7) * mm});
            skLineSegment(sketch, "E638", {"start": v(-4214.09, 34499.7) * mm, "end": v(-4231.5, 34557.12) * mm});
            skLineSegment(sketch, "E639", {"start": v(-4231.5, 34557.12) * mm, "end": v(-4279.36, 34542.63) * mm});
            skLineSegment(sketch, "E640", {"start": v(-4214.09, 34499.7) * mm, "end": v(-4057.65, 33982.85) * mm});
            skLineSegment(sketch, "E641", {"start": v(-4057.65, 33982.85) * mm, "end": v(-4086.36, 33974.16) * mm});
            skLineSegment(sketch, "E642", {"start": v(-4086.36, 33974.16) * mm, "end": v(-4242.8, 34491) * mm});
            skLineSegment(sketch, "E643", {"start": v(-4493.74, 35250.9) * mm, "end": v(-4499.82, 35271) * mm});
            skLineSegment(sketch, "E644", {"start": v(-4499.82, 35271) * mm, "end": v(-4491.94, 35314.13) * mm});
            skLineSegment(sketch, "E645", {"start": v(-4491.94, 35314.13) * mm, "end": v(-4463.23, 35322.82) * mm});
            skLineSegment(sketch, "E646", {"start": v(-4463.23, 35322.82) * mm, "end": v(-4445.88, 35265.38) * mm});
            skLineSegment(sketch, "E647", {"start": v(-4445.88, 35265.38) * mm, "end": v(-4493.74, 35250.9) * mm});
            skLineSegment(sketch, "E648", {"start": v(-4445.85, 35265.4) * mm, "end": v(-4231.47, 34557.13) * mm});
            skLineSegment(sketch, "E649", {"start": v(-4231.47, 34557.13) * mm, "end": v(-4260.18, 34548.43) * mm});
            skLineSegment(sketch, "E650", {"start": v(-4260.18, 34548.43) * mm, "end": v(-4474.56, 35256.7) * mm});
            skLineSegment(sketch, "E651", {"start": v(-4474.56, 35256.7) * mm, "end": v(-4445.85, 35265.4) * mm});
            skLineSegment(sketch, "E652", {"start": v(-153.2, 29455.34) * mm, "end": v(-21.85, 29304.52) * mm});
            skLineSegment(sketch, "E653", {"start": v(-21.85, 29304.52) * mm, "end": v(-44.47, 29284.82) * mm});
            skLineSegment(sketch, "E654", {"start": v(-44.47, 29284.82) * mm, "end": v(-136.42, 29390.4) * mm});
            skLineSegment(sketch, "E655", {"start": v(-136.42, 29390.4) * mm, "end": v(-201.37, 29373.61) * mm});
            skLineSegment(sketch, "E656", {"start": v(-201.37, 29373.61) * mm, "end": v(-221.07, 29396.23) * mm});
            skLineSegment(sketch, "E657", {"start": v(-221.07, 29396.23) * mm, "end": v(-153.2, 29455.34) * mm});
            skLineSegment(sketch, "E658", {"start": v(-21.85, 29304.52) * mm, "end": v(109.5, 29153.7) * mm});
            skLineSegment(sketch, "E659", {"start": v(109.5, 29153.7) * mm, "end": v(86.88, 29134) * mm});
            skLineSegment(sketch, "E660", {"start": v(86.88, 29134) * mm, "end": v(-5.06, 29239.58) * mm});
            skLineSegment(sketch, "E661", {"start": v(-5.06, 29239.58) * mm, "end": v(-70.01, 29222.8) * mm});
            skLineSegment(sketch, "E662", {"start": v(-70.01, 29222.8) * mm, "end": v(-89.72, 29245.41) * mm});
            skLineSegment(sketch, "E663", {"start": v(-89.72, 29245.41) * mm, "end": v(-21.85, 29304.52) * mm});
            skLineSegment(sketch, "E664", {"start": v(109.5, 29153.7) * mm, "end": v(240.86, 29002.89) * mm});
            skLineSegment(sketch, "E665", {"start": v(240.86, 29002.89) * mm, "end": v(218.24, 28983.18) * mm});
            skLineSegment(sketch, "E666", {"start": v(218.24, 28983.18) * mm, "end": v(126.29, 29088.76) * mm});
            skLineSegment(sketch, "E667", {"start": v(126.29, 29088.76) * mm, "end": v(61.34, 29071.97) * mm});
            skLineSegment(sketch, "E668", {"start": v(61.34, 29071.97) * mm, "end": v(41.64, 29094.6) * mm});
            skLineSegment(sketch, "E669", {"start": v(41.64, 29094.6) * mm, "end": v(109.5, 29153.7) * mm});
            skLineSegment(sketch, "E670", {"start": v(240.86, 29002.89) * mm, "end": v(372.21, 28852.07) * mm});
            skLineSegment(sketch, "E671", {"start": v(372.21, 28852.07) * mm, "end": v(349.6, 28832.36) * mm});
            skLineSegment(sketch, "E672", {"start": v(349.6, 28832.36) * mm, "end": v(257.64, 28937.94) * mm});
            skLineSegment(sketch, "E673", {"start": v(257.64, 28937.94) * mm, "end": v(192.7, 28921.15) * mm});
            skLineSegment(sketch, "E674", {"start": v(192.7, 28921.15) * mm, "end": v(173, 28943.78) * mm});
            skLineSegment(sketch, "E675", {"start": v(173, 28943.78) * mm, "end": v(240.86, 29002.89) * mm});
            skLineSegment(sketch, "E676", {"start": v(805.68, 28354.37) * mm, "end": v(766.27, 28399.61) * mm});
            skLineSegment(sketch, "E677", {"start": v(766.27, 28399.61) * mm, "end": v(743.65, 28379.9) * mm});
            skLineSegment(sketch, "E678", {"start": v(743.65, 28379.9) * mm, "end": v(718.1, 28317.88) * mm});
            skLineSegment(sketch, "E679", {"start": v(718.1, 28317.88) * mm, "end": v(737.81, 28295.26) * mm});
            skLineSegment(sketch, "E680", {"start": v(737.81, 28295.26) * mm, "end": v(805.68, 28354.37) * mm});
            skLineSegment(sketch, "E681", {"start": v(-746.88, 29857.19) * mm, "end": v(-689.47, 29874.62) * mm});
            skLineSegment(sketch, "E682", {"start": v(-689.47, 29874.62) * mm, "end": v(-680.75, 29845.92) * mm});
            skLineSegment(sketch, "E683", {"start": v(-680.75, 29845.92) * mm, "end": v(-703.64, 29818.06) * mm});
            skLineSegment(sketch, "E684", {"start": v(-703.64, 29818.06) * mm, "end": v(-732.35, 29809.35) * mm});
            skLineSegment(sketch, "E685", {"start": v(-732.35, 29809.35) * mm, "end": v(-746.88, 29857.19) * mm});
            skLineSegment(sketch, "E686", {"start": v(-553.53, 29915.74) * mm, "end": v(-153.14, 29455.4) * mm});
            skLineSegment(sketch, "E687", {"start": v(-153.14, 29455.4) * mm, "end": v(-175.77, 29435.7) * mm});
            skLineSegment(sketch, "E688", {"start": v(-175.77, 29435.7) * mm, "end": v(-563.4, 29881.4) * mm});
            skLineSegment(sketch, "E689", {"start": v(-563.4, 29881.4) * mm, "end": v(-553.53, 29915.74) * mm});
            skLineSegment(sketch, "E690", {"start": v(411.62, 28806.82) * mm, "end": v(766.27, 28399.61) * mm});
            skLineSegment(sketch, "E691", {"start": v(743.65, 28379.9) * mm, "end": v(389, 28787.12) * mm});
            skLineSegment(sketch, "E692", {"start": v(389, 28787.12) * mm, "end": v(411.62, 28806.82) * mm});
            skLineSegment(sketch, "E693", {"start": v(411.62, 28806.82) * mm, "end": v(372.21, 28852.07) * mm});
            skLineSegment(sketch, "E694", {"start": v(349.6, 28832.36) * mm, "end": v(324.05, 28770.34) * mm});
            skLineSegment(sketch, "E695", {"start": v(324.05, 28770.34) * mm, "end": v(343.75, 28747.71) * mm});
            skLineSegment(sketch, "E696", {"start": v(343.75, 28747.71) * mm, "end": v(411.62, 28806.82) * mm});
            skLineSegment(sketch, "E697", {"start": v(-563.49, 29881.36) * mm, "end": v(-680.75, 29845.92) * mm});
            skLineSegment(sketch, "E698", {"start": v(-680.75, 29845.92) * mm, "end": v(-689.47, 29874.62) * mm});
            skLineSegment(sketch, "E699", {"start": v(-689.47, 29874.62) * mm, "end": v(-553.62, 29915.71) * mm});
            skLineSegment(sketch, "E700", {"start": v(-553.62, 29915.71) * mm, "end": v(-563.49, 29881.36) * mm});
            skLineSegment(sketch, "E701", {"start": v(-1512.57, 29625.43) * mm, "end": v(-1455.16, 29642.86) * mm});
            skLineSegment(sketch, "E702", {"start": v(-1455.16, 29642.86) * mm, "end": v(-1446.44, 29614.16) * mm});
            skLineSegment(sketch, "E703", {"start": v(-1446.44, 29614.16) * mm, "end": v(-1469.34, 29586.3) * mm});
            skLineSegment(sketch, "E704", {"start": v(-1469.34, 29586.3) * mm, "end": v(-1498.04, 29577.59) * mm});
            skLineSegment(sketch, "E705", {"start": v(-1498.04, 29577.59) * mm, "end": v(-1512.57, 29625.43) * mm});
            skLineSegment(sketch, "E706", {"start": v(7764.12, 20360.02) * mm, "end": v(7885.67, 20220.4) * mm});
            skLineSegment(sketch, "E707", {"start": v(7885.67, 20220.4) * mm, "end": v(7875.8, 20186.04) * mm});
            skLineSegment(sketch, "E708", {"start": v(7875.8, 20186.04) * mm, "end": v(7741.5, 20340.33) * mm});
            skLineSegment(sketch, "E709", {"start": v(7741.5, 20340.33) * mm, "end": v(7764.12, 20360.02) * mm});
            skLineSegment(sketch, "E710", {"start": v(8010.52, 20226.75) * mm, "end": v(7875.85, 20185.9) * mm});
            skLineSegment(sketch, "E711", {"start": v(7875.85, 20185.9) * mm, "end": v(7885.74, 20220.31) * mm});
            skLineSegment(sketch, "E712", {"start": v(7885.74, 20220.31) * mm, "end": v(8001.8, 20255.46) * mm});
            skLineSegment(sketch, "E713", {"start": v(8001.8, 20255.46) * mm, "end": v(8010.52, 20226.75) * mm});
            skLineSegment(sketch, "E714", {"start": v(7330.78, 20857.83) * mm, "end": v(7370.16, 20812.57) * mm});
            skLineSegment(sketch, "E715", {"start": v(7370.16, 20812.57) * mm, "end": v(7347.53, 20792.88) * mm});
            skLineSegment(sketch, "E716", {"start": v(7347.53, 20792.88) * mm, "end": v(7282.58, 20776.12) * mm});
            skLineSegment(sketch, "E717", {"start": v(7282.58, 20776.12) * mm, "end": v(7262.88, 20798.76) * mm});
            skLineSegment(sketch, "E718", {"start": v(7262.88, 20798.76) * mm, "end": v(7330.78, 20857.83) * mm});
            skLineSegment(sketch, "E719", {"start": v(7702, 20385.5) * mm, "end": v(7347.53, 20792.88) * mm});
            skLineSegment(sketch, "E720", {"start": v(7347.53, 20792.88) * mm, "end": v(7370.16, 20812.57) * mm});
            skLineSegment(sketch, "E721", {"start": v(7370.16, 20812.57) * mm, "end": v(7724.62, 20405.19) * mm});
            skLineSegment(sketch, "E722", {"start": v(7724.62, 20405.19) * mm, "end": v(7702, 20385.5) * mm});
            skLineSegment(sketch, "E723", {"start": v(7724.62, 20405.19) * mm, "end": v(7764, 20359.92) * mm});
            skLineSegment(sketch, "E724", {"start": v(7764, 20359.92) * mm, "end": v(7741.38, 20340.23) * mm});
            skLineSegment(sketch, "E725", {"start": v(7741.38, 20340.23) * mm, "end": v(7676.42, 20323.48) * mm});
            skLineSegment(sketch, "E726", {"start": v(7676.42, 20323.48) * mm, "end": v(7656.73, 20346.11) * mm});
            skLineSegment(sketch, "E727", {"start": v(7656.73, 20346.11) * mm, "end": v(7724.62, 20405.19) * mm});
            skLineSegment(sketch, "E728", {"start": v(9002.11, 20506.02) * mm, "end": v(8973.4, 20497.33) * mm});
            skLineSegment(sketch, "E729", {"start": v(9150.34, 20603.13) * mm, "end": v(9164.82, 20555.27) * mm});
            skLineSegment(sketch, "E730", {"start": v(9002.11, 20506.02) * mm, "end": v(9025.03, 20533.86) * mm});
            skLineSegment(sketch, "E731", {"start": v(9025.03, 20533.86) * mm, "end": v(9159.03, 20574.42) * mm});
            skLineSegment(sketch, "E732", {"start": v(8958.91, 20545.19) * mm, "end": v(8973.4, 20497.33) * mm});
            skLineSegment(sketch, "E733", {"start": v(9341.76, 20661.07) * mm, "end": v(9350.45, 20632.36) * mm});
            skLineSegment(sketch, "E734", {"start": v(9216.45, 20591.8) * mm, "end": v(9350.45, 20632.36) * mm});
            skLineSegment(sketch, "E735", {"start": v(9193.54, 20563.96) * mm, "end": v(9216.45, 20591.8) * mm});
            skLineSegment(sketch, "E736", {"start": v(9164.82, 20555.27) * mm, "end": v(9193.54, 20563.96) * mm});
            skLineSegment(sketch, "E737", {"start": v(9341.76, 20661.07) * mm, "end": v(8059.22, 20272.87) * mm});
            skLineSegment(sketch, "E738", {"start": v(8967.6, 20516.48) * mm, "end": v(8833.6, 20475.92) * mm});
            skLineSegment(sketch, "E739", {"start": v(8810.69, 20448.08) * mm, "end": v(8833.6, 20475.92) * mm});
            skLineSegment(sketch, "E740", {"start": v(8781.97, 20439.4) * mm, "end": v(8810.69, 20448.08) * mm});
            skLineSegment(sketch, "E741", {"start": v(8767.49, 20487.25) * mm, "end": v(8781.97, 20439.4) * mm});
            skLineSegment(sketch, "E742", {"start": v(8576.07, 20429.3) * mm, "end": v(8590.55, 20381.45) * mm});
            skLineSegment(sketch, "E743", {"start": v(8067.91, 20244.16) * mm, "end": v(8584.76, 20400.6) * mm});
            skLineSegment(sketch, "E744", {"start": v(9399.2, 20678.42) * mm, "end": v(9413.68, 20630.56) * mm});
            skLineSegment(sketch, "E745", {"start": v(9384.97, 20621.87) * mm, "end": v(9413.68, 20630.56) * mm});
            skLineSegment(sketch, "E746", {"start": v(9399.2, 20678.42) * mm, "end": v(9341.76, 20661.07) * mm});
            skLineSegment(sketch, "E747", {"start": v(9350.45, 20632.36) * mm, "end": v(9384.97, 20621.87) * mm});
            skLineSegment(sketch, "E748", {"start": v(8619.26, 20390.14) * mm, "end": v(8642.18, 20417.98) * mm});
            skLineSegment(sketch, "E749", {"start": v(8590.55, 20381.45) * mm, "end": v(8619.26, 20390.14) * mm});
            skLineSegment(sketch, "E750", {"start": v(8642.18, 20417.98) * mm, "end": v(8776.18, 20458.54) * mm});
            skLineSegment(sketch, "E751", {"start": v(8016.29, 20207.6) * mm, "end": v(8001.8, 20255.46) * mm});
            skLineSegment(sketch, "E752", {"start": v(8067.91, 20244.16) * mm, "end": v(8059.22, 20272.87) * mm});
            skLineSegment(sketch, "E753", {"start": v(8045, 20216.3) * mm, "end": v(8067.91, 20244.16) * mm});
            skLineSegment(sketch, "E754", {"start": v(8016.29, 20207.6) * mm, "end": v(8045, 20216.3) * mm});
            skLineSegment(sketch, "E755", {"start": v(8059.22, 20272.87) * mm, "end": v(8001.8, 20255.46) * mm});
            skLineSegment(sketch, "E756", {"start": v(9973.47, 20852.24) * mm, "end": v(9987.95, 20804.38) * mm});
            skLineSegment(sketch, "E757", {"start": v(9916.03, 20834.89) * mm, "end": v(9973.47, 20852.24) * mm});
            skLineSegment(sketch, "E758", {"start": v(9924.72, 20806.18) * mm, "end": v(9959.24, 20795.7) * mm});
            skLineSegment(sketch, "E759", {"start": v(9959.24, 20795.7) * mm, "end": v(9987.95, 20804.38) * mm});
            skLineSegment(sketch, "E760", {"start": v(9916.03, 20834.89) * mm, "end": v(9399.19, 20678.45) * mm});
            skLineSegment(sketch, "E761", {"start": v(9924.72, 20806.18) * mm, "end": v(9916.03, 20834.89) * mm});
            skLineSegment(sketch, "E762", {"start": v(9407.88, 20649.74) * mm, "end": v(9924.72, 20806.18) * mm});
            skLineSegment(sketch, "E763", {"start": v(9399.19, 20678.45) * mm, "end": v(9407.88, 20649.74) * mm});
            skLineSegment(sketch, "E764", {"start": v(943.88, 28134.12) * mm, "end": v(907.34, 27823.05) * mm});
            skArc(sketch, "E765", {"start": v(907.34, 27823.05) * mm, "mid": v(891.7, 27809.1) * mm, "end": v(877.38, 27824.4) * mm});
            skLineSegment(sketch, "E766", {"start": v(877.38, 27824.4) * mm, "end": v(884.1, 28138.26) * mm});
            skArc(sketch, "E767", {"start": v(884.1, 28138.26) * mm, "mid": v(916.16, 28167.55) * mm, "end": v(943.88, 28134.12) * mm});
            skLineSegment(sketch, "E768", {"start": v(1318.13, 27704.2) * mm, "end": v(1281.6, 27393.13) * mm});
            skArc(sketch, "E769", {"start": v(1281.6, 27393.13) * mm, "mid": v(1265.96, 27379.18) * mm, "end": v(1251.64, 27394.49) * mm});
            skLineSegment(sketch, "E770", {"start": v(1251.64, 27394.49) * mm, "end": v(1258.34, 27708.34) * mm});
            skArc(sketch, "E771", {"start": v(1258.34, 27708.34) * mm, "mid": v(1290.41, 27737.62) * mm, "end": v(1318.13, 27704.2) * mm});
            skLineSegment(sketch, "E772", {"start": v(1692.39, 27274.27) * mm, "end": v(1655.85, 26963.2) * mm});
            skArc(sketch, "E773", {"start": v(1655.85, 26963.2) * mm, "mid": v(1640.2, 26949.26) * mm, "end": v(1625.9, 26964.56) * mm});
            skLineSegment(sketch, "E774", {"start": v(1625.9, 26964.56) * mm, "end": v(1632.6, 27278.41) * mm});
            skArc(sketch, "E775", {"start": v(1632.6, 27278.41) * mm, "mid": v(1664.66, 27307.7) * mm, "end": v(1692.39, 27274.27) * mm});
            skLineSegment(sketch, "E776", {"start": v(3570.31, 25115.21) * mm, "end": v(3533.78, 24804.15) * mm});
            skArc(sketch, "E777", {"start": v(3533.78, 24804.15) * mm, "mid": v(3518.13, 24790.2) * mm, "end": v(3503.82, 24805.5) * mm});
            skLineSegment(sketch, "E778", {"start": v(3503.82, 24805.5) * mm, "end": v(3510.52, 25119.35) * mm});
            skArc(sketch, "E779", {"start": v(3510.52, 25119.35) * mm, "mid": v(3542.59, 25148.64) * mm, "end": v(3570.31, 25115.21) * mm});
            skLineSegment(sketch, "E780", {"start": v(3944.57, 24685.3) * mm, "end": v(3908.03, 24374.23) * mm});
            skArc(sketch, "E781", {"start": v(3908.03, 24374.23) * mm, "mid": v(3892.39, 24360.28) * mm, "end": v(3878.07, 24375.58) * mm});
            skLineSegment(sketch, "E782", {"start": v(3878.07, 24375.58) * mm, "end": v(3884.78, 24689.43) * mm});
            skArc(sketch, "E783", {"start": v(3884.78, 24689.43) * mm, "mid": v(3916.84, 24718.72) * mm, "end": v(3944.57, 24685.3) * mm});
            skLineSegment(sketch, "E784", {"start": v(4318.82, 24255.37) * mm, "end": v(4282.28, 23944.3) * mm});
            skArc(sketch, "E785", {"start": v(4282.28, 23944.3) * mm, "mid": v(4266.64, 23930.35) * mm, "end": v(4252.32, 23945.66) * mm});
            skLineSegment(sketch, "E786", {"start": v(4252.32, 23945.66) * mm, "end": v(4259.03, 24259.5) * mm});
            skArc(sketch, "E787", {"start": v(4259.03, 24259.5) * mm, "mid": v(4291.1, 24288.8) * mm, "end": v(4318.82, 24255.37) * mm});
            skLineSegment(sketch, "E788", {"start": v(6197.68, 22098.83) * mm, "end": v(6161.14, 21787.76) * mm});
            skArc(sketch, "E789", {"start": v(6161.14, 21787.76) * mm, "mid": v(6145.5, 21773.81) * mm, "end": v(6131.18, 21789.12) * mm});
            skLineSegment(sketch, "E790", {"start": v(6131.18, 21789.12) * mm, "end": v(6137.9, 22102.97) * mm});
            skArc(sketch, "E791", {"start": v(6137.9, 22102.97) * mm, "mid": v(6169.96, 22132.25) * mm, "end": v(6197.68, 22098.83) * mm});
            skLineSegment(sketch, "E792", {"start": v(6571.93, 21668.9) * mm, "end": v(6535.4, 21357.84) * mm});
            skArc(sketch, "E793", {"start": v(6535.4, 21357.84) * mm, "mid": v(6519.76, 21343.89) * mm, "end": v(6505.44, 21359.2) * mm});
            skLineSegment(sketch, "E794", {"start": v(6505.44, 21359.2) * mm, "end": v(6512.15, 21673.04) * mm});
            skArc(sketch, "E795", {"start": v(6512.15, 21673.04) * mm, "mid": v(6544.21, 21702.33) * mm, "end": v(6571.93, 21668.9) * mm});
            skLineSegment(sketch, "E796", {"start": v(6946.19, 21238.98) * mm, "end": v(6909.65, 20927.92) * mm});
            skArc(sketch, "E797", {"start": v(6909.65, 20927.92) * mm, "mid": v(6894.01, 20913.97) * mm, "end": v(6879.7, 20929.27) * mm});
            skLineSegment(sketch, "E798", {"start": v(6879.7, 20929.27) * mm, "end": v(6886.4, 21243.12) * mm});
            skArc(sketch, "E799", {"start": v(6886.4, 21243.12) * mm, "mid": v(6918.47, 21272.4) * mm, "end": v(6946.19, 21238.98) * mm});
            skLineSegment(sketch, "E800", {"start": v(-1121.68, 37191.78) * mm, "end": v(-1087.16, 37181.3) * mm});
            skLineSegment(sketch, "E801", {"start": v(-1121.68, 37191.78) * mm, "end": v(-1150.4, 37183.08) * mm});
            skLineSegment(sketch, "E802", {"start": v(-1135.9, 37135.23) * mm, "end": v(-1078.47, 37152.58) * mm});
            skLineSegment(sketch, "E803", {"start": v(-1150.4, 37183.08) * mm, "end": v(-1135.9, 37135.23) * mm});
            skLineSegment(sketch, "E804", {"start": v(195.39, 37569.46) * mm, "end": v(61.39, 37528.9) * mm});
            skLineSegment(sketch, "E805", {"start": v(218.3, 37597.29) * mm, "end": v(195.39, 37569.46) * mm});
            skLineSegment(sketch, "E806", {"start": v(247.02, 37605.98) * mm, "end": v(218.3, 37597.29) * mm});
            skLineSegment(sketch, "E807", {"start": v(61.39, 37528.9) * mm, "end": v(70.08, 37500.19) * mm});
            skLineSegment(sketch, "E808", {"start": v(-512.89, 37355.1) * mm, "end": v(-504.2, 37326.38) * mm});
            skLineSegment(sketch, "E809", {"start": v(-378.89, 37395.65) * mm, "end": v(-512.89, 37355.1) * mm});
            skLineSegment(sketch, "E810", {"start": v(-355.97, 37423.48) * mm, "end": v(-378.89, 37395.65) * mm});
            skLineSegment(sketch, "E811", {"start": v(-327.25, 37432.17) * mm, "end": v(-355.97, 37423.48) * mm});
            skLineSegment(sketch, "E812", {"start": v(-312.77, 37384.32) * mm, "end": v(-327.25, 37432.17) * mm});
            skLineSegment(sketch, "E813", {"start": v(-187.46, 37453.58) * mm, "end": v(-164.54, 37481.42) * mm});
            skLineSegment(sketch, "E814", {"start": v(-187.46, 37453.58) * mm, "end": v(-321.46, 37413.03) * mm});
            skLineSegment(sketch, "E815", {"start": v(-135.83, 37490.1) * mm, "end": v(-164.54, 37481.42) * mm});
            skLineSegment(sketch, "E816", {"start": v(-121.35, 37442.25) * mm, "end": v(-135.83, 37490.1) * mm});
            skLineSegment(sketch, "E817", {"start": v(-504.2, 37326.38) * mm, "end": v(70.08, 37500.19) * mm});
            skLineSegment(sketch, "E818", {"start": v(3.96, 37511.52) * mm, "end": v(-130.04, 37470.96) * mm});
            skLineSegment(sketch, "E819", {"start": v(26.88, 37539.35) * mm, "end": v(3.96, 37511.52) * mm});
            skLineSegment(sketch, "E820", {"start": v(55.6, 37548.04) * mm, "end": v(26.88, 37539.35) * mm});
            skLineSegment(sketch, "E821", {"start": v(70.08, 37500.19) * mm, "end": v(55.6, 37548.04) * mm});
            skLineSegment(sketch, "E822", {"start": v(70.08, 37500.19) * mm, "end": v(778.35, 37714.56) * mm});
            skLineSegment(sketch, "E823", {"start": v(247.02, 37605.98) * mm, "end": v(261.5, 37558.13) * mm});
            skLineSegment(sketch, "E824", {"start": v(769.66, 37743.28) * mm, "end": v(252.81, 37586.84) * mm});
            skLineSegment(sketch, "E825", {"start": v(778.35, 37714.56) * mm, "end": v(769.66, 37743.28) * mm});
            skLineSegment(sketch, "E826", {"start": v(-512.89, 37355.1) * mm, "end": v(-547.4, 37365.58) * mm});
            skLineSegment(sketch, "E827", {"start": v(-547.4, 37365.58) * mm, "end": v(-576.12, 37356.89) * mm});
            skLineSegment(sketch, "E828", {"start": v(-561.63, 37309.03) * mm, "end": v(-504.2, 37326.38) * mm});
            skLineSegment(sketch, "E829", {"start": v(-576.12, 37356.89) * mm, "end": v(-561.62, 37309) * mm});
            skLineSegment(sketch, "E830", {"start": v(822.42, 37764.68) * mm, "end": v(828.78, 37715.1) * mm});
            skLineSegment(sketch, "E831", {"start": v(769.27, 37707.42) * mm, "end": v(765.45, 37737.18) * mm});
            skLineSegment(sketch, "E832", {"start": v(792.66, 37760.87) * mm, "end": v(765.45, 37737.18) * mm});
            skLineSegment(sketch, "E833", {"start": v(822.42, 37764.68) * mm, "end": v(792.66, 37760.87) * mm});
            skLineSegment(sketch, "E834", {"start": v(769.27, 37707.42) * mm, "end": v(828.78, 37715.1) * mm});
            skLineSegment(sketch, "E835", {"start": v(-561.62, 37309) * mm, "end": v(-1078.47, 37152.58) * mm});
            skLineSegment(sketch, "E836", {"start": v(-570.31, 37337.72) * mm, "end": v(-1087.16, 37181.3) * mm});
            skLineSegment(sketch, "E837", {"start": v(-1087.16, 37181.3) * mm, "end": v(-1078.47, 37152.58) * mm});
            skLineSegment(sketch, "E838", {"start": v(5098.23, 23421.94) * mm, "end": v(5229.58, 23271.12) * mm});
            skLineSegment(sketch, "E839", {"start": v(5229.58, 23271.12) * mm, "end": v(5206.96, 23251.42) * mm});
            skLineSegment(sketch, "E840", {"start": v(5206.96, 23251.42) * mm, "end": v(5115, 23357) * mm});
            skLineSegment(sketch, "E841", {"start": v(5115, 23357) * mm, "end": v(5050.06, 23340.2) * mm});
            skLineSegment(sketch, "E842", {"start": v(5050.06, 23340.2) * mm, "end": v(5030.36, 23362.83) * mm});
            skLineSegment(sketch, "E843", {"start": v(5030.36, 23362.83) * mm, "end": v(5098.23, 23421.94) * mm});
            skLineSegment(sketch, "E844", {"start": v(5229.58, 23271.12) * mm, "end": v(5360.93, 23120.3) * mm});
            skLineSegment(sketch, "E845", {"start": v(5360.93, 23120.3) * mm, "end": v(5338.31, 23100.6) * mm});
            skLineSegment(sketch, "E846", {"start": v(5338.31, 23100.6) * mm, "end": v(5246.36, 23206.17) * mm});
            skLineSegment(sketch, "E847", {"start": v(5246.36, 23206.17) * mm, "end": v(5181.41, 23189.39) * mm});
            skLineSegment(sketch, "E848", {"start": v(5181.41, 23189.39) * mm, "end": v(5161.71, 23212.01) * mm});
            skLineSegment(sketch, "E849", {"start": v(5161.71, 23212.01) * mm, "end": v(5229.58, 23271.12) * mm});
            skLineSegment(sketch, "E850", {"start": v(5360.93, 23120.3) * mm, "end": v(5492.29, 22969.48) * mm});
            skLineSegment(sketch, "E851", {"start": v(5492.29, 22969.48) * mm, "end": v(5469.66, 22949.78) * mm});
            skLineSegment(sketch, "E852", {"start": v(5469.66, 22949.78) * mm, "end": v(5377.72, 23055.35) * mm});
            skLineSegment(sketch, "E853", {"start": v(5377.72, 23055.35) * mm, "end": v(5312.77, 23038.57) * mm});
            skLineSegment(sketch, "E854", {"start": v(5312.77, 23038.57) * mm, "end": v(5293.07, 23061.2) * mm});
            skLineSegment(sketch, "E855", {"start": v(5293.07, 23061.2) * mm, "end": v(5360.93, 23120.3) * mm});
            skLineSegment(sketch, "E856", {"start": v(5492.29, 22969.48) * mm, "end": v(5623.64, 22818.66) * mm});
            skLineSegment(sketch, "E857", {"start": v(5623.64, 22818.66) * mm, "end": v(5601.02, 22798.96) * mm});
            skLineSegment(sketch, "E858", {"start": v(5601.02, 22798.96) * mm, "end": v(5509.07, 22904.53) * mm});
            skLineSegment(sketch, "E859", {"start": v(5509.07, 22904.53) * mm, "end": v(5444.12, 22887.75) * mm});
            skLineSegment(sketch, "E860", {"start": v(5444.12, 22887.75) * mm, "end": v(5424.42, 22910.37) * mm});
            skLineSegment(sketch, "E861", {"start": v(5424.42, 22910.37) * mm, "end": v(5492.29, 22969.48) * mm});
            skLineSegment(sketch, "E862", {"start": v(4703.9, 23874.71) * mm, "end": v(4743.3, 23829.47) * mm});
            skLineSegment(sketch, "E863", {"start": v(4743.3, 23829.47) * mm, "end": v(4720.67, 23809.76) * mm});
            skLineSegment(sketch, "E864", {"start": v(4720.67, 23809.76) * mm, "end": v(4655.73, 23792.98) * mm});
            skLineSegment(sketch, "E865", {"start": v(4655.73, 23792.98) * mm, "end": v(4636.02, 23815.6) * mm});
            skLineSegment(sketch, "E866", {"start": v(4636.02, 23815.6) * mm, "end": v(4703.9, 23874.71) * mm});
            skLineSegment(sketch, "E867", {"start": v(5097.95, 23422.26) * mm, "end": v(4743.3, 23829.47) * mm});
            skLineSegment(sketch, "E868", {"start": v(4720.67, 23809.76) * mm, "end": v(5075.33, 23402.55) * mm});
            skLineSegment(sketch, "E869", {"start": v(5075.33, 23402.55) * mm, "end": v(5097.95, 23422.26) * mm});
            skLineSegment(sketch, "E870", {"start": v(5663.05, 22773.42) * mm, "end": v(5623.64, 22818.66) * mm});
            skLineSegment(sketch, "E871", {"start": v(5601.02, 22798.96) * mm, "end": v(5575.48, 22736.93) * mm});
            skLineSegment(sketch, "E872", {"start": v(5575.48, 22736.93) * mm, "end": v(5595.18, 22714.31) * mm});
            skLineSegment(sketch, "E873", {"start": v(5595.18, 22714.31) * mm, "end": v(5663.05, 22773.42) * mm});
            skLineSegment(sketch, "E874", {"start": v(6057.1, 22320.96) * mm, "end": v(6017.7, 22366.2) * mm});
            skLineSegment(sketch, "E875", {"start": v(6017.7, 22366.2) * mm, "end": v(5995.08, 22346.5) * mm});
            skLineSegment(sketch, "E876", {"start": v(5995.08, 22346.5) * mm, "end": v(5969.54, 22284.48) * mm});
            skLineSegment(sketch, "E877", {"start": v(5969.54, 22284.48) * mm, "end": v(5989.24, 22261.85) * mm});
            skLineSegment(sketch, "E878", {"start": v(5989.24, 22261.85) * mm, "end": v(6057.1, 22320.96) * mm});
            skLineSegment(sketch, "E879", {"start": v(5640.42, 22753.72) * mm, "end": v(5995.08, 22346.5) * mm});
            skLineSegment(sketch, "E880", {"start": v(5995.08, 22346.5) * mm, "end": v(6017.7, 22366.2) * mm});
            skLineSegment(sketch, "E881", {"start": v(6017.7, 22366.2) * mm, "end": v(5663.05, 22773.42) * mm});
            skLineSegment(sketch, "E882", {"start": v(5663.05, 22773.42) * mm, "end": v(5640.42, 22753.72) * mm});
            skLineSegment(sketch, "E883", {"start": v(734.23, 37775.9) * mm, "end": v(-5053.62, 37031.65) * mm});
            skLineSegment(sketch, "E884", {"start": v(-5053.62, 37031.65) * mm, "end": v(-4774.2, 36107.06) * mm});
            skLineSegment(sketch, "E885", {"start": v(7601.46, 21020.54) * mm, "end": v(7988.18, 20576.3) * mm});
            skLineSegment(sketch, "E886", {"start": v(7610.89, 21028.75) * mm, "end": v(7992.3, 20590.6) * mm});
            skLineSegment(sketch, "E887", {"start": v(7588.64, 21009.38) * mm, "end": v(7982.58, 20556.84) * mm});
            skLineSegment(sketch, "E888", {"start": v(7513.21, 20943.72) * mm, "end": v(7949.63, 20442.39) * mm});
            skLineSegment(sketch, "E889", {"start": v(7501.9, 20933.87) * mm, "end": v(7944.69, 20425.22) * mm});
            skLineSegment(sketch, "E890", {"start": v(7426.47, 20868.21) * mm, "end": v(7911.74, 20310.77) * mm});
            skLineSegment(sketch, "E891", {"start": v(7366.89, 20816.34) * mm, "end": v(7885.71, 20220.35) * mm});
            skLineSegment(sketch, "E892", {"start": v(7620.32, 21036.96) * mm, "end": v(7996.42, 20604.91) * mm});
            skLineSegment(sketch, "E893", {"start": v(4984.65, 24045.64) * mm, "end": v(6264.89, 22574.96) * mm});
            skLineSegment(sketch, "E894", {"start": v(4994.07, 24053.84) * mm, "end": v(6274.31, 22583.17) * mm});
            skLineSegment(sketch, "E895", {"start": v(4975.22, 24037.43) * mm, "end": v(6255.46, 22566.76) * mm});
            skLineSegment(sketch, "E896", {"start": v(4962.4, 24026.27) * mm, "end": v(6242.64, 22555.6) * mm});
            skLineSegment(sketch, "E897", {"start": v(4886.97, 23960.6) * mm, "end": v(6167.21, 22489.94) * mm});
            skLineSegment(sketch, "E898", {"start": v(4875.66, 23950.76) * mm, "end": v(6155.9, 22480.09) * mm});
            skLineSegment(sketch, "E899", {"start": v(4800.23, 23885.1) * mm, "end": v(6080.47, 22414.43) * mm});
            skLineSegment(sketch, "E900", {"start": v(4740.65, 23833.23) * mm, "end": v(6020.89, 22362.56) * mm});
            skLineSegment(sketch, "E901", {"start": v(6020.89, 22362.56) * mm, "end": v(6274.31, 22583.17) * mm});
            skLineSegment(sketch, "E902", {"start": v(7366.89, 20816.34) * mm, "end": v(7620.32, 21036.96) * mm});
            skLineSegment(sketch, "E903", {"start": v(2359.12, 27061.7) * mm, "end": v(3638.65, 25591.85) * mm});
            skLineSegment(sketch, "E904", {"start": v(2368.55, 27069.9) * mm, "end": v(3648.07, 25600.06) * mm});
            skLineSegment(sketch, "E905", {"start": v(2349.7, 27053.5) * mm, "end": v(3629.22, 25583.65) * mm});
            skLineSegment(sketch, "E906", {"start": v(2336.87, 27042.33) * mm, "end": v(3616.4, 25572.48) * mm});
            skLineSegment(sketch, "E907", {"start": v(2261.45, 26976.67) * mm, "end": v(3540.97, 25506.83) * mm});
            skLineSegment(sketch, "E908", {"start": v(2250.14, 26966.82) * mm, "end": v(3529.66, 25496.98) * mm});
            skLineSegment(sketch, "E909", {"start": v(2174.71, 26901.16) * mm, "end": v(3454.23, 25431.32) * mm});
            skLineSegment(sketch, "E910", {"start": v(2115.12, 26849.3) * mm, "end": v(3394.65, 25379.45) * mm});
            skLineSegment(sketch, "E911", {"start": v(3394.65, 25379.45) * mm, "end": v(3648.07, 25600.06) * mm});
            skLineSegment(sketch, "E912", {"start": v(4740.65, 23833.23) * mm, "end": v(4994.07, 24053.84) * mm});
            skLineSegment(sketch, "E913", {"start": v(-448.47, 30286.92) * mm, "end": v(1013.12, 28607.92) * mm});
            skLineSegment(sketch, "E914", {"start": v(-444.35, 30301.23) * mm, "end": v(1022.55, 28616.12) * mm});
            skLineSegment(sketch, "E915", {"start": v(-452.6, 30272.61) * mm, "end": v(1003.7, 28599.7) * mm});
            skLineSegment(sketch, "E916", {"start": v(-458.2, 30253.16) * mm, "end": v(990.87, 28588.55) * mm});
            skLineSegment(sketch, "E917", {"start": v(-491.14, 30138.7) * mm, "end": v(915.45, 28522.89) * mm});
            skLineSegment(sketch, "E918", {"start": v(-496.08, 30121.54) * mm, "end": v(904.13, 28513.04) * mm});
            skLineSegment(sketch, "E919", {"start": v(-529.03, 30007.08) * mm, "end": v(828.7, 28447.38) * mm});
            skLineSegment(sketch, "E920", {"start": v(-555.06, 29916.66) * mm, "end": v(769.12, 28395.5) * mm});
            skLineSegment(sketch, "E921", {"start": v(769.12, 28395.5) * mm, "end": v(1022.55, 28616.12) * mm});
            skLineSegment(sketch, "E922", {"start": v(2115.12, 26849.3) * mm, "end": v(2368.55, 27069.9) * mm});
            skLineSegment(sketch, "E923", {"start": v(7083.78, 21255.34) * mm, "end": v(7335.9, 20965.7) * mm});
            skLineSegment(sketch, "E924", {"start": v(7335.9, 20965.7) * mm, "end": v(7313.28, 20946) * mm});
            skLineSegment(sketch, "E925", {"start": v(7313.28, 20946) * mm, "end": v(7061.15, 21235.64) * mm});
            skLineSegment(sketch, "E926", {"start": v(7061.15, 21235.64) * mm, "end": v(7083.78, 21255.34) * mm});
            skLineSegment(sketch, "E927", {"start": v(6100.48, 22365.56) * mm, "end": v(6986.87, 21347.32) * mm});
            skLineSegment(sketch, "E928", {"start": v(6986.87, 21347.32) * mm, "end": v(6964.24, 21327.62) * mm});
            skLineSegment(sketch, "E929", {"start": v(6964.24, 21327.62) * mm, "end": v(6077.85, 22345.86) * mm});
            skLineSegment(sketch, "E930", {"start": v(6077.85, 22345.86) * mm, "end": v(6100.48, 22365.56) * mm});
            skLineSegment(sketch, "E931", {"start": v(7402.9, 20957.74) * mm, "end": v(7236.23, 21424.78) * mm});
            skLineSegment(sketch, "E932", {"start": v(7116.22, 21459.92) * mm, "end": v(7149.05, 21422.2) * mm});
            skLineSegment(sketch, "E933", {"start": v(7149.05, 21422.2) * mm, "end": v(6997.07, 21289.9) * mm});
            skLineSegment(sketch, "E934", {"start": v(6997.07, 21289.9) * mm, "end": v(6964.24, 21327.62) * mm});
            skLineSegment(sketch, "E935", {"start": v(6964.24, 21327.62) * mm, "end": v(7116.22, 21459.92) * mm});
            skLineSegment(sketch, "E936", {"start": v(7083.8, 21324.3) * mm, "end": v(7079.27, 21320.36) * mm});
            skLineSegment(sketch, "E937", {"start": v(7079.27, 21320.36) * mm, "end": v(7058.92, 21343.75) * mm});
            skLineSegment(sketch, "E938", {"start": v(7058.92, 21343.75) * mm, "end": v(6997.07, 21289.9) * mm});
            skLineSegment(sketch, "E939", {"start": v(6997.07, 21289.9) * mm, "end": v(7051.57, 21227.3) * mm});
            skLineSegment(sketch, "E940", {"start": v(7051.57, 21227.3) * mm, "end": v(7117.94, 21285.08) * mm});
            skLineSegment(sketch, "E941", {"start": v(7117.94, 21285.08) * mm, "end": v(7083.8, 21324.3) * mm});
            skLineSegment(sketch, "E942", {"start": v(6964.24, 21327.62) * mm, "end": v(6997.07, 21289.9) * mm});
            skLineSegment(sketch, "E943", {"start": v(6997.07, 21289.9) * mm, "end": v(6972.94, 21268.9) * mm});
            skLineSegment(sketch, "E944", {"start": v(6972.94, 21268.9) * mm, "end": v(6940.1, 21306.6) * mm});
            skLineSegment(sketch, "E945", {"start": v(6940.1, 21306.6) * mm, "end": v(6964.24, 21327.62) * mm});
            skLineSegment(sketch, "E946", {"start": v(7420.04, 20928.9) * mm, "end": v(7398.38, 20953.8) * mm});
            skLineSegment(sketch, "E947", {"start": v(7398.38, 20953.8) * mm, "end": v(7402.9, 20957.74) * mm});
            skLineSegment(sketch, "E948", {"start": v(7402.9, 20957.74) * mm, "end": v(7370.07, 20995.45) * mm});
            skLineSegment(sketch, "E949", {"start": v(7370.07, 20995.45) * mm, "end": v(7303.7, 20937.67) * mm});
            skLineSegment(sketch, "E950", {"start": v(7303.7, 20937.67) * mm, "end": v(7358.2, 20875.07) * mm});
            skLineSegment(sketch, "E951", {"start": v(7358.2, 20875.07) * mm, "end": v(7420.04, 20928.9) * mm});
            skLineSegment(sketch, "E952", {"start": v(7510.18, 21007.37) * mm, "end": v(7543, 20969.66) * mm});
            skLineSegment(sketch, "E953", {"start": v(7543, 20969.66) * mm, "end": v(7391.02, 20837.35) * mm});
            skLineSegment(sketch, "E954", {"start": v(7391.02, 20837.35) * mm, "end": v(7358.2, 20875.07) * mm});
            skLineSegment(sketch, "E955", {"start": v(7358.2, 20875.07) * mm, "end": v(7510.18, 21007.37) * mm});
            skLineSegment(sketch, "E956", {"start": v(7358.2, 20875.07) * mm, "end": v(7391.02, 20837.35) * mm});
            skLineSegment(sketch, "E957", {"start": v(7391.02, 20837.35) * mm, "end": v(7366.89, 20816.34) * mm});
            skLineSegment(sketch, "E958", {"start": v(7366.89, 20816.34) * mm, "end": v(7334.06, 20854.06) * mm});
            skLineSegment(sketch, "E959", {"start": v(7334.06, 20854.06) * mm, "end": v(7358.2, 20875.07) * mm});
            skLineSegment(sketch, "E960", {"start": v(6197, 22515.87) * mm, "end": v(6229.83, 22478.16) * mm});
            skLineSegment(sketch, "E961", {"start": v(6229.83, 22478.16) * mm, "end": v(6077.85, 22345.86) * mm});
            skLineSegment(sketch, "E962", {"start": v(6077.85, 22345.86) * mm, "end": v(6045.02, 22383.57) * mm});
            skLineSegment(sketch, "E963", {"start": v(6045.02, 22383.57) * mm, "end": v(6197, 22515.87) * mm});
            skLineSegment(sketch, "E964", {"start": v(6045.02, 22383.57) * mm, "end": v(6077.85, 22345.86) * mm});
            skLineSegment(sketch, "E965", {"start": v(6077.85, 22345.86) * mm, "end": v(6053.72, 22324.85) * mm});
            skLineSegment(sketch, "E966", {"start": v(6053.72, 22324.85) * mm, "end": v(6020.89, 22362.56) * mm});
            skLineSegment(sketch, "E967", {"start": v(6020.89, 22362.56) * mm, "end": v(6045.02, 22383.57) * mm});
            skArc(sketch, "E968", {"start": v(7236.23, 21424.78) * mm, "mid": v(7156.66, 21379.64) * mm, "end": v(7083.8, 21324.3) * mm});
            skLineSegment(sketch, "E969", {"start": v(6273.1, 22565.54) * mm, "end": v(6205.21, 22506.44) * mm});
            skLineSegment(sketch, "E970", {"start": v(6290.73, 22564.32) * mm, "end": v(6213.42, 22497.02) * mm});
            skLineSegment(sketch, "E971", {"start": v(6274.31, 22583.17) * mm, "end": v(6197, 22515.87) * mm});
            skLineSegment(sketch, "E972", {"start": v(6273.1, 22565.54) * mm, "end": v(6264.89, 22574.96) * mm});
            skLineSegment(sketch, "E973", {"start": v(6274.31, 22583.17) * mm, "end": v(6290.73, 22564.32) * mm});
            skLineSegment(sketch, "E974", {"start": v(7534.8, 20979.09) * mm, "end": v(7602.68, 21038.18) * mm});
            skLineSegment(sketch, "E975", {"start": v(7526.6, 20988.51) * mm, "end": v(7603.9, 21055.81) * mm});
            skLineSegment(sketch, "E976", {"start": v(7543, 20969.66) * mm, "end": v(7620.32, 21036.96) * mm});
            skLineSegment(sketch, "E977", {"start": v(7602.68, 21038.18) * mm, "end": v(7610.89, 21028.75) * mm});
            skLineSegment(sketch, "E978", {"start": v(7620.32, 21036.96) * mm, "end": v(7603.9, 21055.81) * mm});
            skLineSegment(sketch, "E979", {"start": v(6229.83, 22478.16) * mm, "end": v(7510.18, 21007.37) * mm});
            skLineSegment(sketch, "E980", {"start": v(7334.17, 20854.15) * mm, "end": v(6053.82, 22324.94) * mm});
            skLineSegment(sketch, "E981", {"start": v(4457.53, 24272.23) * mm, "end": v(4709.66, 23982.6) * mm});
            skLineSegment(sketch, "E982", {"start": v(4709.66, 23982.6) * mm, "end": v(4687.04, 23962.9) * mm});
            skLineSegment(sketch, "E983", {"start": v(4687.04, 23962.9) * mm, "end": v(4434.9, 24252.53) * mm});
            skLineSegment(sketch, "E984", {"start": v(4434.9, 24252.53) * mm, "end": v(4457.53, 24272.23) * mm});
            skLineSegment(sketch, "E985", {"start": v(3474.24, 25382.44) * mm, "end": v(4360.63, 24364.2) * mm});
            skLineSegment(sketch, "E986", {"start": v(4360.63, 24364.2) * mm, "end": v(4338, 24344.5) * mm});
            skLineSegment(sketch, "E987", {"start": v(4338, 24344.5) * mm, "end": v(3451.61, 25362.75) * mm});
            skLineSegment(sketch, "E988", {"start": v(3451.61, 25362.75) * mm, "end": v(3474.24, 25382.44) * mm});
            skLineSegment(sketch, "E989", {"start": v(4776.66, 23974.63) * mm, "end": v(4609.98, 24441.67) * mm});
            skLineSegment(sketch, "E990", {"start": v(4489.98, 24476.8) * mm, "end": v(4522.81, 24439.1) * mm});
            skLineSegment(sketch, "E991", {"start": v(4522.81, 24439.1) * mm, "end": v(4370.83, 24306.8) * mm});
            skLineSegment(sketch, "E992", {"start": v(4370.83, 24306.8) * mm, "end": v(4338, 24344.5) * mm});
            skLineSegment(sketch, "E993", {"start": v(4338, 24344.5) * mm, "end": v(4489.98, 24476.8) * mm});
            skLineSegment(sketch, "E994", {"start": v(4457.56, 24341.2) * mm, "end": v(4453.03, 24337.25) * mm});
            skLineSegment(sketch, "E995", {"start": v(4453.03, 24337.25) * mm, "end": v(4432.68, 24360.63) * mm});
            skLineSegment(sketch, "E996", {"start": v(4432.68, 24360.63) * mm, "end": v(4370.83, 24306.8) * mm});
            skLineSegment(sketch, "E997", {"start": v(4370.83, 24306.8) * mm, "end": v(4425.33, 24244.2) * mm});
            skLineSegment(sketch, "E998", {"start": v(4425.33, 24244.2) * mm, "end": v(4491.7, 24301.97) * mm});
            skLineSegment(sketch, "E999", {"start": v(4491.7, 24301.97) * mm, "end": v(4457.56, 24341.2) * mm});
            skLineSegment(sketch, "E1000", {"start": v(4338, 24344.5) * mm, "end": v(4370.83, 24306.8) * mm});
            skLineSegment(sketch, "E1001", {"start": v(4370.83, 24306.8) * mm, "end": v(4346.7, 24285.78) * mm});
            skLineSegment(sketch, "E1002", {"start": v(4346.7, 24285.78) * mm, "end": v(4313.87, 24323.5) * mm});
            skLineSegment(sketch, "E1003", {"start": v(4313.87, 24323.5) * mm, "end": v(4338, 24344.5) * mm});
            skLineSegment(sketch, "E1004", {"start": v(4793.8, 23945.8) * mm, "end": v(4772.13, 23970.69) * mm});
            skLineSegment(sketch, "E1005", {"start": v(4772.13, 23970.69) * mm, "end": v(4776.66, 23974.63) * mm});
            skLineSegment(sketch, "E1006", {"start": v(4776.66, 23974.63) * mm, "end": v(4743.83, 24012.34) * mm});
            skLineSegment(sketch, "E1007", {"start": v(4743.83, 24012.34) * mm, "end": v(4677.46, 23954.56) * mm});
            skLineSegment(sketch, "E1008", {"start": v(4677.46, 23954.56) * mm, "end": v(4731.95, 23891.96) * mm});
            skLineSegment(sketch, "E1009", {"start": v(4731.95, 23891.96) * mm, "end": v(4793.8, 23945.8) * mm});
            skLineSegment(sketch, "E1010", {"start": v(4883.94, 24024.26) * mm, "end": v(4916.76, 23986.55) * mm});
            skLineSegment(sketch, "E1011", {"start": v(4916.76, 23986.55) * mm, "end": v(4764.78, 23854.24) * mm});
            skLineSegment(sketch, "E1012", {"start": v(4764.78, 23854.24) * mm, "end": v(4731.95, 23891.96) * mm});
            skLineSegment(sketch, "E1013", {"start": v(4731.95, 23891.96) * mm, "end": v(4883.94, 24024.26) * mm});
            skLineSegment(sketch, "E1014", {"start": v(4731.95, 23891.96) * mm, "end": v(4764.78, 23854.24) * mm});
            skLineSegment(sketch, "E1015", {"start": v(4764.78, 23854.24) * mm, "end": v(4740.65, 23833.23) * mm});
            skLineSegment(sketch, "E1016", {"start": v(4740.65, 23833.23) * mm, "end": v(4707.82, 23870.94) * mm});
            skLineSegment(sketch, "E1017", {"start": v(4707.82, 23870.94) * mm, "end": v(4731.95, 23891.96) * mm});
            skLineSegment(sketch, "E1018", {"start": v(3570.76, 25532.76) * mm, "end": v(3603.6, 25495.05) * mm});
            skLineSegment(sketch, "E1019", {"start": v(3603.6, 25495.05) * mm, "end": v(3451.61, 25362.75) * mm});
            skLineSegment(sketch, "E1020", {"start": v(3451.61, 25362.75) * mm, "end": v(3418.78, 25400.46) * mm});
            skLineSegment(sketch, "E1021", {"start": v(3418.78, 25400.46) * mm, "end": v(3570.76, 25532.76) * mm});
            skLineSegment(sketch, "E1022", {"start": v(3418.78, 25400.46) * mm, "end": v(3451.61, 25362.75) * mm});
            skLineSegment(sketch, "E1023", {"start": v(3451.61, 25362.75) * mm, "end": v(3427.47, 25341.73) * mm});
            skLineSegment(sketch, "E1024", {"start": v(3427.47, 25341.73) * mm, "end": v(3394.65, 25379.45) * mm});
            skLineSegment(sketch, "E1025", {"start": v(3394.65, 25379.45) * mm, "end": v(3418.78, 25400.46) * mm});
            skArc(sketch, "E1026", {"start": v(4609.98, 24441.67) * mm, "mid": v(4530.41, 24396.52) * mm, "end": v(4457.56, 24341.2) * mm});
            skLineSegment(sketch, "E1027", {"start": v(3646.85, 25582.42) * mm, "end": v(3578.97, 25523.33) * mm});
            skLineSegment(sketch, "E1028", {"start": v(3664.49, 25581.2) * mm, "end": v(3587.18, 25513.9) * mm});
            skLineSegment(sketch, "E1029", {"start": v(3648.07, 25600.06) * mm, "end": v(3570.76, 25532.76) * mm});
            skLineSegment(sketch, "E1030", {"start": v(3646.85, 25582.42) * mm, "end": v(3638.65, 25591.85) * mm});
            skLineSegment(sketch, "E1031", {"start": v(3648.07, 25600.06) * mm, "end": v(3664.49, 25581.2) * mm});
            skLineSegment(sketch, "E1032", {"start": v(4908.56, 23995.97) * mm, "end": v(4976.44, 24055.07) * mm});
            skLineSegment(sketch, "E1033", {"start": v(4900.35, 24005.4) * mm, "end": v(4977.66, 24072.7) * mm});
            skLineSegment(sketch, "E1034", {"start": v(4916.76, 23986.55) * mm, "end": v(4994.08, 24053.85) * mm});
            skLineSegment(sketch, "E1035", {"start": v(4976.44, 24055.07) * mm, "end": v(4984.65, 24045.64) * mm});
            skLineSegment(sketch, "E1036", {"start": v(4994.08, 24053.85) * mm, "end": v(4977.66, 24072.7) * mm});
            skLineSegment(sketch, "E1037", {"start": v(3603.6, 25495.05) * mm, "end": v(4883.94, 24024.26) * mm});
            skLineSegment(sketch, "E1038", {"start": v(4707.93, 23871.04) * mm, "end": v(3427.58, 25341.83) * mm});
            skLineSegment(sketch, "E1039", {"start": v(1832.01, 27288.29) * mm, "end": v(2084.14, 26998.66) * mm});
            skLineSegment(sketch, "E1040", {"start": v(2084.14, 26998.66) * mm, "end": v(2061.51, 26978.96) * mm});
            skLineSegment(sketch, "E1041", {"start": v(2061.51, 26978.96) * mm, "end": v(1809.38, 27268.6) * mm});
            skLineSegment(sketch, "E1042", {"start": v(1809.38, 27268.6) * mm, "end": v(1832.01, 27288.29) * mm});
            skLineSegment(sketch, "E1043", {"start": v(848.72, 28398.5) * mm, "end": v(1735.1, 27380.27) * mm});
            skLineSegment(sketch, "E1044", {"start": v(1735.1, 27380.27) * mm, "end": v(1712.48, 27360.57) * mm});
            skLineSegment(sketch, "E1045", {"start": v(1712.48, 27360.57) * mm, "end": v(826.09, 28378.8) * mm});
            skLineSegment(sketch, "E1046", {"start": v(826.09, 28378.8) * mm, "end": v(848.72, 28398.5) * mm});
            skLineSegment(sketch, "E1047", {"start": v(2151.14, 26990.69) * mm, "end": v(1984.46, 27457.73) * mm});
            skLineSegment(sketch, "E1048", {"start": v(1864.46, 27492.87) * mm, "end": v(1897.3, 27455.16) * mm});
            skLineSegment(sketch, "E1049", {"start": v(1897.3, 27455.16) * mm, "end": v(1745.3, 27322.86) * mm});
            skLineSegment(sketch, "E1050", {"start": v(1745.3, 27322.86) * mm, "end": v(1712.48, 27360.57) * mm});
            skLineSegment(sketch, "E1051", {"start": v(1712.48, 27360.57) * mm, "end": v(1864.46, 27492.87) * mm});
            skLineSegment(sketch, "E1052", {"start": v(1832.04, 27357.25) * mm, "end": v(1827.51, 27353.31) * mm});
            skLineSegment(sketch, "E1053", {"start": v(1827.51, 27353.31) * mm, "end": v(1807.16, 27376.7) * mm});
            skLineSegment(sketch, "E1054", {"start": v(1807.16, 27376.7) * mm, "end": v(1745.3, 27322.86) * mm});
            skLineSegment(sketch, "E1055", {"start": v(1745.3, 27322.86) * mm, "end": v(1799.8, 27260.25) * mm});
            skLineSegment(sketch, "E1056", {"start": v(1799.8, 27260.25) * mm, "end": v(1866.18, 27318.03) * mm});
            skLineSegment(sketch, "E1057", {"start": v(1866.18, 27318.03) * mm, "end": v(1832.04, 27357.25) * mm});
            skLineSegment(sketch, "E1058", {"start": v(1712.48, 27360.57) * mm, "end": v(1745.3, 27322.86) * mm});
            skLineSegment(sketch, "E1059", {"start": v(1745.3, 27322.86) * mm, "end": v(1721.17, 27301.85) * mm});
            skLineSegment(sketch, "E1060", {"start": v(1721.17, 27301.85) * mm, "end": v(1688.34, 27339.56) * mm});
            skLineSegment(sketch, "E1061", {"start": v(1688.34, 27339.56) * mm, "end": v(1712.48, 27360.57) * mm});
            skLineSegment(sketch, "E1062", {"start": v(2168.28, 26961.86) * mm, "end": v(2146.61, 26986.75) * mm});
            skLineSegment(sketch, "E1063", {"start": v(2146.61, 26986.75) * mm, "end": v(2151.14, 26990.69) * mm});
            skLineSegment(sketch, "E1064", {"start": v(2151.14, 26990.69) * mm, "end": v(2118.3, 27028.4) * mm});
            skLineSegment(sketch, "E1065", {"start": v(2118.3, 27028.4) * mm, "end": v(2051.93, 26970.62) * mm});
            skLineSegment(sketch, "E1066", {"start": v(2051.93, 26970.62) * mm, "end": v(2106.43, 26908.02) * mm});
            skLineSegment(sketch, "E1067", {"start": v(2106.43, 26908.02) * mm, "end": v(2168.28, 26961.86) * mm});
            skLineSegment(sketch, "E1068", {"start": v(2258.41, 27040.32) * mm, "end": v(2291.24, 27002.6) * mm});
            skLineSegment(sketch, "E1069", {"start": v(2291.24, 27002.6) * mm, "end": v(2139.26, 26870.3) * mm});
            skLineSegment(sketch, "E1070", {"start": v(2139.26, 26870.3) * mm, "end": v(2106.43, 26908.02) * mm});
            skLineSegment(sketch, "E1071", {"start": v(2106.43, 26908.02) * mm, "end": v(2258.41, 27040.32) * mm});
            skLineSegment(sketch, "E1072", {"start": v(2106.43, 26908.02) * mm, "end": v(2139.26, 26870.3) * mm});
            skLineSegment(sketch, "E1073", {"start": v(2139.26, 26870.3) * mm, "end": v(2115.12, 26849.3) * mm});
            skLineSegment(sketch, "E1074", {"start": v(2115.12, 26849.3) * mm, "end": v(2082.3, 26887) * mm});
            skLineSegment(sketch, "E1075", {"start": v(2082.3, 26887) * mm, "end": v(2106.43, 26908.02) * mm});
            skLineSegment(sketch, "E1076", {"start": v(945.24, 28548.82) * mm, "end": v(978.07, 28511.1) * mm});
            skLineSegment(sketch, "E1077", {"start": v(978.07, 28511.1) * mm, "end": v(826.09, 28378.8) * mm});
            skLineSegment(sketch, "E1078", {"start": v(826.09, 28378.8) * mm, "end": v(793.26, 28416.52) * mm});
            skLineSegment(sketch, "E1079", {"start": v(793.26, 28416.52) * mm, "end": v(945.24, 28548.82) * mm});
            skLineSegment(sketch, "E1080", {"start": v(793.26, 28416.52) * mm, "end": v(826.09, 28378.8) * mm});
            skLineSegment(sketch, "E1081", {"start": v(826.09, 28378.8) * mm, "end": v(801.95, 28357.8) * mm});
            skLineSegment(sketch, "E1082", {"start": v(801.95, 28357.8) * mm, "end": v(769.12, 28395.5) * mm});
            skLineSegment(sketch, "E1083", {"start": v(769.12, 28395.5) * mm, "end": v(793.26, 28416.52) * mm});
            skArc(sketch, "E1084", {"start": v(1984.46, 27457.73) * mm, "mid": v(1904.9, 27412.59) * mm, "end": v(1832.04, 27357.25) * mm});
            skLineSegment(sketch, "E1085", {"start": v(1021.33, 28598.49) * mm, "end": v(953.45, 28539.4) * mm});
            skLineSegment(sketch, "E1086", {"start": v(1038.97, 28597.27) * mm, "end": v(961.66, 28529.97) * mm});
            skLineSegment(sketch, "E1087", {"start": v(1022.55, 28616.12) * mm, "end": v(945.24, 28548.82) * mm});
            skLineSegment(sketch, "E1088", {"start": v(1021.33, 28598.49) * mm, "end": v(1013.12, 28607.92) * mm});
            skLineSegment(sketch, "E1089", {"start": v(1022.55, 28616.12) * mm, "end": v(1038.97, 28597.27) * mm});
            skLineSegment(sketch, "E1090", {"start": v(2283.04, 27012.04) * mm, "end": v(2350.92, 27071.13) * mm});
            skLineSegment(sketch, "E1091", {"start": v(2274.83, 27021.46) * mm, "end": v(2352.14, 27088.76) * mm});
            skLineSegment(sketch, "E1092", {"start": v(2291.24, 27002.6) * mm, "end": v(2368.55, 27069.9) * mm});
            skLineSegment(sketch, "E1093", {"start": v(2350.92, 27071.13) * mm, "end": v(2359.13, 27061.7) * mm});
            skLineSegment(sketch, "E1094", {"start": v(2368.55, 27069.9) * mm, "end": v(2352.14, 27088.76) * mm});
            skLineSegment(sketch, "E1095", {"start": v(978.07, 28511.1) * mm, "end": v(2258.41, 27040.32) * mm});
            skLineSegment(sketch, "E1096", {"start": v(2082.4, 26887.1) * mm, "end": v(802.06, 28357.9) * mm});
            skLineSegment(sketch, "E1097", {"start": v(815.83, 37387.25) * mm, "end": v(811.55, 37386.7) * mm});
            skLineSegment(sketch, "E1098", {"start": v(814.24, 37399.64) * mm, "end": v(808.92, 37398.96) * mm});
            skLineSegment(sketch, "E1099", {"start": v(812.08, 37416.5) * mm, "end": v(805.35, 37415.64) * mm});
            skLineSegment(sketch, "E1100", {"start": v(799.36, 37515.7) * mm, "end": v(784.36, 37513.77) * mm});
            skLineSegment(sketch, "E1101", {"start": v(797.45, 37530.57) * mm, "end": v(781.21, 37528.49) * mm});
            skLineSegment(sketch, "E1102", {"start": v(784.72, 37629.76) * mm, "end": v(760.22, 37626.62) * mm});
            skLineSegment(sketch, "E1103", {"start": v(774.67, 37708.12) * mm, "end": v(743.64, 37704.14) * mm});
            skLineSegment(sketch, "E1104", {"start": v(4783.32, 37896.2) * mm, "end": v(2849.17, 37648.08) * mm});
            skLineSegment(sketch, "E1105", {"start": v(4784.91, 37883.8) * mm, "end": v(2850.76, 37635.68) * mm});
            skLineSegment(sketch, "E1106", {"start": v(4781.73, 37908.6) * mm, "end": v(2847.58, 37660.48) * mm});
            skLineSegment(sketch, "E1107", {"start": v(4779.57, 37925.46) * mm, "end": v(2845.42, 37677.34) * mm});
            skLineSegment(sketch, "E1108", {"start": v(4766.85, 38024.64) * mm, "end": v(2832.7, 37776.53) * mm});
            skLineSegment(sketch, "E1109", {"start": v(4764.94, 38039.52) * mm, "end": v(2830.79, 37791.4) * mm});
            skLineSegment(sketch, "E1110", {"start": v(4752.21, 38138.7) * mm, "end": v(2818.06, 37890.6) * mm});
            skLineSegment(sketch, "E1111", {"start": v(4742.16, 38217.07) * mm, "end": v(2808.01, 37968.95) * mm});
            skLineSegment(sketch, "E1112", {"start": v(2808.01, 37968.95) * mm, "end": v(2850.76, 37635.68) * mm});
            skLineSegment(sketch, "E1113", {"start": v(774.67, 37708.12) * mm, "end": v(817.42, 37374.85) * mm});
            skLineSegment(sketch, "E1114", {"start": v(4742.16, 38217.07) * mm, "end": v(4784.91, 37883.8) * mm});
            skLineSegment(sketch, "E1115", {"start": v(2767.58, 37891.18) * mm, "end": v(2222.05, 37821.2) * mm});
            skLineSegment(sketch, "E1116", {"start": v(2222.05, 37821.2) * mm, "end": v(2216.96, 37860.87) * mm});
            skLineSegment(sketch, "E1117", {"start": v(2216.96, 37860.87) * mm, "end": v(2762.49, 37930.85) * mm});
            skLineSegment(sketch, "E1118", {"start": v(2762.49, 37930.85) * mm, "end": v(2767.58, 37891.18) * mm});
            skLineSegment(sketch, "E1119", {"start": v(1467.39, 37676) * mm, "end": v(2132.75, 37509) * mm});
            skLineSegment(sketch, "E1120", {"start": v(2091.75, 37791.68) * mm, "end": v(1512.5, 37717.37) * mm});
            skLineSegment(sketch, "E1121", {"start": v(1512.5, 37717.37) * mm, "end": v(1507.4, 37757.05) * mm});
            skLineSegment(sketch, "E1122", {"start": v(1507.4, 37757.05) * mm, "end": v(2086.66, 37831.35) * mm});
            skLineSegment(sketch, "E1123", {"start": v(2086.66, 37831.35) * mm, "end": v(2091.75, 37791.68) * mm});
            skLineSegment(sketch, "E1124", {"start": v(1378.96, 37713.04) * mm, "end": v(833.43, 37643.06) * mm});
            skLineSegment(sketch, "E1125", {"start": v(833.43, 37643.06) * mm, "end": v(828.34, 37682.74) * mm});
            skLineSegment(sketch, "E1126", {"start": v(828.34, 37682.74) * mm, "end": v(1373.87, 37752.72) * mm});
            skLineSegment(sketch, "E1127", {"start": v(1373.87, 37752.72) * mm, "end": v(1378.96, 37713.04) * mm});
            skLineSegment(sketch, "E1128", {"start": v(2242.6, 37661) * mm, "end": v(2193, 37654.65) * mm});
            skLineSegment(sketch, "E1129", {"start": v(2193, 37654.65) * mm, "end": v(2167.37, 37854.5) * mm});
            skLineSegment(sketch, "E1130", {"start": v(2167.37, 37854.5) * mm, "end": v(2216.96, 37860.87) * mm});
            skLineSegment(sketch, "E1131", {"start": v(2216.96, 37860.87) * mm, "end": v(2242.6, 37661) * mm});
            skLineSegment(sketch, "E1132", {"start": v(853.98, 37482.88) * mm, "end": v(804.38, 37476.51) * mm});
            skLineSegment(sketch, "E1133", {"start": v(804.38, 37476.51) * mm, "end": v(778.74, 37676.38) * mm});
            skLineSegment(sketch, "E1134", {"start": v(778.74, 37676.38) * mm, "end": v(828.34, 37682.74) * mm});
            skLineSegment(sketch, "E1135", {"start": v(828.34, 37682.74) * mm, "end": v(853.98, 37482.88) * mm});
            skLineSegment(sketch, "E1136", {"start": v(2788.13, 37730.99) * mm, "end": v(853.98, 37482.88) * mm});
            skLineSegment(sketch, "E1137", {"start": v(2808.01, 37968.95) * mm, "end": v(774.67, 37708.12) * mm});
            skLineSegment(sketch, "E1138", {"start": v(2147.81, 37763.28) * mm, "end": v(2147.05, 37769.23) * mm});
            skLineSegment(sketch, "E1139", {"start": v(2147.05, 37769.23) * mm, "end": v(2177.8, 37773.18) * mm});
            skLineSegment(sketch, "E1140", {"start": v(2177.8, 37773.18) * mm, "end": v(2167.37, 37854.5) * mm});
            skLineSegment(sketch, "E1141", {"start": v(2167.37, 37854.5) * mm, "end": v(2085.04, 37843.95) * mm});
            skLineSegment(sketch, "E1142", {"start": v(2085.04, 37843.95) * mm, "end": v(2096.24, 37756.66) * mm});
            skLineSegment(sketch, "E1143", {"start": v(2096.24, 37756.66) * mm, "end": v(2147.81, 37763.28) * mm});
            skLineSegment(sketch, "E1144", {"start": v(2216.96, 37860.87) * mm, "end": v(2167.37, 37854.5) * mm});
            skLineSegment(sketch, "E1145", {"start": v(2167.37, 37854.5) * mm, "end": v(2163.3, 37886.25) * mm});
            skLineSegment(sketch, "E1146", {"start": v(2163.3, 37886.25) * mm, "end": v(2212.89, 37892.61) * mm});
            skLineSegment(sketch, "E1147", {"start": v(2212.89, 37892.61) * mm, "end": v(2216.96, 37860.87) * mm});
            skLineSegment(sketch, "E1148", {"start": v(1433.9, 37677.75) * mm, "end": v(1466.63, 37681.95) * mm});
            skLineSegment(sketch, "E1149", {"start": v(1466.63, 37681.95) * mm, "end": v(1467.39, 37676) * mm});
            skLineSegment(sketch, "E1150", {"start": v(1467.39, 37676) * mm, "end": v(1516.98, 37682.36) * mm});
            skLineSegment(sketch, "E1151", {"start": v(1516.98, 37682.36) * mm, "end": v(1505.79, 37769.64) * mm});
            skLineSegment(sketch, "E1152", {"start": v(1505.79, 37769.64) * mm, "end": v(1423.46, 37759.08) * mm});
            skLineSegment(sketch, "E1153", {"start": v(1423.46, 37759.08) * mm, "end": v(1433.9, 37677.75) * mm});
            skLineSegment(sketch, "E1154", {"start": v(1449.1, 37559.22) * mm, "end": v(1399.5, 37552.86) * mm});
            skLineSegment(sketch, "E1155", {"start": v(1399.5, 37552.86) * mm, "end": v(1373.87, 37752.72) * mm});
            skLineSegment(sketch, "E1156", {"start": v(1373.87, 37752.72) * mm, "end": v(1423.46, 37759.08) * mm});
            skLineSegment(sketch, "E1157", {"start": v(1423.46, 37759.08) * mm, "end": v(1449.1, 37559.22) * mm});
            skLineSegment(sketch, "E1158", {"start": v(1423.46, 37759.08) * mm, "end": v(1373.87, 37752.72) * mm});
            skLineSegment(sketch, "E1159", {"start": v(1373.87, 37752.72) * mm, "end": v(1369.8, 37784.46) * mm});
            skLineSegment(sketch, "E1160", {"start": v(1369.8, 37784.46) * mm, "end": v(1419.39, 37790.82) * mm});
            skLineSegment(sketch, "E1161", {"start": v(1419.39, 37790.82) * mm, "end": v(1423.46, 37759.08) * mm});
            skLineSegment(sketch, "E1162", {"start": v(2837.72, 37737.35) * mm, "end": v(2788.13, 37730.99) * mm});
            skLineSegment(sketch, "E1163", {"start": v(2788.13, 37730.99) * mm, "end": v(2762.49, 37930.85) * mm});
            skLineSegment(sketch, "E1164", {"start": v(2762.49, 37930.85) * mm, "end": v(2812.08, 37937.21) * mm});
            skLineSegment(sketch, "E1165", {"start": v(2812.08, 37937.21) * mm, "end": v(2837.72, 37737.35) * mm});
            skLineSegment(sketch, "E1166", {"start": v(828.34, 37682.74) * mm, "end": v(778.74, 37676.38) * mm});
            skLineSegment(sketch, "E1167", {"start": v(778.74, 37676.38) * mm, "end": v(774.67, 37708.12) * mm});
            skLineSegment(sketch, "E1168", {"start": v(774.67, 37708.12) * mm, "end": v(824.27, 37714.48) * mm});
            skLineSegment(sketch, "E1169", {"start": v(824.27, 37714.48) * mm, "end": v(828.34, 37682.74) * mm});
            skLineSegment(sketch, "E1170", {"start": v(2812.08, 37937.21) * mm, "end": v(2762.49, 37930.85) * mm});
            skLineSegment(sketch, "E1171", {"start": v(2762.49, 37930.85) * mm, "end": v(2758.42, 37962.6) * mm});
            skLineSegment(sketch, "E1172", {"start": v(2758.42, 37962.6) * mm, "end": v(2808.01, 37968.95) * mm});
            skLineSegment(sketch, "E1173", {"start": v(2808.01, 37968.95) * mm, "end": v(2812.08, 37937.21) * mm});
            skArc(sketch, "E1174", {"start": v(2132.75, 37509) * mm, "mid": v(2152.19, 37635.43) * mm, "end": v(2147.81, 37763.28) * mm});
            skLineSegment(sketch, "E1175", {"start": v(2836.77, 37646.5) * mm, "end": v(2825.32, 37735.76) * mm});
            skLineSegment(sketch, "E1176", {"start": v(2824.38, 37644.9) * mm, "end": v(2812.92, 37734.17) * mm});
            skLineSegment(sketch, "E1177", {"start": v(2849.17, 37648.08) * mm, "end": v(2837.72, 37737.35) * mm});
            skLineSegment(sketch, "E1178", {"start": v(2836.77, 37646.5) * mm, "end": v(2849.17, 37648.08) * mm});
            skLineSegment(sketch, "E1179", {"start": v(2849.17, 37648.08) * mm, "end": v(2850.76, 37635.68) * mm});
            skLineSegment(sketch, "E1180", {"start": v(2850.76, 37635.68) * mm, "end": v(2825.97, 37632.5) * mm});
            skLineSegment(sketch, "E1181", {"start": v(2825.97, 37632.5) * mm, "end": v(2824.38, 37644.9) * mm});
            skLineSegment(sketch, "E1182", {"start": v(816.78, 37478.1) * mm, "end": v(828.23, 37388.84) * mm});
            skLineSegment(sketch, "E1183", {"start": v(829.18, 37479.7) * mm, "end": v(840.63, 37390.43) * mm});
            skLineSegment(sketch, "E1184", {"start": v(804.38, 37476.51) * mm, "end": v(815.83, 37387.25) * mm});
            skLineSegment(sketch, "E1185", {"start": v(828.23, 37388.84) * mm, "end": v(815.83, 37387.25) * mm});
            skLineSegment(sketch, "E1186", {"start": v(815.83, 37387.25) * mm, "end": v(817.42, 37374.85) * mm});
            skLineSegment(sketch, "E1187", {"start": v(817.42, 37374.85) * mm, "end": v(842.22, 37378.03) * mm});
            skLineSegment(sketch, "E1188", {"start": v(842.22, 37378.03) * mm, "end": v(840.63, 37390.43) * mm});
            skLineSegment(sketch, "E1189", {"start": v(-4283.18, 35844.63) * mm, "end": v(-2420.32, 29690.08) * mm});
            skLineSegment(sketch, "E1190", {"start": v(-4267.6, 35836.28) * mm, "end": v(-2411.98, 29705.67) * mm});
            skLineSegment(sketch, "E1191", {"start": v(-4298.76, 35852.97) * mm, "end": v(-2428.66, 29674.5) * mm});
            skLineSegment(sketch, "E1192", {"start": v(-4319.96, 35864.31) * mm, "end": v(-2440.01, 29653.3) * mm});
            skLineSegment(sketch, "E1193", {"start": v(-4444.64, 35931.06) * mm, "end": v(-2506.75, 29528.62) * mm});
            skLineSegment(sketch, "E1194", {"start": v(-4463.34, 35941.07) * mm, "end": v(-2516.76, 29509.92) * mm});
            skLineSegment(sketch, "E1195", {"start": v(-4588.02, 36007.8) * mm, "end": v(-2583.5, 29385.24) * mm});
            skLineSegment(sketch, "E1196", {"start": v(-4686.52, 36060.54) * mm, "end": v(-2636.23, 29286.74) * mm});
            skLineSegment(sketch, "E1197", {"start": v(-789.5, 30183.7) * mm, "end": v(-448.47, 30286.92) * mm});
            skLineSegment(sketch, "E1198", {"start": v(-793.12, 30195.66) * mm, "end": v(-444.35, 30301.23) * mm});
            skLineSegment(sketch, "E1199", {"start": v(-785.87, 30171.74) * mm, "end": v(-452.6, 30272.61) * mm});
            skLineSegment(sketch, "E1200", {"start": v(-780.95, 30155.47) * mm, "end": v(-458.2, 30253.16) * mm});
            skLineSegment(sketch, "E1201", {"start": v(-751.98, 30059.75) * mm, "end": v(-491.14, 30138.7) * mm});
            skLineSegment(sketch, "E1202", {"start": v(-747.63, 30045.4) * mm, "end": v(-496.08, 30121.54) * mm});
            skLineSegment(sketch, "E1203", {"start": v(-718.66, 29949.68) * mm, "end": v(-529.03, 30007.08) * mm});
            skLineSegment(sketch, "E1204", {"start": v(-695.78, 29874.07) * mm, "end": v(-555.06, 29916.66) * mm});
            skLineSegment(sketch, "E1205", {"start": v(-2420.32, 29690.08) * mm, "end": v(-2177.32, 29763.64) * mm});
            skLineSegment(sketch, "E1206", {"start": v(-2411.98, 29705.67) * mm, "end": v(-2180.94, 29775.6) * mm});
            skLineSegment(sketch, "E1207", {"start": v(-2428.66, 29674.5) * mm, "end": v(-2173.7, 29751.67) * mm});
            skLineSegment(sketch, "E1208", {"start": v(-2440.01, 29653.3) * mm, "end": v(-2168.77, 29735.4) * mm});
            skLineSegment(sketch, "E1209", {"start": v(-2506.75, 29528.62) * mm, "end": v(-2139.8, 29639.69) * mm});
            skLineSegment(sketch, "E1210", {"start": v(-2516.76, 29509.92) * mm, "end": v(-2135.45, 29625.33) * mm});
            skLineSegment(sketch, "E1211", {"start": v(-2583.5, 29385.24) * mm, "end": v(-2106.48, 29529.62) * mm});
            skLineSegment(sketch, "E1212", {"start": v(-2636.23, 29286.74) * mm, "end": v(-2083.6, 29454) * mm});
            skLineSegment(sketch, "E1213", {"start": v(-2083.6, 29454) * mm, "end": v(-2180.94, 29775.6) * mm});
            skLineSegment(sketch, "E1214", {"start": v(-695.78, 29874.07) * mm, "end": v(-793.12, 30195.66) * mm});
            skLineSegment(sketch, "E1215", {"start": v(-2053.7, 29527.83) * mm, "end": v(-1527.29, 29687.17) * mm});
            skLineSegment(sketch, "E1216", {"start": v(-1527.29, 29687.17) * mm, "end": v(-1518.6, 29658.46) * mm});
            skLineSegment(sketch, "E1217", {"start": v(-1518.6, 29658.46) * mm, "end": v(-2045.01, 29499.12) * mm});
            skLineSegment(sketch, "E1218", {"start": v(-2045.01, 29499.12) * mm, "end": v(-2053.7, 29527.83) * mm});
            skLineSegment(sketch, "E1219", {"start": v(-809.98, 29964.88) * mm, "end": v(-1493.81, 30019.42) * mm});
            skLineSegment(sketch, "E1220", {"start": v(-1403.67, 29737.85) * mm, "end": v(-844.71, 29907.04) * mm});
            skLineSegment(sketch, "E1221", {"start": v(-844.71, 29907.04) * mm, "end": v(-836.02, 29878.33) * mm});
            skLineSegment(sketch, "E1222", {"start": v(-836.02, 29878.33) * mm, "end": v(-1394.98, 29709.14) * mm});
            skLineSegment(sketch, "E1223", {"start": v(-1394.98, 29709.14) * mm, "end": v(-1403.67, 29737.85) * mm});
            skLineSegment(sketch, "E1224", {"start": v(-1576.97, 29851.31) * mm, "end": v(-1529.12, 29865.8) * mm});
            skLineSegment(sketch, "E1225", {"start": v(-1529.12, 29865.8) * mm, "end": v(-1470.74, 29672.94) * mm});
            skLineSegment(sketch, "E1226", {"start": v(-1470.74, 29672.94) * mm, "end": v(-1518.6, 29658.46) * mm});
            skLineSegment(sketch, "E1227", {"start": v(-1518.6, 29658.46) * mm, "end": v(-1576.97, 29851.31) * mm});
            skLineSegment(sketch, "E1228", {"start": v(-2103.39, 29691.98) * mm, "end": v(-763.42, 30097.56) * mm});
            skLineSegment(sketch, "E1229", {"start": v(-2083.6, 29454) * mm, "end": v(-695.78, 29874.07) * mm});
            skLineSegment(sketch, "E1230", {"start": v(-1466.56, 29766.15) * mm, "end": v(-1464.83, 29760.4) * mm});
            skLineSegment(sketch, "E1231", {"start": v(-1464.83, 29760.4) * mm, "end": v(-1494.5, 29751.42) * mm});
            skLineSegment(sketch, "E1232", {"start": v(-1494.5, 29751.42) * mm, "end": v(-1470.74, 29672.94) * mm});
            skLineSegment(sketch, "E1233", {"start": v(-1470.74, 29672.94) * mm, "end": v(-1391.3, 29696.99) * mm});
            skLineSegment(sketch, "E1234", {"start": v(-1391.3, 29696.99) * mm, "end": v(-1416.8, 29781.21) * mm});
            skLineSegment(sketch, "E1235", {"start": v(-1416.8, 29781.21) * mm, "end": v(-1466.56, 29766.15) * mm});
            skLineSegment(sketch, "E1236", {"start": v(-1518.6, 29658.46) * mm, "end": v(-1470.74, 29672.94) * mm});
            skLineSegment(sketch, "E1237", {"start": v(-1470.74, 29672.94) * mm, "end": v(-1461.47, 29642.31) * mm});
            skLineSegment(sketch, "E1238", {"start": v(-1461.47, 29642.31) * mm, "end": v(-1509.33, 29627.83) * mm});
            skLineSegment(sketch, "E1239", {"start": v(-1509.33, 29627.83) * mm, "end": v(-1518.6, 29658.46) * mm});
            skLineSegment(sketch, "E1240", {"start": v(-776.66, 29968.7) * mm, "end": v(-808.24, 29959.14) * mm});
            skLineSegment(sketch, "E1241", {"start": v(-808.24, 29959.14) * mm, "end": v(-809.98, 29964.88) * mm});
            skLineSegment(sketch, "E1242", {"start": v(-809.98, 29964.88) * mm, "end": v(-857.84, 29950.4) * mm});
            skLineSegment(sketch, "E1243", {"start": v(-857.84, 29950.4) * mm, "end": v(-832.34, 29866.17) * mm});
            skLineSegment(sketch, "E1244", {"start": v(-832.34, 29866.17) * mm, "end": v(-752.9, 29890.22) * mm});
            skLineSegment(sketch, "E1245", {"start": v(-752.9, 29890.22) * mm, "end": v(-776.66, 29968.7) * mm});
            skLineSegment(sketch, "E1246", {"start": v(-811.28, 30083.07) * mm, "end": v(-763.42, 30097.56) * mm});
            skLineSegment(sketch, "E1247", {"start": v(-763.42, 30097.56) * mm, "end": v(-705.05, 29904.7) * mm});
            skLineSegment(sketch, "E1248", {"start": v(-705.05, 29904.7) * mm, "end": v(-752.9, 29890.22) * mm});
            skLineSegment(sketch, "E1249", {"start": v(-752.9, 29890.22) * mm, "end": v(-811.28, 30083.07) * mm});
            skLineSegment(sketch, "E1250", {"start": v(-752.9, 29890.22) * mm, "end": v(-705.05, 29904.7) * mm});
            skLineSegment(sketch, "E1251", {"start": v(-705.05, 29904.7) * mm, "end": v(-695.78, 29874.07) * mm});
            skLineSegment(sketch, "E1252", {"start": v(-695.78, 29874.07) * mm, "end": v(-743.63, 29859.59) * mm});
            skLineSegment(sketch, "E1253", {"start": v(-743.63, 29859.59) * mm, "end": v(-752.9, 29890.22) * mm});
            skLineSegment(sketch, "E1254", {"start": v(-2151.24, 29677.5) * mm, "end": v(-2103.39, 29691.98) * mm});
            skLineSegment(sketch, "E1255", {"start": v(-2103.39, 29691.98) * mm, "end": v(-2045.01, 29499.12) * mm});
            skLineSegment(sketch, "E1256", {"start": v(-2045.01, 29499.12) * mm, "end": v(-2092.87, 29484.64) * mm});
            skLineSegment(sketch, "E1257", {"start": v(-2092.87, 29484.64) * mm, "end": v(-2151.24, 29677.5) * mm});
            skLineSegment(sketch, "E1258", {"start": v(-2092.87, 29484.64) * mm, "end": v(-2045.01, 29499.12) * mm});
            skLineSegment(sketch, "E1259", {"start": v(-2045.01, 29499.12) * mm, "end": v(-2035.74, 29468.5) * mm});
            skLineSegment(sketch, "E1260", {"start": v(-2035.74, 29468.5) * mm, "end": v(-2083.6, 29454) * mm});
            skLineSegment(sketch, "E1261", {"start": v(-2083.6, 29454) * mm, "end": v(-2092.87, 29484.64) * mm});
            skArc(sketch, "E1262", {"start": v(-1493.81, 30019.42) * mm, "mid": v(-1492.05, 29891.5) * mm, "end": v(-1466.56, 29766.15) * mm});
            skLineSegment(sketch, "E1263", {"start": v(-801.46, 30180.08) * mm, "end": v(-775.39, 30093.94) * mm});
            skLineSegment(sketch, "E1264", {"start": v(-793.12, 30195.66) * mm, "end": v(-763.42, 30097.56) * mm});
            skLineSegment(sketch, "E1265", {"start": v(-817.04, 30188.42) * mm, "end": v(-787.35, 30090.32) * mm});
            skLineSegment(sketch, "E1266", {"start": v(-801.46, 30180.08) * mm, "end": v(-789.5, 30183.7) * mm});
            skLineSegment(sketch, "E1267", {"start": v(-793.12, 30195.66) * mm, "end": v(-817.04, 30188.42) * mm});
            skLineSegment(sketch, "E1268", {"start": v(-789.5, 30183.7) * mm, "end": v(-801.46, 30180.08) * mm});
            skLineSegment(sketch, "E1269", {"start": v(-2139.28, 29681.12) * mm, "end": v(-2165.35, 29767.26) * mm});
            skLineSegment(sketch, "E1270", {"start": v(-2151.24, 29677.5) * mm, "end": v(-2180.94, 29775.6) * mm});
            skLineSegment(sketch, "E1271", {"start": v(-2127.31, 29684.74) * mm, "end": v(-2157, 29782.84) * mm});
            skLineSegment(sketch, "E1272", {"start": v(-2165.35, 29767.26) * mm, "end": v(-2177.32, 29763.64) * mm});
            skLineSegment(sketch, "E1273", {"start": v(-2180.94, 29775.6) * mm, "end": v(-2157, 29782.84) * mm});
            skLineSegment(sketch, "E1274", {"start": v(-2177.32, 29763.64) * mm, "end": v(-2165.35, 29767.26) * mm});
            skLineSegment(sketch, "E1275", {"start": v(-2951.22, 36247.78) * mm, "end": v(-4283.18, 35844.63) * mm});
            skLineSegment(sketch, "E1276", {"start": v(-2947.6, 36235.82) * mm, "end": v(-4267.6, 35836.28) * mm});
            skLineSegment(sketch, "E1277", {"start": v(-2954.85, 36259.75) * mm, "end": v(-4298.76, 35852.97) * mm});
            skLineSegment(sketch, "E1278", {"start": v(-2959.77, 36276.02) * mm, "end": v(-4319.96, 35864.31) * mm});
            skLineSegment(sketch, "E1279", {"start": v(-2988.74, 36371.73) * mm, "end": v(-4444.64, 35931.06) * mm});
            skLineSegment(sketch, "E1280", {"start": v(-2993.09, 36386.08) * mm, "end": v(-4463.34, 35941.07) * mm});
            skLineSegment(sketch, "E1281", {"start": v(-3022.06, 36481.8) * mm, "end": v(-4588.02, 36007.8) * mm});
            skLineSegment(sketch, "E1282", {"start": v(-3044.94, 36557.4) * mm, "end": v(-4686.52, 36060.54) * mm});
            skLineSegment(sketch, "E1283", {"start": v(811.55, 37386.7) * mm, "end": v(-989.13, 36841.67) * mm});
            skLineSegment(sketch, "E1284", {"start": v(814.17, 37374.43) * mm, "end": v(-985.51, 36829.7) * mm});
            skLineSegment(sketch, "E1285", {"start": v(808.92, 37398.96) * mm, "end": v(-992.75, 36853.63) * mm});
            skLineSegment(sketch, "E1286", {"start": v(805.35, 37415.64) * mm, "end": v(-997.68, 36869.9) * mm});
            skLineSegment(sketch, "E1287", {"start": v(784.36, 37513.77) * mm, "end": v(-1026.65, 36965.61) * mm});
            skLineSegment(sketch, "E1288", {"start": v(781.21, 37528.49) * mm, "end": v(-1031, 36979.97) * mm});
            skLineSegment(sketch, "E1289", {"start": v(760.22, 37626.62) * mm, "end": v(-1059.97, 37075.68) * mm});
            skLineSegment(sketch, "E1290", {"start": v(743.64, 37704.14) * mm, "end": v(-1082.85, 37151.3) * mm});
            skLineSegment(sketch, "E1291", {"start": v(-1082.85, 37151.3) * mm, "end": v(-985.51, 36829.7) * mm});
            skLineSegment(sketch, "E1292", {"start": v(-3044.94, 36557.4) * mm, "end": v(-2947.6, 36235.82) * mm});
            skLineSegment(sketch, "E1293", {"start": v(-1109.85, 37067.9) * mm, "end": v(-1636.26, 36908.56) * mm});
            skLineSegment(sketch, "E1294", {"start": v(-1636.26, 36908.56) * mm, "end": v(-1647.85, 36946.85) * mm});
            skLineSegment(sketch, "E1295", {"start": v(-1647.85, 36946.85) * mm, "end": v(-1121.44, 37106.18) * mm});
            skLineSegment(sketch, "E1296", {"start": v(-1121.44, 37106.18) * mm, "end": v(-1109.85, 37067.9) * mm});
            skLineSegment(sketch, "E1297", {"start": v(-2356.47, 36640.42) * mm, "end": v(-1672.64, 36585.88) * mm});
            skLineSegment(sketch, "E1298", {"start": v(-1759.88, 36857.88) * mm, "end": v(-2318.84, 36688.7) * mm});
            skLineSegment(sketch, "E1299", {"start": v(-2318.84, 36688.7) * mm, "end": v(-2330.43, 36726.98) * mm});
            skLineSegment(sketch, "E1300", {"start": v(-2330.43, 36726.98) * mm, "end": v(-1771.47, 36896.16) * mm});
            skLineSegment(sketch, "E1301", {"start": v(-1771.47, 36896.16) * mm, "end": v(-1759.88, 36857.88) * mm});
            skLineSegment(sketch, "E1302", {"start": v(-2449.81, 36662.32) * mm, "end": v(-2976.23, 36502.98) * mm});
            skLineSegment(sketch, "E1303", {"start": v(-2976.23, 36502.98) * mm, "end": v(-2987.82, 36541.27) * mm});
            skLineSegment(sketch, "E1304", {"start": v(-2987.82, 36541.27) * mm, "end": v(-2461.4, 36700.6) * mm});
            skLineSegment(sketch, "E1305", {"start": v(-2461.4, 36700.6) * mm, "end": v(-2449.81, 36662.32) * mm});
            skLineSegment(sketch, "E1306", {"start": v(-1589.48, 36753.99) * mm, "end": v(-1637.33, 36739.5) * mm});
            skLineSegment(sketch, "E1307", {"start": v(-1637.33, 36739.5) * mm, "end": v(-1695.7, 36932.36) * mm});
            skLineSegment(sketch, "E1308", {"start": v(-1695.7, 36932.36) * mm, "end": v(-1647.85, 36946.85) * mm});
            skLineSegment(sketch, "E1309", {"start": v(-1647.85, 36946.85) * mm, "end": v(-1589.48, 36753.99) * mm});
            skLineSegment(sketch, "E1310", {"start": v(-2929.44, 36348.4) * mm, "end": v(-2977.3, 36333.92) * mm});
            skLineSegment(sketch, "E1311", {"start": v(-2977.3, 36333.92) * mm, "end": v(-3035.67, 36526.78) * mm});
            skLineSegment(sketch, "E1312", {"start": v(-3035.67, 36526.78) * mm, "end": v(-2987.82, 36541.27) * mm});
            skLineSegment(sketch, "E1313", {"start": v(-2987.82, 36541.27) * mm, "end": v(-2929.44, 36348.4) * mm});
            skLineSegment(sketch, "E1314", {"start": v(-1063.06, 36913.32) * mm, "end": v(-2929.44, 36348.4) * mm});
            skLineSegment(sketch, "E1315", {"start": v(-1082.85, 37151.3) * mm, "end": v(-3044.94, 36557.4) * mm});
            skLineSegment(sketch, "E1316", {"start": v(-1699.88, 36839.15) * mm, "end": v(-1701.62, 36844.9) * mm});
            skLineSegment(sketch, "E1317", {"start": v(-1701.62, 36844.9) * mm, "end": v(-1671.95, 36853.88) * mm});
            skLineSegment(sketch, "E1318", {"start": v(-1671.95, 36853.88) * mm, "end": v(-1695.7, 36932.36) * mm});
            skLineSegment(sketch, "E1319", {"start": v(-1695.7, 36932.36) * mm, "end": v(-1775.15, 36908.32) * mm});
            skLineSegment(sketch, "E1320", {"start": v(-1775.15, 36908.32) * mm, "end": v(-1749.65, 36824.09) * mm});
            skLineSegment(sketch, "E1321", {"start": v(-1749.65, 36824.09) * mm, "end": v(-1699.88, 36839.15) * mm});
            skLineSegment(sketch, "E1322", {"start": v(-1647.85, 36946.85) * mm, "end": v(-1695.7, 36932.36) * mm});
            skLineSegment(sketch, "E1323", {"start": v(-1695.7, 36932.36) * mm, "end": v(-1704.98, 36962.99) * mm});
            skLineSegment(sketch, "E1324", {"start": v(-1704.98, 36962.99) * mm, "end": v(-1657.12, 36977.47) * mm});
            skLineSegment(sketch, "E1325", {"start": v(-1657.12, 36977.47) * mm, "end": v(-1647.85, 36946.85) * mm});
            skLineSegment(sketch, "E1326", {"start": v(-2389.8, 36636.6) * mm, "end": v(-2358.2, 36646.16) * mm});
            skLineSegment(sketch, "E1327", {"start": v(-2358.2, 36646.16) * mm, "end": v(-2356.47, 36640.42) * mm});
            skLineSegment(sketch, "E1328", {"start": v(-2356.47, 36640.42) * mm, "end": v(-2308.61, 36654.9) * mm});
            skLineSegment(sketch, "E1329", {"start": v(-2308.61, 36654.9) * mm, "end": v(-2334.1, 36739.13) * mm});
            skLineSegment(sketch, "E1330", {"start": v(-2334.1, 36739.13) * mm, "end": v(-2413.55, 36715.09) * mm});
            skLineSegment(sketch, "E1331", {"start": v(-2413.55, 36715.09) * mm, "end": v(-2389.8, 36636.6) * mm});
            skLineSegment(sketch, "E1332", {"start": v(-2355.17, 36522.23) * mm, "end": v(-2403.03, 36507.74) * mm});
            skLineSegment(sketch, "E1333", {"start": v(-2403.03, 36507.74) * mm, "end": v(-2461.4, 36700.6) * mm});
            skLineSegment(sketch, "E1334", {"start": v(-2461.4, 36700.6) * mm, "end": v(-2413.55, 36715.09) * mm});
            skLineSegment(sketch, "E1335", {"start": v(-2413.55, 36715.09) * mm, "end": v(-2355.17, 36522.23) * mm});
            skLineSegment(sketch, "E1336", {"start": v(-2413.55, 36715.09) * mm, "end": v(-2461.4, 36700.6) * mm});
            skLineSegment(sketch, "E1337", {"start": v(-2461.4, 36700.6) * mm, "end": v(-2470.67, 36731.23) * mm});
            skLineSegment(sketch, "E1338", {"start": v(-2470.67, 36731.23) * mm, "end": v(-2422.82, 36745.71) * mm});
            skLineSegment(sketch, "E1339", {"start": v(-2422.82, 36745.71) * mm, "end": v(-2413.55, 36715.09) * mm});
            skLineSegment(sketch, "E1340", {"start": v(-1015.2, 36927.8) * mm, "end": v(-1063.06, 36913.32) * mm});
            skLineSegment(sketch, "E1341", {"start": v(-1063.06, 36913.32) * mm, "end": v(-1121.44, 37106.18) * mm});
            skLineSegment(sketch, "E1342", {"start": v(-1121.44, 37106.18) * mm, "end": v(-1073.58, 37120.67) * mm});
            skLineSegment(sketch, "E1343", {"start": v(-1073.58, 37120.67) * mm, "end": v(-1015.2, 36927.8) * mm});
            skLineSegment(sketch, "E1344", {"start": v(-2987.82, 36541.27) * mm, "end": v(-3035.67, 36526.78) * mm});
            skLineSegment(sketch, "E1345", {"start": v(-3035.67, 36526.78) * mm, "end": v(-3044.94, 36557.4) * mm});
            skLineSegment(sketch, "E1346", {"start": v(-3044.94, 36557.4) * mm, "end": v(-2997.09, 36571.9) * mm});
            skLineSegment(sketch, "E1347", {"start": v(-2997.09, 36571.9) * mm, "end": v(-2987.82, 36541.27) * mm});
            skLineSegment(sketch, "E1348", {"start": v(-1073.58, 37120.67) * mm, "end": v(-1121.44, 37106.18) * mm});
            skLineSegment(sketch, "E1349", {"start": v(-1121.44, 37106.18) * mm, "end": v(-1130.7, 37136.8) * mm});
            skLineSegment(sketch, "E1350", {"start": v(-1130.7, 37136.8) * mm, "end": v(-1082.85, 37151.3) * mm});
            skLineSegment(sketch, "E1351", {"start": v(-1082.85, 37151.3) * mm, "end": v(-1073.58, 37120.67) * mm});
            skArc(sketch, "E1352", {"start": v(-1672.64, 36585.88) * mm, "mid": v(-1674.4, 36713.8) * mm, "end": v(-1699.88, 36839.15) * mm});
            skLineSegment(sketch, "E1353", {"start": v(-1001.1, 36838.05) * mm, "end": v(-1027.17, 36924.19) * mm});
            skLineSegment(sketch, "E1354", {"start": v(-1013.06, 36834.42) * mm, "end": v(-1039.13, 36920.56) * mm});
            skLineSegment(sketch, "E1355", {"start": v(-989.13, 36841.67) * mm, "end": v(-1015.2, 36927.8) * mm});
            skLineSegment(sketch, "E1356", {"start": v(-1001.1, 36838.05) * mm, "end": v(-989.13, 36841.67) * mm});
            skLineSegment(sketch, "E1357", {"start": v(-989.13, 36841.67) * mm, "end": v(-985.51, 36829.7) * mm});
            skLineSegment(sketch, "E1358", {"start": v(-985.51, 36829.7) * mm, "end": v(-1009.44, 36822.46) * mm});
            skLineSegment(sketch, "E1359", {"start": v(-1009.44, 36822.46) * mm, "end": v(-1013.06, 36834.42) * mm});
            skLineSegment(sketch, "E1360", {"start": v(-2965.33, 36337.54) * mm, "end": v(-2939.26, 36251.4) * mm});
            skLineSegment(sketch, "E1361", {"start": v(-2953.37, 36341.16) * mm, "end": v(-2927.3, 36255.02) * mm});
            skLineSegment(sketch, "E1362", {"start": v(-2977.3, 36333.92) * mm, "end": v(-2951.22, 36247.78) * mm});
            skLineSegment(sketch, "E1363", {"start": v(-2939.26, 36251.4) * mm, "end": v(-2951.22, 36247.78) * mm});
            skLineSegment(sketch, "E1364", {"start": v(-2951.22, 36247.78) * mm, "end": v(-2947.6, 36235.82) * mm});
            skLineSegment(sketch, "E1365", {"start": v(-2947.6, 36235.82) * mm, "end": v(-2923.68, 36243.06) * mm});
            skLineSegment(sketch, "E1366", {"start": v(-2923.68, 36243.06) * mm, "end": v(-2927.3, 36255.02) * mm});
            skLineSegment(sketch, "E1367", {"start": v(8303.3, 25022.24) * mm, "end": v(8590.44, 25109.15) * mm});
            skLineSegment(sketch, "E1368", {"start": v(8590.44, 25109.15) * mm, "end": v(9039.33, 23626.12) * mm});
            skLineSegment(sketch, "E1369", {"start": v(9039.33, 23626.12) * mm, "end": v(8752.2, 23539.21) * mm});
            skLineSegment(sketch, "E1370", {"start": v(8752.2, 23539.21) * mm, "end": v(8303.3, 25022.24) * mm});
            skLineSegment(sketch, "E1371", {"start": v(197.13, 30196.02) * mm, "end": v(-281.42, 30051.14) * mm});
            skLineSegment(sketch, "E1372", {"start": v(-281.42, 30051.14) * mm, "end": v(-353.86, 30290.42) * mm});
            skLineSegment(sketch, "E1373", {"start": v(-353.86, 30290.42) * mm, "end": v(124.69, 30435.3) * mm});
            skLineSegment(sketch, "E1374", {"start": v(124.69, 30435.3) * mm, "end": v(197.13, 30196.02) * mm});
            skLineSegment(sketch, "E1375", {"start": v(8948.07, 22978.3) * mm, "end": v(9187.35, 23050.73) * mm});
            skLineSegment(sketch, "E1376", {"start": v(9067.7, 23014.51) * mm, "end": v(9011.18, 23201.26) * mm});
            skLineSegment(sketch, "E1377", {"start": v(9067.7, 23014.51) * mm, "end": v(9049.5, 23009) * mm});
            skCircle(sketch, "E1378", {"center": v(4156.9, 27384.5) * mm, "radius": 200 * mm});
            skLineSegment(sketch, "E1379", {"start": v(8752.39, 23538.73) * mm, "end": v(9409.92, 21366) * mm});
            skLineSegment(sketch, "E1380", {"start": v(-353.88, 30290.43) * mm, "end": v(124.67, 30435.31) * mm});
            skLineSegment(sketch, "E1381", {"start": v(197.11, 30196.04) * mm, "end": v(124.67, 30435.31) * mm});
            skLineSegment(sketch, "E1382", {"start": v(-281.44, 30051.16) * mm, "end": v(197.11, 30196.04) * mm});
            skLineSegment(sketch, "E1383", {"start": v(-281.44, 30051.16) * mm, "end": v(-353.88, 30290.43) * mm});
            skLineSegment(sketch, "E1384", {"start": v(-2472.02, 30328.5) * mm, "end": v(-2327.14, 29849.96) * mm});
            skLineSegment(sketch, "E1385", {"start": v(-2566.42, 29777.52) * mm, "end": v(-2327.14, 29849.96) * mm});
            skLineSegment(sketch, "E1386", {"start": v(-2711.3, 30256.07) * mm, "end": v(-2566.42, 29777.52) * mm});
            skLineSegment(sketch, "E1387", {"start": v(-2711.3, 30256.07) * mm, "end": v(-2472.02, 30328.5) * mm});
            skLineSegment(sketch, "E1388", {"start": v(-4186.63, 35993.38) * mm, "end": v(-4041.78, 35514.82) * mm});
            skLineSegment(sketch, "E1389", {"start": v(-4281.06, 35442.4) * mm, "end": v(-4041.78, 35514.82) * mm});
            skLineSegment(sketch, "E1390", {"start": v(-4425.9, 35920.95) * mm, "end": v(-4281.06, 35442.4) * mm});
            skLineSegment(sketch, "E1391", {"start": v(-4425.9, 35920.95) * mm, "end": v(-4186.63, 35993.38) * mm});
            skLineSegment(sketch, "E1392", {"start": v(-511.89, 37105.65) * mm, "end": v(-33.33, 37250.5) * mm});
            skLineSegment(sketch, "E1393", {"start": v(39.1, 37011.22) * mm, "end": v(-33.33, 37250.5) * mm});
            skLineSegment(sketch, "E1394", {"start": v(-439.46, 36866.37) * mm, "end": v(39.1, 37011.22) * mm});
            skLineSegment(sketch, "E1395", {"start": v(-439.46, 36866.37) * mm, "end": v(-511.89, 37105.65) * mm});
            skLineSegment(sketch, "E1396", {"start": v(4693.12, 37985.2) * mm, "end": v(8590.44, 25109.15) * mm});
            skLineSegment(sketch, "E1397", {"start": v(4405.99, 37898.29) * mm, "end": v(8303.3, 25022.24) * mm});
            skLineSegment(sketch, "E1398", {"start": v(4405.99, 37898.29) * mm, "end": v(4693.12, 37985.2) * mm});
            skLineSegment(sketch, "E1399", {"start": v(8030.58, 19741.8) * mm, "end": v(7885.73, 20220.35) * mm});
            skArc(sketch, "E1400", {"start": v(2269.14, 28633.68) * mm, "mid": v(2276.69, 28709.85) * mm, "end": v(2335.88, 28758.37) * mm});
            skLineSegment(sketch, "E1401", {"start": v(2335.88, 28758.37) * mm, "end": v(2878.3, 28922.55) * mm});
            skArc(sketch, "E1402", {"start": v(2878.3, 28922.55) * mm, "mid": v(2954.46, 28915) * mm, "end": v(3002.98, 28855.8) * mm});
            skLineSegment(sketch, "E1403", {"start": v(3002.98, 28855.8) * mm, "end": v(3296.16, 27887.2) * mm});
            skArc(sketch, "E1404", {"start": v(3296.16, 27887.2) * mm, "mid": v(3288.6, 27811.04) * mm, "end": v(3229.42, 27762.52) * mm});
            skLineSegment(sketch, "E1405", {"start": v(3229.42, 27762.52) * mm, "end": v(2687, 27598.34) * mm});
            skLineSegment(sketch, "E1406", {"start": v(4965.73, 23360.9) * mm, "end": v(4664.93, 23706.28) * mm});
            skLineSegment(sketch, "E1407", {"start": v(4664.93, 23706.28) * mm, "end": v(4755.42, 23785.1) * mm});
            skLineSegment(sketch, "E1408", {"start": v(4755.42, 23785.1) * mm, "end": v(5056.22, 23439.72) * mm});
            skLineSegment(sketch, "E1409", {"start": v(5056.22, 23439.72) * mm, "end": v(4965.73, 23360.9) * mm});
            skLineSegment(sketch, "E1410", {"start": v(4674.44, 23545.8) * mm, "end": v(4815.33, 23533.6) * mm});
            skLineSegment(sketch, "E1411", {"start": v(4815.33, 23533.6) * mm, "end": v(4803.13, 23392.71) * mm});
            skLineSegment(sketch, "E1412", {"start": v(4803.13, 23392.71) * mm, "end": v(4674.44, 23545.8) * mm});
            skLineSegment(sketch, "E1413", {"start": v(-436.04, 36975.35) * mm, "end": v(-370.87, 36760) * mm});
            skLineSegment(sketch, "E1414", {"start": v(-370.87, 36760) * mm, "end": v(-752.76, 36644.43) * mm});
            skLineSegment(sketch, "E1415", {"start": v(-752.76, 36644.43) * mm, "end": v(-817.94, 36859.78) * mm});
            skLineSegment(sketch, "E1416", {"start": v(-817.94, 36859.78) * mm, "end": v(-436.04, 36975.35) * mm});
            skLineSegment(sketch, "E1417", {"start": v(-494.77, 36722.5) * mm, "end": v(-480.29, 36674.65) * mm});
            skLineSegment(sketch, "E1418", {"start": v(-480.29, 36674.65) * mm, "end": v(-622.99, 36631.46) * mm});
            skLineSegment(sketch, "E1419", {"start": v(-622.99, 36631.46) * mm, "end": v(-637.47, 36679.32) * mm});
            skLineSegment(sketch, "E1420", {"start": v(-637.47, 36679.32) * mm, "end": v(-494.77, 36722.5) * mm});
            skLineSegment(sketch, "E1421", {"start": v(-570.8, 37337.8) * mm, "end": v(-1087.66, 37181.4) * mm});
            skLineSegment(sketch, "E1422", {"start": v(-771.24, 37240.58) * mm, "end": v(-866.95, 37211.62) * mm});
            skLineSegment(sketch, "E1423", {"start": v(-866.95, 37211.62) * mm, "end": v(-754.7, 36840.73) * mm});
            skArc(sketch, "E1424", {"start": v(-754.7, 36840.73) * mm, "mid": v(-692.94, 36809.25) * mm, "end": v(-659, 36869.7) * mm});
            skLineSegment(sketch, "E1425", {"start": v(-659, 36869.7) * mm, "end": v(-771.24, 37240.58) * mm});
            skLineSegment(sketch, "E1426", {"start": v(-807.47, 37360.3) * mm, "end": v(-772.69, 37245.37) * mm});
            skLineSegment(sketch, "E1427", {"start": v(-772.69, 37245.37) * mm, "end": v(-868.4, 37216.4) * mm});
            skLineSegment(sketch, "E1428", {"start": v(-868.4, 37216.4) * mm, "end": v(-903.18, 37331.34) * mm});
            skLineSegment(sketch, "E1429", {"start": v(-903.18, 37331.34) * mm, "end": v(-807.47, 37360.3) * mm});
            skLineSegment(sketch, "E1430", {"start": v(-715.26, 37262.75) * mm, "end": v(-713.81, 37257.96) * mm});
            skLineSegment(sketch, "E1431", {"start": v(-713.81, 37257.96) * mm, "end": v(-924.38, 37194.24) * mm});
            skLineSegment(sketch, "E1432", {"start": v(-924.38, 37194.24) * mm, "end": v(-925.83, 37199.02) * mm});
            skLineSegment(sketch, "E1433", {"start": v(-925.83, 37199.02) * mm, "end": v(-715.26, 37262.75) * mm});
            skLineSegment(sketch, "E1434", {"start": v(-661.9, 37086.54) * mm, "end": v(-660.45, 37081.76) * mm});
            skLineSegment(sketch, "E1435", {"start": v(-660.45, 37081.76) * mm, "end": v(-871.01, 37018.03) * mm});
            skLineSegment(sketch, "E1436", {"start": v(-871.01, 37018.03) * mm, "end": v(-872.46, 37022.82) * mm});
            skLineSegment(sketch, "E1437", {"start": v(-872.46, 37022.82) * mm, "end": v(-661.9, 37086.54) * mm});
            skLineSegment(sketch, "E1438", {"start": v(-859.07, 37344.69) * mm, "end": v(-884.06, 37337.19) * mm});
            skLineSegment(sketch, "E1439", {"start": v(-884.06, 37337.19) * mm, "end": v(-901.42, 37394.56) * mm});
            skLineSegment(sketch, "E1440", {"start": v(-901.42, 37394.56) * mm, "end": v(-844, 37411.94) * mm});
            skLineSegment(sketch, "E1441", {"start": v(-844, 37411.94) * mm, "end": v(-826.61, 37354.51) * mm});
            skLineSegment(sketch, "E1442", {"start": v(-826.61, 37354.51) * mm, "end": v(-859.07, 37344.69) * mm});
            skLineSegment(sketch, "E1443", {"start": v(-545.2, 36459.12) * mm, "end": v(-590.75, 36609.63) * mm});
            skLineSegment(sketch, "E1444", {"start": v(-590.75, 36609.63) * mm, "end": v(-495.04, 36638.6) * mm});
            skLineSegment(sketch, "E1445", {"start": v(-495.04, 36638.6) * mm, "end": v(-478.45, 36583.8) * mm});
            skLineSegment(sketch, "E1446", {"start": v(-478.45, 36583.8) * mm, "end": v(263.6, 36808.38) * mm});
            skLineSegment(sketch, "E1447", {"start": v(263.6, 36808.38) * mm, "end": v(1951.6, 31231.48) * mm});
            skLineSegment(sketch, "E1448", {"start": v(1951.6, 31231.48) * mm, "end": v(5860.45, 32414.6) * mm});
            skLineSegment(sketch, "E1449", {"start": v(5860.45, 32414.6) * mm, "end": v(6137.86, 31498.09) * mm});
            skLineSegment(sketch, "E1450", {"start": v(6137.86, 31498.09) * mm, "end": v(6042.15, 31469.12) * mm});
            skLineSegment(sketch, "E1451", {"start": v(6042.15, 31469.12) * mm, "end": v(5793.7, 32289.93) * mm});
            skLineSegment(sketch, "E1452", {"start": v(5793.7, 32289.93) * mm, "end": v(1884.86, 31106.8) * mm});
            skLineSegment(sketch, "E1453", {"start": v(1884.86, 31106.8) * mm, "end": v(196.85, 36683.7) * mm});
            skLineSegment(sketch, "E1454", {"start": v(196.85, 36683.7) * mm, "end": v(-497.34, 36473.6) * mm});
            skLineSegment(sketch, "E1455", {"start": v(-497.34, 36473.6) * mm, "end": v(-545.2, 36459.12) * mm});
            skLineSegment(sketch, "E1456", {"start": v(2834.55, 38123.59) * mm, "end": v(3288.83, 38181.86) * mm});
            skLineSegment(sketch, "E1457", {"start": v(3288.83, 38181.86) * mm, "end": v(3304.1, 38062.84) * mm});
            skLineSegment(sketch, "E1458", {"start": v(3304.1, 38062.84) * mm, "end": v(2849.82, 38004.56) * mm});
            skLineSegment(sketch, "E1459", {"start": v(2849.82, 38004.56) * mm, "end": v(2834.55, 38123.59) * mm});
            skLineSegment(sketch, "E1460", {"start": v(3062.96, 38142.8) * mm, "end": v(2961.17, 38936.3) * mm});
            skLineSegment(sketch, "E1461", {"start": v(2874.71, 38824.4) * mm, "end": v(2961.17, 38936.3) * mm});
            skLineSegment(sketch, "E1462", {"start": v(2961.17, 38936.3) * mm, "end": v(3073.08, 38849.85) * mm});
            skLineSegment(sketch, "E1463", {"start": v(3073.08, 38849.85) * mm, "end": v(2874.71, 38824.4) * mm});
            skLineSegment(sketch, "E1464", {"start": v(2331.57, 26371.66) * mm, "end": v(2030.77, 26717.04) * mm});
            skLineSegment(sketch, "E1465", {"start": v(2030.77, 26717.04) * mm, "end": v(2121.26, 26795.85) * mm});
            skLineSegment(sketch, "E1466", {"start": v(2121.26, 26795.85) * mm, "end": v(2422.06, 26450.48) * mm});
            skLineSegment(sketch, "E1467", {"start": v(2422.06, 26450.48) * mm, "end": v(2331.57, 26371.66) * mm});
            skArc(sketch, "E1468", {"start": v(-703.63, 37502.46) * mm, "mid": v(-730.29, 37505.1) * mm, "end": v(-747.27, 37525.82) * mm});
            skLineSegment(sketch, "E1469", {"start": v(-747.27, 37525.82) * mm, "end": v(-1019.28, 38424.52) * mm});
            skArc(sketch, "E1470", {"start": v(-1019.28, 38424.52) * mm, "mid": v(-1016.64, 38451.17) * mm, "end": v(-995.92, 38468.16) * mm});
            skLineSegment(sketch, "E1471", {"start": v(-995.92, 38468.16) * mm, "end": v(-501.25, 38617.88) * mm});
            skArc(sketch, "E1472", {"start": v(-501.25, 38617.88) * mm, "mid": v(-474.6, 38615.24) * mm, "end": v(-457.61, 38594.52) * mm});
            skLineSegment(sketch, "E1473", {"start": v(-457.61, 38594.52) * mm, "end": v(-185.6, 37695.83) * mm});
            skArc(sketch, "E1474", {"start": v(-185.6, 37695.83) * mm, "mid": v(-188.24, 37669.17) * mm, "end": v(-208.96, 37652.2) * mm});
            skLineSegment(sketch, "E1475", {"start": v(-208.96, 37652.2) * mm, "end": v(-703.63, 37502.46) * mm});
            skArc(sketch, "E1476", {"start": v(2331.2, 38107.6) * mm, "mid": v(2304.55, 38110.25) * mm, "end": v(2287.57, 38130.96) * mm});
            skLineSegment(sketch, "E1477", {"start": v(2287.57, 38130.96) * mm, "end": v(2015.55, 39029.66) * mm});
            skArc(sketch, "E1478", {"start": v(2015.55, 39029.66) * mm, "mid": v(2018.2, 39056.32) * mm, "end": v(2038.9, 39073.3) * mm});
            skLineSegment(sketch, "E1479", {"start": v(2038.9, 39073.3) * mm, "end": v(2533.58, 39223.02) * mm});
            skArc(sketch, "E1480", {"start": v(2533.58, 39223.02) * mm, "mid": v(2560.24, 39220.38) * mm, "end": v(2577.22, 39199.66) * mm});
            skLineSegment(sketch, "E1481", {"start": v(2577.22, 39199.66) * mm, "end": v(2849.23, 38300.97) * mm});
            skArc(sketch, "E1482", {"start": v(2849.23, 38300.97) * mm, "mid": v(2846.6, 38274.31) * mm, "end": v(2825.87, 38257.33) * mm});
            skLineSegment(sketch, "E1483", {"start": v(2825.87, 38257.33) * mm, "end": v(2331.2, 38107.6) * mm});
            skArc(sketch, "E1484", {"start": v(2379.2, 26143.37) * mm, "mid": v(2405.85, 26140.73) * mm, "end": v(2422.83, 26120.01) * mm});
            skArc(sketch, "E1485", {"start": v(5314.63, 22054.47) * mm, "mid": v(5311.99, 22027.81) * mm, "end": v(5291.27, 22010.83) * mm});
            skLineSegment(sketch, "E1486", {"start": v(716.1, 33838.68) * mm, "end": v(970.38, 32998.58) * mm});
            skLineSegment(sketch, "E1487", {"start": v(970.38, 32998.58) * mm, "end": v(700.26, 32916.82) * mm});
            skLineSegment(sketch, "E1488", {"start": v(700.26, 32916.82) * mm, "end": v(445.98, 33756.92) * mm});
            skLineSegment(sketch, "E1489", {"start": v(445.98, 33756.92) * mm, "end": v(716.1, 33838.68) * mm});
            skLineSegment(sketch, "E1490", {"start": v(727.53, 33815.17) * mm, "end": v(966.97, 33024.1) * mm});
            skLineSegment(sketch, "E1491", {"start": v(966.97, 33024.1) * mm, "end": v(717.1, 32948.47) * mm});
            skLineSegment(sketch, "E1492", {"start": v(717.1, 32948.47) * mm, "end": v(477.67, 33739.54) * mm});
            skLineSegment(sketch, "E1493", {"start": v(477.67, 33739.54) * mm, "end": v(727.53, 33815.17) * mm});
            skLineSegment(sketch, "E1494", {"start": v(440.6, 33809.24) * mm, "end": v(724.8, 32870.3) * mm});
            skLineSegment(sketch, "E1495", {"start": v(724.8, 32870.3) * mm, "end": v(705.65, 32864.5) * mm});
            skLineSegment(sketch, "E1496", {"start": v(705.65, 32864.5) * mm, "end": v(421.45, 33803.44) * mm});
            skLineSegment(sketch, "E1497", {"start": v(421.45, 33803.44) * mm, "end": v(440.6, 33809.24) * mm});
            skLineSegment(sketch, "E1498", {"start": v(810.64, 33867.3) * mm, "end": v(1064.92, 33027.2) * mm});
            skLineSegment(sketch, "E1499", {"start": v(1064.92, 33027.2) * mm, "end": v(794.8, 32945.44) * mm});
            skLineSegment(sketch, "E1500", {"start": v(794.8, 32945.44) * mm, "end": v(540.52, 33785.54) * mm});
            skLineSegment(sketch, "E1501", {"start": v(540.52, 33785.54) * mm, "end": v(810.64, 33867.3) * mm});
            skLineSegment(sketch, "E1502", {"start": v(818.12, 33842.59) * mm, "end": v(1057.56, 33051.52) * mm});
            skLineSegment(sketch, "E1503", {"start": v(1057.56, 33051.52) * mm, "end": v(809.68, 32976.49) * mm});
            skLineSegment(sketch, "E1504", {"start": v(809.68, 32976.49) * mm, "end": v(570.23, 33767.56) * mm});
            skLineSegment(sketch, "E1505", {"start": v(570.23, 33767.56) * mm, "end": v(818.12, 33842.59) * mm});
            skLineSegment(sketch, "E1506", {"start": v(535.14, 33837.85) * mm, "end": v(819.33, 32898.92) * mm});
            skLineSegment(sketch, "E1507", {"start": v(819.33, 32898.92) * mm, "end": v(800.2, 32893.13) * mm});
            skLineSegment(sketch, "E1508", {"start": v(800.2, 32893.13) * mm, "end": v(516, 33832.06) * mm});
            skLineSegment(sketch, "E1509", {"start": v(516, 33832.06) * mm, "end": v(535.14, 33837.85) * mm});
            skLineSegment(sketch, "E1510", {"start": v(874.87, 33886.52) * mm, "end": v(1129.15, 33046.43) * mm});
            skLineSegment(sketch, "E1511", {"start": v(1129.15, 33046.43) * mm, "end": v(859.03, 32964.67) * mm});
            skLineSegment(sketch, "E1512", {"start": v(859.03, 32964.67) * mm, "end": v(604.75, 33804.76) * mm});
            skLineSegment(sketch, "E1513", {"start": v(604.75, 33804.76) * mm, "end": v(874.87, 33886.52) * mm});
            skLineSegment(sketch, "E1514", {"start": v(886.3, 33863) * mm, "end": v(1125.73, 33071.94) * mm});
            skLineSegment(sketch, "E1515", {"start": v(1125.73, 33071.94) * mm, "end": v(875.87, 32996.31) * mm});
            skLineSegment(sketch, "E1516", {"start": v(875.87, 32996.31) * mm, "end": v(636.43, 33787.38) * mm});
            skLineSegment(sketch, "E1517", {"start": v(636.43, 33787.38) * mm, "end": v(886.3, 33863) * mm});
            skLineSegment(sketch, "E1518", {"start": v(599.36, 33857.08) * mm, "end": v(883.56, 32918.15) * mm});
            skLineSegment(sketch, "E1519", {"start": v(883.56, 32918.15) * mm, "end": v(864.41, 32912.35) * mm});
            skLineSegment(sketch, "E1520", {"start": v(864.41, 32912.35) * mm, "end": v(580.22, 33851.28) * mm});
            skLineSegment(sketch, "E1521", {"start": v(580.22, 33851.28) * mm, "end": v(599.36, 33857.08) * mm});
            skLineSegment(sketch, "E1522", {"start": v(969.4, 33915.14) * mm, "end": v(1223.69, 33075.04) * mm});
            skLineSegment(sketch, "E1523", {"start": v(1223.69, 33075.04) * mm, "end": v(953.57, 32993.28) * mm});
            skLineSegment(sketch, "E1524", {"start": v(953.57, 32993.28) * mm, "end": v(699.29, 33833.38) * mm});
            skLineSegment(sketch, "E1525", {"start": v(699.29, 33833.38) * mm, "end": v(969.4, 33915.14) * mm});
            skLineSegment(sketch, "E1526", {"start": v(976.89, 33890.43) * mm, "end": v(1216.33, 33099.36) * mm});
            skLineSegment(sketch, "E1527", {"start": v(1216.33, 33099.36) * mm, "end": v(968.44, 33024.33) * mm});
            skLineSegment(sketch, "E1528", {"start": v(968.44, 33024.33) * mm, "end": v(729, 33815.4) * mm});
            skLineSegment(sketch, "E1529", {"start": v(729, 33815.4) * mm, "end": v(976.89, 33890.43) * mm});
            skLineSegment(sketch, "E1530", {"start": v(693.9, 33885.7) * mm, "end": v(978.1, 32946.76) * mm});
            skLineSegment(sketch, "E1531", {"start": v(978.1, 32946.76) * mm, "end": v(958.96, 32940.97) * mm});
            skLineSegment(sketch, "E1532", {"start": v(958.96, 32940.97) * mm, "end": v(674.76, 33879.9) * mm});
            skLineSegment(sketch, "E1533", {"start": v(674.76, 33879.9) * mm, "end": v(693.9, 33885.7) * mm});
            skLineSegment(sketch, "E1534", {"start": v(1643.09, 33148.04) * mm, "end": v(1650.33, 33124.11) * mm});
            skLineSegment(sketch, "E1535", {"start": v(1650.33, 33124.11) * mm, "end": v(1089.45, 32954.35) * mm});
            skLineSegment(sketch, "E1536", {"start": v(1089.45, 32954.35) * mm, "end": v(1082.21, 32978.27) * mm});
            skLineSegment(sketch, "E1537", {"start": v(1082.21, 32978.27) * mm, "end": v(1643.09, 33148.04) * mm});
            skLineSegment(sketch, "E1538", {"start": v(1351.65, 34110.9) * mm, "end": v(1358.9, 34086.97) * mm});
            skLineSegment(sketch, "E1539", {"start": v(1358.9, 34086.97) * mm, "end": v(798.02, 33917.2) * mm});
            skLineSegment(sketch, "E1540", {"start": v(798.02, 33917.2) * mm, "end": v(790.77, 33941.13) * mm});
            skLineSegment(sketch, "E1541", {"start": v(790.77, 33941.13) * mm, "end": v(1351.65, 34110.9) * mm});
            skLineSegment(sketch, "E1542", {"start": v(752.16, 33450.68) * mm, "end": v(785.18, 33914.73) * mm});
            skLineSegment(sketch, "E1543", {"start": v(785.18, 33914.73) * mm, "end": v(769.72, 33921.7) * mm});
            skLineSegment(sketch, "E1544", {"start": v(769.72, 33921.7) * mm, "end": v(736.7, 33457.65) * mm});
            skLineSegment(sketch, "E1545", {"start": v(736.7, 33457.65) * mm, "end": v(752.16, 33450.68) * mm});
            skLineSegment(sketch, "E1546", {"start": v(784.65, 33343.33) * mm, "end": v(1069.47, 32975.49) * mm});
            skLineSegment(sketch, "E1547", {"start": v(1069.47, 32975.49) * mm, "end": v(1060.47, 32961.11) * mm});
            skLineSegment(sketch, "E1548", {"start": v(1060.47, 32961.11) * mm, "end": v(775.65, 33328.96) * mm});
            skLineSegment(sketch, "E1549", {"start": v(775.65, 33328.96) * mm, "end": v(784.65, 33343.33) * mm});
            skLineSegment(sketch, "E1550", {"start": v(917.16, 33440.74) * mm, "end": v(938.21, 33447.11) * mm});
            skLineSegment(sketch, "E1551", {"start": v(938.21, 33447.11) * mm, "end": v(1083.06, 32968.55) * mm});
            skLineSegment(sketch, "E1552", {"start": v(1083.06, 32968.55) * mm, "end": v(1062, 32962.18) * mm});
            skLineSegment(sketch, "E1553", {"start": v(1062, 32962.18) * mm, "end": v(917.16, 33440.74) * mm});
            skLineSegment(sketch, "E1554", {"start": v(771.42, 33922.22) * mm, "end": v(792.48, 33928.6) * mm});
            skLineSegment(sketch, "E1555", {"start": v(792.48, 33928.6) * mm, "end": v(937.33, 33450.03) * mm});
            skLineSegment(sketch, "E1556", {"start": v(937.33, 33450.03) * mm, "end": v(916.27, 33443.66) * mm});
            skLineSegment(sketch, "E1557", {"start": v(916.27, 33443.66) * mm, "end": v(771.42, 33922.22) * mm});
            skLineSegment(sketch, "E1558", {"start": v(1358.89, 34086.97) * mm, "end": v(1643.08, 33148.04) * mm});
            skLineSegment(sketch, "E1559", {"start": v(1643.08, 33148.04) * mm, "end": v(1082.21, 32978.27) * mm});
            skLineSegment(sketch, "E1560", {"start": v(1082.21, 32978.27) * mm, "end": v(798.02, 33917.2) * mm});
            skLineSegment(sketch, "E1561", {"start": v(798.02, 33917.2) * mm, "end": v(1358.89, 34086.97) * mm});
            skLineSegment(sketch, "E1562", {"start": v(1643.08, 33148.04) * mm, "end": v(798.02, 33917.2) * mm});
            skLineSegment(sketch, "E1563", {"start": v(1358.89, 34086.97) * mm, "end": v(1082.21, 32978.27) * mm});
            skLineSegment(sketch, "E1564", {"start": v(1060.21, 35073.76) * mm, "end": v(1067.46, 35049.83) * mm});
            skLineSegment(sketch, "E1565", {"start": v(1067.46, 35049.83) * mm, "end": v(506.58, 34880.07) * mm});
            skLineSegment(sketch, "E1566", {"start": v(506.58, 34880.07) * mm, "end": v(499.34, 34904) * mm});
            skLineSegment(sketch, "E1567", {"start": v(499.34, 34904) * mm, "end": v(1060.21, 35073.76) * mm});
            skLineSegment(sketch, "E1568", {"start": v(460.72, 34413.54) * mm, "end": v(493.75, 34877.6) * mm});
            skLineSegment(sketch, "E1569", {"start": v(493.75, 34877.6) * mm, "end": v(478.28, 34884.56) * mm});
            skLineSegment(sketch, "E1570", {"start": v(478.28, 34884.56) * mm, "end": v(445.26, 34420.51) * mm});
            skLineSegment(sketch, "E1571", {"start": v(445.26, 34420.51) * mm, "end": v(460.72, 34413.54) * mm});
            skLineSegment(sketch, "E1572", {"start": v(493.21, 34306.2) * mm, "end": v(778.04, 33938.35) * mm});
            skLineSegment(sketch, "E1573", {"start": v(778.04, 33938.35) * mm, "end": v(769.03, 33923.97) * mm});
            skLineSegment(sketch, "E1574", {"start": v(769.03, 33923.97) * mm, "end": v(484.21, 34291.82) * mm});
            skLineSegment(sketch, "E1575", {"start": v(484.21, 34291.82) * mm, "end": v(493.21, 34306.2) * mm});
            skLineSegment(sketch, "E1576", {"start": v(625.72, 34403.6) * mm, "end": v(646.78, 34409.97) * mm});
            skLineSegment(sketch, "E1577", {"start": v(646.78, 34409.97) * mm, "end": v(791.63, 33931.42) * mm});
            skLineSegment(sketch, "E1578", {"start": v(791.63, 33931.42) * mm, "end": v(770.57, 33925.04) * mm});
            skLineSegment(sketch, "E1579", {"start": v(770.57, 33925.04) * mm, "end": v(625.72, 34403.6) * mm});
            skLineSegment(sketch, "E1580", {"start": v(479.99, 34885.08) * mm, "end": v(501.05, 34891.45) * mm});
            skLineSegment(sketch, "E1581", {"start": v(501.05, 34891.45) * mm, "end": v(645.9, 34412.9) * mm});
            skLineSegment(sketch, "E1582", {"start": v(645.9, 34412.9) * mm, "end": v(624.84, 34406.52) * mm});
            skLineSegment(sketch, "E1583", {"start": v(624.84, 34406.52) * mm, "end": v(479.99, 34885.08) * mm});
            skLineSegment(sketch, "E1584", {"start": v(1067.45, 35049.83) * mm, "end": v(1351.65, 34110.9) * mm});
            skLineSegment(sketch, "E1585", {"start": v(1351.65, 34110.9) * mm, "end": v(790.78, 33941.14) * mm});
            skLineSegment(sketch, "E1586", {"start": v(790.78, 33941.14) * mm, "end": v(506.58, 34880.07) * mm});
            skLineSegment(sketch, "E1587", {"start": v(506.58, 34880.07) * mm, "end": v(1067.45, 35049.83) * mm});
            skLineSegment(sketch, "E1588", {"start": v(1351.65, 34110.9) * mm, "end": v(506.58, 34880.07) * mm});
            skLineSegment(sketch, "E1589", {"start": v(1067.45, 35049.83) * mm, "end": v(790.78, 33941.14) * mm});
            skLineSegment(sketch, "E1590", {"start": v(630, 36495.08) * mm, "end": v(768.77, 36036.62) * mm});
            skLineSegment(sketch, "E1591", {"start": v(768.77, 36036.62) * mm, "end": v(207.9, 35866.86) * mm});
            skLineSegment(sketch, "E1592", {"start": v(207.9, 35866.86) * mm, "end": v(69.13, 36325.32) * mm});
            skLineSegment(sketch, "E1593", {"start": v(69.13, 36325.32) * mm, "end": v(630, 36495.08) * mm});
            skLineSegment(sketch, "E1594", {"start": v(768.77, 36036.62) * mm, "end": v(69.13, 36325.32) * mm});
            skLineSegment(sketch, "E1595", {"start": v(630, 36495.08) * mm, "end": v(207.9, 35866.86) * mm});
            skLineSegment(sketch, "E1596", {"start": v(798.02, 33917.2) * mm, "end": v(790.78, 33941.14) * mm});
            skLineSegment(sketch, "E1597", {"start": v(790.78, 33941.14) * mm, "end": v(1351.65, 34110.9) * mm});
            skLineSegment(sketch, "E1598", {"start": v(1062.88, 32959.3) * mm, "end": v(1083.93, 32965.68) * mm});
            skLineSegment(sketch, "E1599", {"start": v(1083.93, 32965.68) * mm, "end": v(1095.08, 32928.84) * mm});
            skLineSegment(sketch, "E1600", {"start": v(1095.08, 32928.84) * mm, "end": v(1074.03, 32922.47) * mm});
            skLineSegment(sketch, "E1601", {"start": v(1074.03, 32922.47) * mm, "end": v(1062.88, 32959.3) * mm});
            skLineSegment(sketch, "E1602", {"start": v(776.01, 36012.7) * mm, "end": v(1060.2, 35073.76) * mm});
            skLineSegment(sketch, "E1603", {"start": v(1060.2, 35073.76) * mm, "end": v(499.34, 34904) * mm});
            skLineSegment(sketch, "E1604", {"start": v(499.34, 34904) * mm, "end": v(215.14, 35842.93) * mm});
            skLineSegment(sketch, "E1605", {"start": v(215.14, 35842.93) * mm, "end": v(776.01, 36012.7) * mm});
            skLineSegment(sketch, "E1606", {"start": v(1060.2, 35073.76) * mm, "end": v(215.14, 35842.93) * mm});
            skLineSegment(sketch, "E1607", {"start": v(776.01, 36012.7) * mm, "end": v(499.34, 34904) * mm});
            skLineSegment(sketch, "E1608", {"start": v(768.78, 36036.62) * mm, "end": v(776.02, 36012.7) * mm});
            skLineSegment(sketch, "E1609", {"start": v(776.02, 36012.7) * mm, "end": v(215.14, 35842.93) * mm});
            skLineSegment(sketch, "E1610", {"start": v(215.14, 35842.93) * mm, "end": v(207.9, 35866.86) * mm});
            skLineSegment(sketch, "E1611", {"start": v(207.9, 35866.86) * mm, "end": v(768.78, 36036.62) * mm});
            skLineSegment(sketch, "E1612", {"start": v(622.77, 36519) * mm, "end": v(630, 36495.08) * mm});
            skLineSegment(sketch, "E1613", {"start": v(630, 36495.08) * mm, "end": v(69.13, 36325.32) * mm});
            skLineSegment(sketch, "E1614", {"start": v(69.13, 36325.32) * mm, "end": v(61.9, 36349.24) * mm});
            skLineSegment(sketch, "E1615", {"start": v(61.9, 36349.24) * mm, "end": v(622.77, 36519) * mm});
            skLineSegment(sketch, "E1616", {"start": v(31.38, 36367.22) * mm, "end": v(52.43, 36373.6) * mm});
            skLineSegment(sketch, "E1617", {"start": v(52.43, 36373.6) * mm, "end": v(63, 36338.66) * mm});
            skLineSegment(sketch, "E1618", {"start": v(63, 36338.66) * mm, "end": v(41.95, 36332.3) * mm});
            skLineSegment(sketch, "E1619", {"start": v(41.95, 36332.3) * mm, "end": v(31.38, 36367.22) * mm});
            skLineSegment(sketch, "E1620", {"start": v(169.27, 35376.45) * mm, "end": v(202.3, 35840.5) * mm});
            skLineSegment(sketch, "E1621", {"start": v(202.3, 35840.5) * mm, "end": v(186.83, 35847.47) * mm});
            skLineSegment(sketch, "E1622", {"start": v(186.83, 35847.47) * mm, "end": v(153.8, 35383.42) * mm});
            skLineSegment(sketch, "E1623", {"start": v(153.8, 35383.42) * mm, "end": v(169.27, 35376.45) * mm});
            skLineSegment(sketch, "E1624", {"start": v(201.76, 35269.1) * mm, "end": v(486.58, 34901.26) * mm});
            skLineSegment(sketch, "E1625", {"start": v(486.58, 34901.26) * mm, "end": v(477.58, 34886.88) * mm});
            skLineSegment(sketch, "E1626", {"start": v(477.58, 34886.88) * mm, "end": v(192.76, 35254.73) * mm});
            skLineSegment(sketch, "E1627", {"start": v(192.76, 35254.73) * mm, "end": v(201.76, 35269.1) * mm});
            skLineSegment(sketch, "E1628", {"start": v(334.27, 35366.5) * mm, "end": v(355.33, 35372.88) * mm});
            skLineSegment(sketch, "E1629", {"start": v(355.33, 35372.88) * mm, "end": v(500.18, 34894.32) * mm});
            skLineSegment(sketch, "E1630", {"start": v(500.18, 34894.32) * mm, "end": v(479.12, 34887.95) * mm});
            skLineSegment(sketch, "E1631", {"start": v(479.12, 34887.95) * mm, "end": v(334.27, 35366.5) * mm});
            skLineSegment(sketch, "E1632", {"start": v(188.54, 35847.99) * mm, "end": v(209.6, 35854.36) * mm});
            skLineSegment(sketch, "E1633", {"start": v(209.6, 35854.36) * mm, "end": v(354.44, 35375.8) * mm});
            skLineSegment(sketch, "E1634", {"start": v(354.44, 35375.8) * mm, "end": v(333.39, 35369.43) * mm});
            skLineSegment(sketch, "E1635", {"start": v(333.39, 35369.43) * mm, "end": v(188.54, 35847.99) * mm});
            skLineSegment(sketch, "E1636", {"start": v(23.55, 35857.88) * mm, "end": v(56.58, 36321.93) * mm});
            skLineSegment(sketch, "E1637", {"start": v(56.58, 36321.93) * mm, "end": v(41.11, 36328.9) * mm});
            skLineSegment(sketch, "E1638", {"start": v(41.11, 36328.9) * mm, "end": v(8.09, 35864.85) * mm});
            skLineSegment(sketch, "E1639", {"start": v(8.09, 35864.85) * mm, "end": v(23.55, 35857.88) * mm});
            skLineSegment(sketch, "E1640", {"start": v(42.82, 36329.42) * mm, "end": v(63.87, 36335.8) * mm});
            skLineSegment(sketch, "E1641", {"start": v(63.87, 36335.8) * mm, "end": v(208.72, 35857.23) * mm});
            skLineSegment(sketch, "E1642", {"start": v(208.72, 35857.23) * mm, "end": v(187.67, 35850.86) * mm});
            skLineSegment(sketch, "E1643", {"start": v(187.67, 35850.86) * mm, "end": v(42.82, 36329.42) * mm});
            skLineSegment(sketch, "E1644", {"start": v(4780.4, 34909.38) * mm, "end": v(5193.87, 35034.53) * mm});
            skLineSegment(sketch, "E1645", {"start": v(5193.87, 35034.53) * mm, "end": v(5363.64, 34473.66) * mm});
            skLineSegment(sketch, "E1646", {"start": v(5363.64, 34473.66) * mm, "end": v(4950.17, 34348.5) * mm});
            skLineSegment(sketch, "E1647", {"start": v(4950.17, 34348.5) * mm, "end": v(4780.4, 34909.38) * mm});
            skLineSegment(sketch, "E1648", {"start": v(2815.1, 34640.25) * mm, "end": v(3655.2, 34894.53) * mm});
            skLineSegment(sketch, "E1649", {"start": v(3655.2, 34894.53) * mm, "end": v(3736.97, 34624.41) * mm});
            skLineSegment(sketch, "E1650", {"start": v(3736.97, 34624.41) * mm, "end": v(2896.87, 34370.13) * mm});
            skLineSegment(sketch, "E1651", {"start": v(2896.87, 34370.13) * mm, "end": v(2815.1, 34640.25) * mm});
            skLineSegment(sketch, "E1652", {"start": v(2846.75, 34623.4) * mm, "end": v(3637.82, 34862.85) * mm});
            skLineSegment(sketch, "E1653", {"start": v(3637.82, 34862.85) * mm, "end": v(3713.45, 34612.99) * mm});
            skLineSegment(sketch, "E1654", {"start": v(3713.45, 34612.99) * mm, "end": v(2922.38, 34373.54) * mm});
            skLineSegment(sketch, "E1655", {"start": v(2922.38, 34373.54) * mm, "end": v(2846.75, 34623.4) * mm});
            skLineSegment(sketch, "E1656", {"start": v(2762.8, 34634.86) * mm, "end": v(3701.72, 34919.06) * mm});
            skLineSegment(sketch, "E1657", {"start": v(3701.72, 34919.06) * mm, "end": v(3707.52, 34899.92) * mm});
            skLineSegment(sketch, "E1658", {"start": v(3707.52, 34899.92) * mm, "end": v(2768.59, 34615.72) * mm});
            skLineSegment(sketch, "E1659", {"start": v(2768.59, 34615.72) * mm, "end": v(2762.8, 34634.86) * mm});
            skLineSegment(sketch, "E1660", {"start": v(2843.72, 34545.7) * mm, "end": v(3683.82, 34800) * mm});
            skLineSegment(sketch, "E1661", {"start": v(3683.82, 34800) * mm, "end": v(3765.58, 34529.87) * mm});
            skLineSegment(sketch, "E1662", {"start": v(3765.58, 34529.87) * mm, "end": v(2925.49, 34275.59) * mm});
            skLineSegment(sketch, "E1663", {"start": v(2925.49, 34275.59) * mm, "end": v(2843.72, 34545.7) * mm});
            skLineSegment(sketch, "E1664", {"start": v(2874.77, 34530.83) * mm, "end": v(3665.84, 34770.28) * mm});
            skLineSegment(sketch, "E1665", {"start": v(3665.84, 34770.28) * mm, "end": v(3740.87, 34522.4) * mm});
            skLineSegment(sketch, "E1666", {"start": v(3740.87, 34522.4) * mm, "end": v(2949.8, 34282.95) * mm});
            skLineSegment(sketch, "E1667", {"start": v(2949.8, 34282.95) * mm, "end": v(2874.77, 34530.83) * mm});
            skLineSegment(sketch, "E1668", {"start": v(2791.41, 34540.32) * mm, "end": v(3730.34, 34824.52) * mm});
            skLineSegment(sketch, "E1669", {"start": v(3730.34, 34824.52) * mm, "end": v(3736.13, 34805.38) * mm});
            skLineSegment(sketch, "E1670", {"start": v(3736.13, 34805.38) * mm, "end": v(2797.2, 34521.18) * mm});
            skLineSegment(sketch, "E1671", {"start": v(2797.2, 34521.18) * mm, "end": v(2791.41, 34540.32) * mm});
            skLineSegment(sketch, "E1672", {"start": v(2830.76, 34319.24) * mm, "end": v(2854.68, 34326.49) * mm});
            skLineSegment(sketch, "E1673", {"start": v(2854.68, 34326.49) * mm, "end": v(3024.45, 33765.61) * mm});
            skLineSegment(sketch, "E1674", {"start": v(3024.45, 33765.61) * mm, "end": v(3000.52, 33758.37) * mm});
            skLineSegment(sketch, "E1675", {"start": v(3000.52, 33758.37) * mm, "end": v(2830.76, 34319.24) * mm});
            skLineSegment(sketch, "E1676", {"start": v(3793.61, 34610.69) * mm, "end": v(3817.54, 34617.93) * mm});
            skLineSegment(sketch, "E1677", {"start": v(3817.54, 34617.93) * mm, "end": v(3987.31, 34057.06) * mm});
            skLineSegment(sketch, "E1678", {"start": v(3987.31, 34057.06) * mm, "end": v(3963.38, 34049.82) * mm});
            skLineSegment(sketch, "E1679", {"start": v(3963.38, 34049.82) * mm, "end": v(3793.61, 34610.69) * mm});
            skLineSegment(sketch, "E1680", {"start": v(3327.09, 34656.54) * mm, "end": v(3791.14, 34623.52) * mm});
            skLineSegment(sketch, "E1681", {"start": v(3791.14, 34623.52) * mm, "end": v(3798.1, 34638.99) * mm});
            skLineSegment(sketch, "E1682", {"start": v(3798.1, 34638.99) * mm, "end": v(3334.06, 34672) * mm});
            skLineSegment(sketch, "E1683", {"start": v(3334.06, 34672) * mm, "end": v(3327.09, 34656.54) * mm});
            skLineSegment(sketch, "E1684", {"start": v(3219.74, 34624.05) * mm, "end": v(2851.9, 34339.23) * mm});
            skLineSegment(sketch, "E1685", {"start": v(2851.9, 34339.23) * mm, "end": v(2837.52, 34348.23) * mm});
            skLineSegment(sketch, "E1686", {"start": v(2837.52, 34348.23) * mm, "end": v(3205.36, 34633.06) * mm});
            skLineSegment(sketch, "E1687", {"start": v(3205.36, 34633.06) * mm, "end": v(3219.74, 34624.05) * mm});
            skLineSegment(sketch, "E1688", {"start": v(3317.15, 34491.54) * mm, "end": v(3323.52, 34470.49) * mm});
            skLineSegment(sketch, "E1689", {"start": v(3323.52, 34470.49) * mm, "end": v(2844.96, 34325.63) * mm});
            skLineSegment(sketch, "E1690", {"start": v(2844.96, 34325.63) * mm, "end": v(2838.59, 34346.7) * mm});
            skLineSegment(sketch, "E1691", {"start": v(2838.59, 34346.7) * mm, "end": v(3317.15, 34491.54) * mm});
            skLineSegment(sketch, "E1692", {"start": v(3798.62, 34637.28) * mm, "end": v(3805, 34616.22) * mm});
            skLineSegment(sketch, "E1693", {"start": v(3805, 34616.22) * mm, "end": v(3326.44, 34471.37) * mm});
            skLineSegment(sketch, "E1694", {"start": v(3326.44, 34471.37) * mm, "end": v(3320.07, 34492.43) * mm});
            skLineSegment(sketch, "E1695", {"start": v(3320.07, 34492.43) * mm, "end": v(3798.62, 34637.28) * mm});
            skLineSegment(sketch, "E1696", {"start": v(2854.68, 34326.49) * mm, "end": v(3793.61, 34610.69) * mm});
            skLineSegment(sketch, "E1697", {"start": v(3793.61, 34610.69) * mm, "end": v(3963.38, 34049.82) * mm});
            skLineSegment(sketch, "E1698", {"start": v(3963.38, 34049.82) * mm, "end": v(3024.45, 33765.62) * mm});
            skLineSegment(sketch, "E1699", {"start": v(3024.45, 33765.62) * mm, "end": v(2854.68, 34326.49) * mm});
            skLineSegment(sketch, "E1700", {"start": v(3024.45, 33765.62) * mm, "end": v(3793.61, 34610.69) * mm});
            skLineSegment(sketch, "E1701", {"start": v(3963.38, 34049.82) * mm, "end": v(2854.68, 34326.49) * mm});
            skLineSegment(sketch, "E1702", {"start": v(4756.47, 34902.13) * mm, "end": v(4780.4, 34909.38) * mm});
            skLineSegment(sketch, "E1703", {"start": v(4780.4, 34909.38) * mm, "end": v(4950.17, 34348.5) * mm});
            skLineSegment(sketch, "E1704", {"start": v(4950.17, 34348.5) * mm, "end": v(4926.24, 34341.26) * mm});
            skLineSegment(sketch, "E1705", {"start": v(4926.24, 34341.26) * mm, "end": v(4756.47, 34902.13) * mm});
            skLineSegment(sketch, "E1706", {"start": v(4289.94, 34947.99) * mm, "end": v(4754, 34914.97) * mm});
            skLineSegment(sketch, "E1707", {"start": v(4754, 34914.97) * mm, "end": v(4760.97, 34930.43) * mm});
            skLineSegment(sketch, "E1708", {"start": v(4760.97, 34930.43) * mm, "end": v(4296.91, 34963.45) * mm});
            skLineSegment(sketch, "E1709", {"start": v(4296.91, 34963.45) * mm, "end": v(4289.94, 34947.99) * mm});
            skLineSegment(sketch, "E1710", {"start": v(4182.6, 34915.5) * mm, "end": v(3814.75, 34630.67) * mm});
            skLineSegment(sketch, "E1711", {"start": v(3814.75, 34630.67) * mm, "end": v(3800.38, 34639.67) * mm});
            skLineSegment(sketch, "E1712", {"start": v(3800.38, 34639.67) * mm, "end": v(4168.22, 34924.5) * mm});
            skLineSegment(sketch, "E1713", {"start": v(4168.22, 34924.5) * mm, "end": v(4182.6, 34915.5) * mm});
            skLineSegment(sketch, "E1714", {"start": v(4280, 34782.99) * mm, "end": v(4286.38, 34761.93) * mm});
            skLineSegment(sketch, "E1715", {"start": v(4286.38, 34761.93) * mm, "end": v(3807.82, 34617.08) * mm});
            skLineSegment(sketch, "E1716", {"start": v(3807.82, 34617.08) * mm, "end": v(3801.45, 34638.14) * mm});
            skLineSegment(sketch, "E1717", {"start": v(3801.45, 34638.14) * mm, "end": v(4280, 34782.99) * mm});
            skLineSegment(sketch, "E1718", {"start": v(4761.48, 34928.73) * mm, "end": v(4767.86, 34907.67) * mm});
            skLineSegment(sketch, "E1719", {"start": v(4767.86, 34907.67) * mm, "end": v(4289.3, 34762.82) * mm});
            skLineSegment(sketch, "E1720", {"start": v(4289.3, 34762.82) * mm, "end": v(4282.92, 34783.87) * mm});
            skLineSegment(sketch, "E1721", {"start": v(4282.92, 34783.87) * mm, "end": v(4761.48, 34928.73) * mm});
            skLineSegment(sketch, "E1722", {"start": v(3817.54, 34617.93) * mm, "end": v(4756.47, 34902.13) * mm});
            skLineSegment(sketch, "E1723", {"start": v(4756.47, 34902.13) * mm, "end": v(4926.24, 34341.26) * mm});
            skLineSegment(sketch, "E1724", {"start": v(4926.24, 34341.26) * mm, "end": v(3987.3, 34057.06) * mm});
            skLineSegment(sketch, "E1725", {"start": v(3987.3, 34057.06) * mm, "end": v(3817.54, 34617.93) * mm});
            skLineSegment(sketch, "E1726", {"start": v(3987.3, 34057.06) * mm, "end": v(4756.47, 34902.13) * mm});
            skLineSegment(sketch, "E1727", {"start": v(4926.24, 34341.26) * mm, "end": v(3817.54, 34617.93) * mm});
            skLineSegment(sketch, "E1728", {"start": v(5193.87, 35034.53) * mm, "end": v(5217.8, 35041.77) * mm});
            skLineSegment(sketch, "E1729", {"start": v(5217.8, 35041.77) * mm, "end": v(5387.57, 34480.9) * mm});
            skLineSegment(sketch, "E1730", {"start": v(5387.57, 34480.9) * mm, "end": v(5363.64, 34473.66) * mm});
            skLineSegment(sketch, "E1731", {"start": v(5363.64, 34473.66) * mm, "end": v(5193.87, 35034.53) * mm});
            skLineSegment(sketch, "E1732", {"start": v(4764.22, 35092.48) * mm, "end": v(5191.97, 35048.84) * mm});
            skLineSegment(sketch, "E1733", {"start": v(5191.97, 35048.84) * mm, "end": v(5198.02, 35064) * mm});
            skLineSegment(sketch, "E1734", {"start": v(5198.02, 35064) * mm, "end": v(4770.27, 35107.64) * mm});
            skLineSegment(sketch, "E1735", {"start": v(4770.27, 35107.64) * mm, "end": v(4764.22, 35092.48) * mm});
            skLineSegment(sketch, "E1736", {"start": v(5198.88, 35061.12) * mm, "end": v(5205.26, 35040.07) * mm});
            skLineSegment(sketch, "E1737", {"start": v(5205.26, 35040.07) * mm, "end": v(4766.93, 34907.39) * mm});
            skLineSegment(sketch, "E1738", {"start": v(4766.93, 34907.39) * mm, "end": v(4760.56, 34928.45) * mm});
            skLineSegment(sketch, "E1739", {"start": v(4760.56, 34928.45) * mm, "end": v(5198.88, 35061.12) * mm});
            skLineSegment(sketch, "E1740", {"start": v(4950.17, 34348.5) * mm, "end": v(5191.25, 35033.75) * mm});
            skLineSegment(sketch, "E1741", {"start": v(5363.64, 34473.66) * mm, "end": v(4780.4, 34909.4) * mm});
            skLineSegment(sketch, "E1742", {"start": v(2805.77, 34313.77) * mm, "end": v(2799.4, 34334.83) * mm});
            skLineSegment(sketch, "E1743", {"start": v(2799.4, 34334.83) * mm, "end": v(2835.72, 34345.82) * mm});
            skLineSegment(sketch, "E1744", {"start": v(2835.72, 34345.82) * mm, "end": v(2842.1, 34324.77) * mm});
            skLineSegment(sketch, "E1745", {"start": v(2842.1, 34324.77) * mm, "end": v(2805.77, 34313.77) * mm});
            skLineSegment(sketch, "E1746", {"start": v(5208.18, 35040.95) * mm, "end": v(5201.8, 35062) * mm});
            skLineSegment(sketch, "E1747", {"start": v(5201.8, 35062) * mm, "end": v(5235.25, 35072.13) * mm});
            skLineSegment(sketch, "E1748", {"start": v(5235.25, 35072.13) * mm, "end": v(5241.63, 35051.07) * mm});
            skLineSegment(sketch, "E1749", {"start": v(5241.63, 35051.07) * mm, "end": v(5208.18, 35040.95) * mm});
            skLineSegment(sketch, "E1750", {"start": v(6924.09, 26007.02) * mm, "end": v(6750.27, 26581.29) * mm});
            skLineSegment(sketch, "E1751", {"start": v(6750.27, 26581.29) * mm, "end": v(7094.6, 26685.5) * mm});
            skLineSegment(sketch, "E1752", {"start": v(7094.6, 26685.5) * mm, "end": v(7268.41, 26111.24) * mm});
            skLineSegment(sketch, "E1753", {"start": v(7268.41, 26111.24) * mm, "end": v(6924.09, 26007.02) * mm});
            skLineSegment(sketch, "E1754", {"start": v(7268.41, 26111.24) * mm, "end": v(7094.6, 26685.5) * mm});
            skLineSegment(sketch, "E1755", {"start": v(7094.6, 26685.5) * mm, "end": v(7668.86, 26859.33) * mm});
            skLineSegment(sketch, "E1756", {"start": v(7668.86, 26859.33) * mm, "end": v(7842.68, 26285.06) * mm});
            skLineSegment(sketch, "E1757", {"start": v(7842.68, 26285.06) * mm, "end": v(7268.41, 26111.24) * mm});
            skLineSegment(sketch, "E1758", {"start": v(6855.98, 26655.48) * mm, "end": v(6706.41, 27149.62) * mm});
            skLineSegment(sketch, "E1759", {"start": v(6706.41, 27149.62) * mm, "end": v(6956.27, 27225.25) * mm});
            skLineSegment(sketch, "E1760", {"start": v(6956.27, 27225.25) * mm, "end": v(7105.84, 26731.11) * mm});
            skLineSegment(sketch, "E1761", {"start": v(7105.84, 26731.11) * mm, "end": v(6855.98, 26655.48) * mm});
            skArc(sketch, "E1762", {"start": v(6871.7, 26682.1) * mm, "mid": v(6859.74, 26683.3) * mm, "end": v(6852.12, 26692.58) * mm});
            skLineSegment(sketch, "E1763", {"start": v(6852.12, 26692.58) * mm, "end": v(6723.78, 27116.6) * mm});
            skArc(sketch, "E1764", {"start": v(6723.78, 27116.6) * mm, "mid": v(6724.96, 27128.57) * mm, "end": v(6734.25, 27136.18) * mm});
            skLineSegment(sketch, "E1765", {"start": v(6734.25, 27136.18) * mm, "end": v(6947.31, 27200.67) * mm});
            skArc(sketch, "E1766", {"start": v(6947.31, 27200.67) * mm, "mid": v(6959.27, 27199.49) * mm, "end": v(6966.88, 27190.2) * mm});
            skLineSegment(sketch, "E1767", {"start": v(6966.88, 27190.2) * mm, "end": v(7095.23, 26766.17) * mm});
            skArc(sketch, "E1768", {"start": v(7095.23, 26766.17) * mm, "mid": v(7094.04, 26754.21) * mm, "end": v(7084.75, 26746.6) * mm});
            skLineSegment(sketch, "E1769", {"start": v(7084.75, 26746.6) * mm, "end": v(6871.7, 26682.1) * mm});
            skLineSegment(sketch, "E1770", {"start": v(6852.76, 26666.12) * mm, "end": v(6849.9, 26675.59) * mm});
            skLineSegment(sketch, "E1771", {"start": v(6849.9, 26675.59) * mm, "end": v(7093, 26749.17) * mm});
            skLineSegment(sketch, "E1772", {"start": v(7093, 26749.17) * mm, "end": v(7095.86, 26739.7) * mm});
            skLineSegment(sketch, "E1773", {"start": v(7095.86, 26739.7) * mm, "end": v(6852.76, 26666.12) * mm});
            skLineSegment(sketch, "E1774", {"start": v(6712.32, 27130.1) * mm, "end": v(6709.45, 27139.57) * mm});
            skLineSegment(sketch, "E1775", {"start": v(6709.45, 27139.57) * mm, "end": v(6952.56, 27213.16) * mm});
            skLineSegment(sketch, "E1776", {"start": v(6952.56, 27213.16) * mm, "end": v(6955.43, 27203.7) * mm});
            skLineSegment(sketch, "E1777", {"start": v(6955.43, 27203.7) * mm, "end": v(6712.32, 27130.1) * mm});
            skArc(sketch, "E1778", {"start": v(6874.13, 26690.2) * mm, "mid": v(6862.17, 26691.4) * mm, "end": v(6854.55, 26700.69) * mm});
            skLineSegment(sketch, "E1779", {"start": v(6854.55, 26700.69) * mm, "end": v(6798.97, 26884.32) * mm});
            skArc(sketch, "E1780", {"start": v(6798.97, 26884.32) * mm, "mid": v(6800.16, 26896.28) * mm, "end": v(6809.45, 26903.9) * mm});
            skLineSegment(sketch, "E1781", {"start": v(6809.45, 26903.9) * mm, "end": v(7015.76, 26966.34) * mm});
            skArc(sketch, "E1782", {"start": v(7015.76, 26966.34) * mm, "mid": v(7027.71, 26965.15) * mm, "end": v(7035.33, 26955.86) * mm});
            skLineSegment(sketch, "E1783", {"start": v(7035.33, 26955.86) * mm, "end": v(7090.9, 26772.23) * mm});
            skArc(sketch, "E1784", {"start": v(7090.9, 26772.23) * mm, "mid": v(7089.72, 26760.27) * mm, "end": v(7080.43, 26752.65) * mm});
            skLineSegment(sketch, "E1785", {"start": v(7080.43, 26752.65) * mm, "end": v(6874.13, 26690.2) * mm});
            skArc(sketch, "E1786", {"start": v(6878.93, 26698.95) * mm, "mid": v(6866.97, 26700.14) * mm, "end": v(6859.36, 26709.43) * mm});
            skLineSegment(sketch, "E1787", {"start": v(6859.36, 26709.43) * mm, "end": v(6807.82, 26879.7) * mm});
            skArc(sketch, "E1788", {"start": v(6807.82, 26879.7) * mm, "mid": v(6809, 26891.66) * mm, "end": v(6818.3, 26899.28) * mm});
            skLineSegment(sketch, "E1789", {"start": v(6818.3, 26899.28) * mm, "end": v(7011.1, 26957.64) * mm});
            skArc(sketch, "E1790", {"start": v(7011.1, 26957.64) * mm, "mid": v(7023.05, 26956.45) * mm, "end": v(7030.67, 26947.16) * mm});
            skLineSegment(sketch, "E1791", {"start": v(7030.67, 26947.16) * mm, "end": v(7082.2, 26776.88) * mm});
            skArc(sketch, "E1792", {"start": v(7082.2, 26776.88) * mm, "mid": v(7081.02, 26764.93) * mm, "end": v(7071.73, 26757.3) * mm});
            skLineSegment(sketch, "E1793", {"start": v(7071.73, 26757.3) * mm, "end": v(6878.93, 26698.95) * mm});
            skLineSegment(sketch, "E1794", {"start": v(6831.61, 26874.15) * mm, "end": v(6878.1, 26720.57) * mm});
            skLineSegment(sketch, "E1795", {"start": v(6878.1, 26720.57) * mm, "end": v(6891.6, 26724.66) * mm});
            skLineSegment(sketch, "E1796", {"start": v(6891.6, 26724.66) * mm, "end": v(6851.18, 26858.2) * mm});
            skLineSegment(sketch, "E1797", {"start": v(6851.18, 26858.2) * mm, "end": v(7013.25, 26907.27) * mm});
            skLineSegment(sketch, "E1798", {"start": v(7013.25, 26907.27) * mm, "end": v(7007.2, 26927.3) * mm});
            skLineSegment(sketch, "E1799", {"start": v(7007.2, 26927.3) * mm, "end": v(6831.61, 26874.15) * mm});
            skArc(sketch, "E1800", {"start": v(6806.41, 26915.6) * mm, "mid": v(6794.46, 26916.78) * mm, "end": v(6786.84, 26926.07) * mm});
            skLineSegment(sketch, "E1801", {"start": v(6786.84, 26926.07) * mm, "end": v(6731.26, 27109.7) * mm});
            skArc(sketch, "E1802", {"start": v(6731.26, 27109.7) * mm, "mid": v(6732.44, 27121.66) * mm, "end": v(6741.74, 27129.28) * mm});
            skLineSegment(sketch, "E1803", {"start": v(6741.74, 27129.28) * mm, "end": v(6948.04, 27191.72) * mm});
            skArc(sketch, "E1804", {"start": v(6948.04, 27191.72) * mm, "mid": v(6960, 27190.54) * mm, "end": v(6967.61, 27181.25) * mm});
            skLineSegment(sketch, "E1805", {"start": v(6967.61, 27181.25) * mm, "end": v(7023.2, 26997.61) * mm});
            skArc(sketch, "E1806", {"start": v(7023.2, 26997.61) * mm, "mid": v(7022.01, 26985.66) * mm, "end": v(7012.72, 26978.04) * mm});
            skLineSegment(sketch, "E1807", {"start": v(7012.72, 26978.04) * mm, "end": v(6806.41, 26915.6) * mm});
            skArc(sketch, "E1808", {"start": v(6811.22, 26924.34) * mm, "mid": v(6799.26, 26925.52) * mm, "end": v(6791.64, 26934.82) * mm});
            skLineSegment(sketch, "E1809", {"start": v(6791.64, 26934.82) * mm, "end": v(6740.1, 27105.1) * mm});
            skArc(sketch, "E1810", {"start": v(6740.1, 27105.1) * mm, "mid": v(6741.29, 27117.05) * mm, "end": v(6750.58, 27124.67) * mm});
            skLineSegment(sketch, "E1811", {"start": v(6750.58, 27124.67) * mm, "end": v(6943.38, 27183.02) * mm});
            skArc(sketch, "E1812", {"start": v(6943.38, 27183.02) * mm, "mid": v(6955.34, 27181.84) * mm, "end": v(6962.95, 27172.55) * mm});
            skLineSegment(sketch, "E1813", {"start": v(6962.95, 27172.55) * mm, "end": v(7014.5, 27002.27) * mm});
            skArc(sketch, "E1814", {"start": v(7014.5, 27002.27) * mm, "mid": v(7013.3, 26990.31) * mm, "end": v(7004.01, 26982.7) * mm});
            skLineSegment(sketch, "E1815", {"start": v(7004.01, 26982.7) * mm, "end": v(6811.22, 26924.34) * mm});
            skLineSegment(sketch, "E1816", {"start": v(6763.9, 27099.54) * mm, "end": v(6810.39, 26945.96) * mm});
            skLineSegment(sketch, "E1817", {"start": v(6810.39, 26945.96) * mm, "end": v(6823.9, 26950.04) * mm});
            skLineSegment(sketch, "E1818", {"start": v(6823.9, 26950.04) * mm, "end": v(6783.47, 27083.6) * mm});
            skLineSegment(sketch, "E1819", {"start": v(6783.47, 27083.6) * mm, "end": v(6945.54, 27132.65) * mm});
            skLineSegment(sketch, "E1820", {"start": v(6945.54, 27132.65) * mm, "end": v(6939.48, 27152.68) * mm});
            skLineSegment(sketch, "E1821", {"start": v(6939.48, 27152.68) * mm, "end": v(6763.9, 27099.54) * mm});
            skLineSegment(sketch, "E1822", {"start": v(6849.65, 26609.83) * mm, "end": v(6675.83, 27184.1) * mm});
            skLineSegment(sketch, "E1823", {"start": v(6675.83, 27184.1) * mm, "end": v(6694.97, 27189.9) * mm});
            skLineSegment(sketch, "E1824", {"start": v(6694.97, 27189.9) * mm, "end": v(6868.79, 26615.62) * mm});
            skLineSegment(sketch, "E1825", {"start": v(6868.79, 26615.62) * mm, "end": v(6849.65, 26609.83) * mm});
            skLineSegment(sketch, "E1826", {"start": v(7316.67, 25538.47) * mm, "end": v(7167.47, 26031.38) * mm});
            skLineSegment(sketch, "E1827", {"start": v(7167.47, 26031.38) * mm, "end": v(7437.6, 26113.14) * mm});
            skLineSegment(sketch, "E1828", {"start": v(7437.6, 26113.14) * mm, "end": v(7586.79, 25620.23) * mm});
            skLineSegment(sketch, "E1829", {"start": v(7586.79, 25620.23) * mm, "end": v(7316.67, 25538.47) * mm});
            skLineSegment(sketch, "E1830", {"start": v(7332.31, 25559.85) * mm, "end": v(7193.25, 26019.27) * mm});
            skLineSegment(sketch, "E1831", {"start": v(7193.25, 26019.27) * mm, "end": v(7443.12, 26094.9) * mm});
            skLineSegment(sketch, "E1832", {"start": v(7443.12, 26094.9) * mm, "end": v(7582.17, 25635.48) * mm});
            skLineSegment(sketch, "E1833", {"start": v(7582.17, 25635.48) * mm, "end": v(7332.31, 25559.85) * mm});
            skLineSegment(sketch, "E1834", {"start": v(7314.12, 25498.19) * mm, "end": v(7140.3, 26072.46) * mm});
            skLineSegment(sketch, "E1835", {"start": v(7140.3, 26072.46) * mm, "end": v(7159.44, 26078.25) * mm});
            skLineSegment(sketch, "E1836", {"start": v(7159.44, 26078.25) * mm, "end": v(7333.26, 25503.98) * mm});
            skLineSegment(sketch, "E1837", {"start": v(7333.26, 25503.98) * mm, "end": v(7314.12, 25498.19) * mm});
            skLineSegment(sketch, "E1838", {"start": v(7490.49, 24964.2) * mm, "end": v(7341.3, 25457.11) * mm});
            skLineSegment(sketch, "E1839", {"start": v(7341.3, 25457.11) * mm, "end": v(7611.41, 25538.87) * mm});
            skLineSegment(sketch, "E1840", {"start": v(7611.41, 25538.87) * mm, "end": v(7760.6, 25045.96) * mm});
            skLineSegment(sketch, "E1841", {"start": v(7760.6, 25045.96) * mm, "end": v(7490.49, 24964.2) * mm});
            skLineSegment(sketch, "E1842", {"start": v(7506.13, 24985.58) * mm, "end": v(7367.07, 25445) * mm});
            skLineSegment(sketch, "E1843", {"start": v(7367.07, 25445) * mm, "end": v(7616.94, 25520.63) * mm});
            skLineSegment(sketch, "E1844", {"start": v(7616.94, 25520.63) * mm, "end": v(7756, 25061.21) * mm});
            skLineSegment(sketch, "E1845", {"start": v(7756, 25061.21) * mm, "end": v(7506.13, 24985.58) * mm});
            skLineSegment(sketch, "E1846", {"start": v(7487.94, 24923.92) * mm, "end": v(7314.12, 25498.19) * mm});
            skLineSegment(sketch, "E1847", {"start": v(7314.12, 25498.19) * mm, "end": v(7333.26, 25503.98) * mm});
            skLineSegment(sketch, "E1848", {"start": v(7333.26, 25503.98) * mm, "end": v(7507.08, 24929.71) * mm});
            skLineSegment(sketch, "E1849", {"start": v(7507.08, 24929.71) * mm, "end": v(7487.94, 24923.92) * mm});
            skLineSegment(sketch, "E1850", {"start": v(7624.74, 24933.98) * mm, "end": v(6920.77, 27259.78) * mm});
            skLineSegment(sketch, "E1851", {"start": v(6920.77, 27259.78) * mm, "end": v(7542.9, 27448.08) * mm});
            skLineSegment(sketch, "E1852", {"start": v(7542.9, 27448.08) * mm, "end": v(8246.87, 25122.29) * mm});
            skLineSegment(sketch, "E1853", {"start": v(8246.87, 25122.29) * mm, "end": v(7624.74, 24933.98) * mm});
            skLineSegment(sketch, "E1854", {"start": v(7113.74, 26691.3) * mm, "end": v(6939.92, 27265.57) * mm});
            skLineSegment(sketch, "E1855", {"start": v(6939.92, 27265.57) * mm, "end": v(7514.19, 27439.4) * mm});
            skLineSegment(sketch, "E1856", {"start": v(7514.19, 27439.4) * mm, "end": v(7688, 26865.12) * mm});
            skLineSegment(sketch, "E1857", {"start": v(7688, 26865.12) * mm, "end": v(7113.74, 26691.3) * mm});
            skLineSegment(sketch, "E1858", {"start": v(7616.05, 24962.7) * mm, "end": v(6920.77, 27259.78) * mm});
            skLineSegment(sketch, "E1859", {"start": v(6920.77, 27259.78) * mm, "end": v(6939.92, 27265.57) * mm});
            skLineSegment(sketch, "E1860", {"start": v(6939.92, 27265.57) * mm, "end": v(7635.2, 24968.49) * mm});
            skLineSegment(sketch, "E1861", {"start": v(7635.2, 24968.49) * mm, "end": v(7616.05, 24962.7) * mm});
            skLineSegment(sketch, "E1862", {"start": v(8208.59, 25110.7) * mm, "end": v(7504.61, 27436.5) * mm});
            skLineSegment(sketch, "E1863", {"start": v(7504.61, 27436.5) * mm, "end": v(7523.76, 27442.29) * mm});
            skLineSegment(sketch, "E1864", {"start": v(7523.76, 27442.29) * mm, "end": v(8227.73, 25116.5) * mm});
            skLineSegment(sketch, "E1865", {"start": v(8227.73, 25116.5) * mm, "end": v(8208.59, 25110.7) * mm});
            skLineSegment(sketch, "E1866", {"start": v(7450.11, 25673.57) * mm, "end": v(7340.03, 26037.28) * mm});
            skLineSegment(sketch, "E1867", {"start": v(7340.03, 26037.28) * mm, "end": v(7847.3, 26190.82) * mm});
            skLineSegment(sketch, "E1868", {"start": v(7847.3, 26190.82) * mm, "end": v(7957.38, 25827.11) * mm});
            skLineSegment(sketch, "E1869", {"start": v(7957.38, 25827.11) * mm, "end": v(7450.11, 25673.57) * mm});
            skLineSegment(sketch, "E1870", {"start": v(7681.7, 25790.4) * mm, "end": v(7596.08, 26073.27) * mm});
            skLineSegment(sketch, "E1871", {"start": v(7596.08, 26073.27) * mm, "end": v(7816.22, 26139.9) * mm});
            skLineSegment(sketch, "E1872", {"start": v(7816.22, 26139.9) * mm, "end": v(7901.84, 25857.02) * mm});
            skLineSegment(sketch, "E1873", {"start": v(7901.84, 25857.02) * mm, "end": v(7681.7, 25790.4) * mm});
            skLineSegment(sketch, "E1874", {"start": v(7782.43, 25826.93) * mm, "end": v(7752.01, 25927.42) * mm});
            skLineSegment(sketch, "E1875", {"start": v(7731.55, 26000.74) * mm, "end": v(7701.13, 26101.24) * mm});
            skLineSegment(sketch, "E1876", {"start": v(7456.1, 25791.38) * mm, "end": v(7389.47, 26011.52) * mm});
            skLineSegment(sketch, "E1877", {"start": v(7389.47, 26011.52) * mm, "end": v(7592.38, 26072.94) * mm});
            skLineSegment(sketch, "E1878", {"start": v(7592.38, 26072.94) * mm, "end": v(7659.01, 25852.8) * mm});
            skLineSegment(sketch, "E1879", {"start": v(7659.01, 25852.8) * mm, "end": v(7456.1, 25791.38) * mm});
            skLineSegment(sketch, "E1880", {"start": v(7477.18, 25710.32) * mm, "end": v(7456.8, 25777.67) * mm});
            skLineSegment(sketch, "E1881", {"start": v(7456.8, 25777.67) * mm, "end": v(7646.17, 25835) * mm});
            skLineSegment(sketch, "E1882", {"start": v(7646.17, 25835) * mm, "end": v(7666.56, 25767.64) * mm});
            skLineSegment(sketch, "E1883", {"start": v(7666.56, 25767.64) * mm, "end": v(7477.18, 25710.32) * mm});
            skEllipse(sketch, "E1884", {"center": v(7534.08, 25764.73) * mm, "majorRadius": 28.27 * mm, "minorRadius": 28.15 * mm, "majorAxis": v(-0.96, -0.29)});
            skLineSegment(sketch, "E1885", {"start": v(7515.83, 25751.85) * mm, "end": v(7511.75, 25765.33) * mm});
            skLineSegment(sketch, "E1886", {"start": v(7511.75, 25765.33) * mm, "end": v(7559.1, 25779.66) * mm});
            skLineSegment(sketch, "E1887", {"start": v(7559.1, 25779.66) * mm, "end": v(7563.18, 25766.19) * mm});
            skLineSegment(sketch, "E1888", {"start": v(7563.18, 25766.19) * mm, "end": v(7515.83, 25751.85) * mm});
            skEllipse(sketch, "E1889", {"center": v(7614.08, 25788.94) * mm, "majorRadius": 28.27 * mm, "minorRadius": 28.15 * mm, "majorAxis": v(-0.96, -0.29)});
            skLineSegment(sketch, "E1890", {"start": v(7593.19, 25775.27) * mm, "end": v(7589.1, 25788.74) * mm});
            skLineSegment(sketch, "E1891", {"start": v(7589.1, 25788.74) * mm, "end": v(7636.45, 25803.07) * mm});
            skLineSegment(sketch, "E1892", {"start": v(7636.45, 25803.07) * mm, "end": v(7640.53, 25789.6) * mm});
            skLineSegment(sketch, "E1893", {"start": v(7640.53, 25789.6) * mm, "end": v(7593.19, 25775.27) * mm});
            skLineSegment(sketch, "E1894", {"start": v(7460.65, 25692.64) * mm, "end": v(7360.76, 26022.67) * mm});
            skLineSegment(sketch, "E1895", {"start": v(7360.76, 26022.67) * mm, "end": v(7834.21, 26165.98) * mm});
            skLineSegment(sketch, "E1896", {"start": v(7834.21, 26165.98) * mm, "end": v(7934.1, 25835.95) * mm});
            skLineSegment(sketch, "E1897", {"start": v(7934.1, 25835.95) * mm, "end": v(7460.65, 25692.64) * mm});
            skLineSegment(sketch, "E1898", {"start": v(7856.78, 26001.67) * mm, "end": v(7780.22, 25978.5) * mm});
            skLineSegment(sketch, "E1899", {"start": v(7835.37, 26083.87) * mm, "end": v(7781.26, 26067.5) * mm});
            skLineSegment(sketch, "E1900", {"start": v(7745.72, 25999.47) * mm, "end": v(7781.09, 26065.54) * mm});
            skLineSegment(sketch, "E1901", {"start": v(7877.04, 25918.81) * mm, "end": v(7833.14, 25905.53) * mm});
            skLineSegment(sketch, "E1902", {"start": v(7770.05, 25939.97) * mm, "end": v(7836.12, 25904.6) * mm});
            skLineSegment(sketch, "E1903", {"start": v(7637.64, 25931.67) * mm, "end": v(7714.2, 25954.85) * mm});
            skLineSegment(sketch, "E1904", {"start": v(7608.91, 26015.12) * mm, "end": v(7663.02, 26031.5) * mm});
            skLineSegment(sketch, "E1905", {"start": v(7730.32, 25994.6) * mm, "end": v(7664.25, 26029.97) * mm});
            skLineSegment(sketch, "E1906", {"start": v(7665.53, 25849.3) * mm, "end": v(7708.66, 25862.35) * mm});
            skLineSegment(sketch, "E1907", {"start": v(7744.03, 25928.43) * mm, "end": v(7708.66, 25862.35) * mm});
            skLineSegment(sketch, "E1908", {"start": v(7618.07, 25963.33) * mm, "end": v(7555.18, 25944.29) * mm});
            skLineSegment(sketch, "E1909", {"start": v(7597.31, 26045.72) * mm, "end": v(7556.22, 26033.28) * mm});
            skLineSegment(sketch, "E1910", {"start": v(7520.68, 25965.26) * mm, "end": v(7556.05, 26031.33) * mm});
            skLineSegment(sketch, "E1911", {"start": v(7649.29, 25880.9) * mm, "end": v(7608.9, 25868.68) * mm});
            skLineSegment(sketch, "E1912", {"start": v(7545.01, 25905.76) * mm, "end": v(7611.08, 25870.4) * mm});
            skLineSegment(sketch, "E1913", {"start": v(7425.75, 25901.45) * mm, "end": v(7489.16, 25920.64) * mm});
            skLineSegment(sketch, "E1914", {"start": v(7398.29, 25985.28) * mm, "end": v(7430.16, 25994.92) * mm});
            skLineSegment(sketch, "E1915", {"start": v(7505.28, 25960.4) * mm, "end": v(7439.2, 25995.76) * mm});
            skLineSegment(sketch, "E1916", {"start": v(7448.32, 25817.84) * mm, "end": v(7483.62, 25828.15) * mm});
            skLineSegment(sketch, "E1917", {"start": v(7518.99, 25894.22) * mm, "end": v(7483.62, 25828.15) * mm});
            skEllipse(sketch, "E1918", {"center": v(7747.52, 25965.14) * mm, "majorRadius": 35.33 * mm, "minorRadius": 35.19 * mm, "majorAxis": v(-0.96, -0.29)});
            skEllipse(sketch, "E1919", {"center": v(7747.52, 25965.14) * mm, "majorRadius": 25 * mm, "minorRadius": 25 * mm, "majorAxis": v(-0.29, 0.96)});
            skEllipse(sketch, "E1920", {"center": v(7522.48, 25930.93) * mm, "majorRadius": 35.33 * mm, "minorRadius": 35.19 * mm, "majorAxis": v(-0.96, -0.29)});
            skEllipse(sketch, "E1921", {"center": v(7522.86, 25931.04) * mm, "majorRadius": 25 * mm, "minorRadius": 25 * mm, "majorAxis": v(-0.29, 0.96)});
            skLineSegment(sketch, "E1922", {"start": v(7616.05, 24962.7) * mm, "end": v(7442.23, 25536.97) * mm});
            skLineSegment(sketch, "E1923", {"start": v(7442.23, 25536.97) * mm, "end": v(8016.5, 25710.79) * mm});
            skLineSegment(sketch, "E1924", {"start": v(8016.5, 25710.79) * mm, "end": v(8190.32, 25136.52) * mm});
            skLineSegment(sketch, "E1925", {"start": v(8190.32, 25136.52) * mm, "end": v(7616.05, 24962.7) * mm});
            skLineSegment(sketch, "E1926", {"start": v(6906.29, 27307.63) * mm, "end": v(6732.47, 27881.9) * mm});
            skLineSegment(sketch, "E1927", {"start": v(6732.47, 27881.9) * mm, "end": v(6751.61, 27887.7) * mm});
            skLineSegment(sketch, "E1928", {"start": v(6751.61, 27887.7) * mm, "end": v(6925.43, 27313.43) * mm});
            skLineSegment(sketch, "E1929", {"start": v(6925.43, 27313.43) * mm, "end": v(6906.29, 27307.63) * mm});
            skLineSegment(sketch, "E1930", {"start": v(6920.77, 27259.78) * mm, "end": v(6914.98, 27278.92) * mm});
            skLineSegment(sketch, "E1931", {"start": v(6914.98, 27278.92) * mm, "end": v(7537.1, 27467.23) * mm});
            skLineSegment(sketch, "E1932", {"start": v(7537.1, 27467.23) * mm, "end": v(7542.9, 27448.08) * mm});
            skLineSegment(sketch, "E1933", {"start": v(7542.9, 27448.08) * mm, "end": v(6920.77, 27259.78) * mm});
            skLineSegment(sketch, "E1934", {"start": v(7287.56, 26117.03) * mm, "end": v(7113.74, 26691.3) * mm});
            skLineSegment(sketch, "E1935", {"start": v(7113.74, 26691.3) * mm, "end": v(7664.08, 26857.88) * mm});
            skLineSegment(sketch, "E1936", {"start": v(7664.08, 26857.88) * mm, "end": v(7837.9, 26283.6) * mm});
            skLineSegment(sketch, "E1937", {"start": v(7837.9, 26283.6) * mm, "end": v(7287.56, 26117.03) * mm});
            skLineSegment(sketch, "E1938", {"start": v(7287.56, 26117.03) * mm, "end": v(7644.94, 26852.08) * mm});
            skLineSegment(sketch, "E1939", {"start": v(7818.76, 26277.81) * mm, "end": v(7113.74, 26691.3) * mm});
            skLineSegment(sketch, "E1940", {"start": v(7624.74, 24933.98) * mm, "end": v(7616.05, 24962.7) * mm});
            skLineSegment(sketch, "E1941", {"start": v(7616.05, 24962.7) * mm, "end": v(7635.2, 24968.49) * mm});
            skLineSegment(sketch, "E1942", {"start": v(7635.2, 24968.49) * mm, "end": v(7643.89, 24939.78) * mm});
            skLineSegment(sketch, "E1943", {"start": v(7643.89, 24939.78) * mm, "end": v(7624.74, 24933.98) * mm});
            skLineSegment(sketch, "E1944", {"start": v(7643.89, 24939.78) * mm, "end": v(7635.2, 24968.49) * mm});
            skLineSegment(sketch, "E1945", {"start": v(7635.2, 24968.49) * mm, "end": v(7662.72, 24976.82) * mm});
            skLineSegment(sketch, "E1946", {"start": v(7662.72, 24976.82) * mm, "end": v(7671.41, 24948.1) * mm});
            skLineSegment(sketch, "E1947", {"start": v(7671.41, 24948.1) * mm, "end": v(7643.89, 24939.78) * mm});
            skLineSegment(sketch, "E1948", {"start": v(7635.2, 24968.49) * mm, "end": v(7671.41, 24948.1) * mm});
            skLineSegment(sketch, "E1949", {"start": v(7643.89, 24939.78) * mm, "end": v(7662.72, 24976.82) * mm});
            skLineSegment(sketch, "E1950", {"start": v(7892.74, 25015.1) * mm, "end": v(7188.77, 27340.9) * mm});
            skLineSegment(sketch, "E1951", {"start": v(7188.77, 27340.9) * mm, "end": v(7504.61, 27436.5) * mm});
            skLineSegment(sketch, "E1952", {"start": v(7504.61, 27436.5) * mm, "end": v(8208.59, 25110.7) * mm});
            skLineSegment(sketch, "E1953", {"start": v(8208.59, 25110.7) * mm, "end": v(7892.74, 25015.1) * mm});
            skLineSegment(sketch, "E1954", {"start": v(7362.59, 26766.62) * mm, "end": v(7188.77, 27340.9) * mm});
            skLineSegment(sketch, "E1955", {"start": v(7504.61, 27436.5) * mm, "end": v(7678.43, 26862.22) * mm});
            skLineSegment(sketch, "E1956", {"start": v(7678.43, 26862.22) * mm, "end": v(7362.59, 26766.62) * mm});
            skLineSegment(sketch, "E1957", {"start": v(7884.05, 25043.81) * mm, "end": v(7710.23, 25618.08) * mm});
            skLineSegment(sketch, "E1958", {"start": v(7710.23, 25618.08) * mm, "end": v(8026.07, 25713.68) * mm});
            skLineSegment(sketch, "E1959", {"start": v(8026.07, 25713.68) * mm, "end": v(8199.9, 25139.41) * mm});
            skLineSegment(sketch, "E1960", {"start": v(8199.9, 25139.41) * mm, "end": v(7884.05, 25043.81) * mm});
            skLineSegment(sketch, "E1961", {"start": v(8026.07, 25713.68) * mm, "end": v(7903.19, 25049.6) * mm});
            skLineSegment(sketch, "E1962", {"start": v(7188.77, 27340.9) * mm, "end": v(7207.9, 27346.69) * mm});
            skLineSegment(sketch, "E1963", {"start": v(7207.9, 27346.69) * mm, "end": v(7381.73, 26772.42) * mm});
            skLineSegment(sketch, "E1964", {"start": v(7381.73, 26772.42) * mm, "end": v(7362.59, 26766.62) * mm});
            skLineSegment(sketch, "E1965", {"start": v(7668.86, 26859.33) * mm, "end": v(7207.9, 27346.69) * mm});
            skLineSegment(sketch, "E1966", {"start": v(7536.4, 26192.35) * mm, "end": v(7362.59, 26766.62) * mm});
            skLineSegment(sketch, "E1967", {"start": v(7362.59, 26766.62) * mm, "end": v(7678.43, 26862.22) * mm});
            skLineSegment(sketch, "E1968", {"start": v(7678.43, 26862.22) * mm, "end": v(7852.25, 26287.95) * mm});
            skLineSegment(sketch, "E1969", {"start": v(7852.25, 26287.95) * mm, "end": v(7536.4, 26192.35) * mm});
            skLineSegment(sketch, "E1970", {"start": v(7381.73, 26772.42) * mm, "end": v(7852.25, 26287.95) * mm});
            skLineSegment(sketch, "E1971", {"start": v(7710.23, 25618.08) * mm, "end": v(7536.4, 26192.35) * mm});
            skLineSegment(sketch, "E1972", {"start": v(7536.4, 26192.35) * mm, "end": v(7852.25, 26287.95) * mm});
            skLineSegment(sketch, "E1973", {"start": v(7852.25, 26287.95) * mm, "end": v(8026.07, 25713.68) * mm});
            skLineSegment(sketch, "E1974", {"start": v(8026.07, 25713.68) * mm, "end": v(7710.23, 25618.08) * mm});
            skLineSegment(sketch, "E1975", {"start": v(7729.37, 25623.88) * mm, "end": v(7852.25, 26287.95) * mm});
            skLineSegment(sketch, "E1976", {"start": v(7362.59, 26766.62) * mm, "end": v(7381.73, 26772.42) * mm});
            skLineSegment(sketch, "E1977", {"start": v(7381.73, 26772.42) * mm, "end": v(7555.55, 26198.15) * mm});
            skLineSegment(sketch, "E1978", {"start": v(7555.55, 26198.15) * mm, "end": v(7536.4, 26192.35) * mm});
            skLineSegment(sketch, "E1979", {"start": v(7536.4, 26192.35) * mm, "end": v(7555.55, 26198.15) * mm});
            skLineSegment(sketch, "E1980", {"start": v(7555.55, 26198.15) * mm, "end": v(7729.37, 25623.88) * mm});
            skLineSegment(sketch, "E1981", {"start": v(7729.37, 25623.88) * mm, "end": v(7710.23, 25618.08) * mm});
            skLineSegment(sketch, "E1982", {"start": v(7710.23, 25618.08) * mm, "end": v(7729.37, 25623.88) * mm});
            skLineSegment(sketch, "E1983", {"start": v(7729.37, 25623.88) * mm, "end": v(7903.19, 25049.6) * mm});
            skLineSegment(sketch, "E1984", {"start": v(7903.19, 25049.6) * mm, "end": v(7884.05, 25043.81) * mm});
            skLineSegment(sketch, "E1985", {"start": v(7892.74, 25015.1) * mm, "end": v(7884.05, 25043.81) * mm});
            skLineSegment(sketch, "E1986", {"start": v(7884.05, 25043.81) * mm, "end": v(7903.19, 25049.6) * mm});
            skLineSegment(sketch, "E1987", {"start": v(7903.19, 25049.6) * mm, "end": v(7911.88, 25020.9) * mm});
            skLineSegment(sketch, "E1988", {"start": v(7911.88, 25020.9) * mm, "end": v(7892.74, 25015.1) * mm});
            skLineSegment(sketch, "E1989", {"start": v(7911.88, 25020.9) * mm, "end": v(7903.19, 25049.6) * mm});
            skLineSegment(sketch, "E1990", {"start": v(7903.19, 25049.6) * mm, "end": v(7930.71, 25057.94) * mm});
            skLineSegment(sketch, "E1991", {"start": v(7930.71, 25057.94) * mm, "end": v(7939.4, 25029.22) * mm});
            skLineSegment(sketch, "E1992", {"start": v(7939.4, 25029.22) * mm, "end": v(7911.88, 25020.9) * mm});
            skLineSegment(sketch, "E1993", {"start": v(7903.19, 25049.6) * mm, "end": v(7939.4, 25029.22) * mm});
            skLineSegment(sketch, "E1994", {"start": v(7911.88, 25020.9) * mm, "end": v(7930.71, 25057.94) * mm});
            skLineSegment(sketch, "E1995", {"start": v(6732.47, 27881.9) * mm, "end": v(6723.78, 27910.62) * mm});
            skLineSegment(sketch, "E1996", {"start": v(6723.78, 27910.62) * mm, "end": v(6742.92, 27916.41) * mm});
            skLineSegment(sketch, "E1997", {"start": v(6742.92, 27916.41) * mm, "end": v(6751.61, 27887.7) * mm});
            skLineSegment(sketch, "E1998", {"start": v(6751.61, 27887.7) * mm, "end": v(6732.47, 27881.9) * mm});
            skLineSegment(sketch, "E1999", {"start": v(6751.61, 27887.7) * mm, "end": v(6742.92, 27916.41) * mm});
            skLineSegment(sketch, "E2000", {"start": v(6742.92, 27916.41) * mm, "end": v(6770.45, 27924.74) * mm});
            skLineSegment(sketch, "E2001", {"start": v(6770.45, 27924.74) * mm, "end": v(6779.14, 27896.03) * mm});
            skLineSegment(sketch, "E2002", {"start": v(6779.14, 27896.03) * mm, "end": v(6751.61, 27887.7) * mm});
            skLineSegment(sketch, "E2003", {"start": v(6742.92, 27916.41) * mm, "end": v(6779.14, 27896.03) * mm});
            skLineSegment(sketch, "E2004", {"start": v(6751.61, 27887.7) * mm, "end": v(6770.45, 27924.74) * mm});
            skLineSegment(sketch, "E2005", {"start": v(7442.23, 25536.97) * mm, "end": v(7268.41, 26111.24) * mm});
            skLineSegment(sketch, "E2006", {"start": v(7268.41, 26111.24) * mm, "end": v(7842.68, 26285.06) * mm});
            skLineSegment(sketch, "E2007", {"start": v(7842.68, 26285.06) * mm, "end": v(8016.5, 25710.79) * mm});
            skLineSegment(sketch, "E2008", {"start": v(8016.5, 25710.79) * mm, "end": v(7442.23, 25536.97) * mm});
            skLineSegment(sketch, "E2009", {"start": v(6771.72, 27282.86) * mm, "end": v(6752.46, 27882.55) * mm});
            skLineSegment(sketch, "E2010", {"start": v(6752.46, 27882.55) * mm, "end": v(6732.47, 27881.9) * mm});
            skLineSegment(sketch, "E2011", {"start": v(6732.47, 27881.9) * mm, "end": v(6751.73, 27282.21) * mm});
            skLineSegment(sketch, "E2012", {"start": v(6751.73, 27282.21) * mm, "end": v(6771.72, 27282.86) * mm});
            skArc(sketch, "E2013", {"start": v(6751.73, 27282.21) * mm, "mid": v(6829.84, 27289.86) * mm, "end": v(6906.29, 27307.63) * mm});
            skLineSegment(sketch, "E2014", {"start": v(6732.47, 27881.9) * mm, "end": v(7306.74, 28055.72) * mm});
            skLineSegment(sketch, "E2015", {"start": v(7306.74, 28055.72) * mm, "end": v(7480.56, 27481.45) * mm});
            skLineSegment(sketch, "E2016", {"start": v(7480.56, 27481.45) * mm, "end": v(6906.29, 27307.63) * mm});
            skLineSegment(sketch, "E2017", {"start": v(7306.74, 28055.72) * mm, "end": v(6925.43, 27313.43) * mm});
            skLineSegment(sketch, "E2018", {"start": v(6751.61, 27887.7) * mm, "end": v(7480.56, 27481.45) * mm});
            skLineSegment(sketch, "E2019", {"start": v(6934.12, 27284.71) * mm, "end": v(6925.43, 27313.43) * mm});
            skLineSegment(sketch, "E2020", {"start": v(6925.43, 27313.43) * mm, "end": v(6944.57, 27319.22) * mm});
            skLineSegment(sketch, "E2021", {"start": v(6944.57, 27319.22) * mm, "end": v(6953.26, 27290.5) * mm});
            skLineSegment(sketch, "E2022", {"start": v(6953.26, 27290.5) * mm, "end": v(6934.12, 27284.71) * mm});
            skLineSegment(sketch, "E2023", {"start": v(6953.26, 27290.5) * mm, "end": v(6944.57, 27319.22) * mm});
            skLineSegment(sketch, "E2024", {"start": v(6944.57, 27319.22) * mm, "end": v(6972.1, 27327.55) * mm});
            skLineSegment(sketch, "E2025", {"start": v(6972.1, 27327.55) * mm, "end": v(6980.79, 27298.84) * mm});
            skLineSegment(sketch, "E2026", {"start": v(6980.79, 27298.84) * mm, "end": v(6953.26, 27290.5) * mm});
            skLineSegment(sketch, "E2027", {"start": v(6944.57, 27319.22) * mm, "end": v(6980.79, 27298.84) * mm});
            skLineSegment(sketch, "E2028", {"start": v(6953.26, 27290.5) * mm, "end": v(6972.1, 27327.55) * mm});
            skLineSegment(sketch, "E2029", {"start": v(2727.74, 31147.01) * mm, "end": v(-4048.13, 29096.1) * mm});
            skLineSegment(sketch, "E2030", {"start": v(3637.83, 40953.93) * mm, "end": v(10124.78, 19522.2) * mm});
            skLineSegment(sketch, "E2031", {"start": v(-2736.57, 39024.53) * mm, "end": v(3750.38, 17592.8) * mm});
            skLineSegment(sketch, "E2032", {"start": v(-5129.37, 38300.28) * mm, "end": v(1357.59, 16868.54) * mm});
            skCircle(sketch, "E2033", {"center": v(-5245.25, 38683.12) * mm, "radius": 400 * mm});
            skCircle(sketch, "E2034", {"center": v(-2852.45, 39407.37) * mm, "radius": 400 * mm});
            skCircle(sketch, "E2035", {"center": v(3521.95, 41336.78) * mm, "radius": 400 * mm});
            skCircle(sketch, "E2036", {"center": v(-6386.26, 35440.86) * mm, "radius": 400 * mm});
            skLineSegment(sketch, "E2037", {"start": v(1232.56, 37746.92) * mm, "end": v(-6002.92, 35556.9) * mm});
            skFitSpline(sketch, "E2038", {"points": [v(4051.69, 27214.27) * mm, v(4006.1, 27242.45) * mm, v(3955.36, 27336.86) * mm, v(3958.58, 27444.03) * mm, v(4014.98, 27535.28) * mm, v(4109.4, 27586.09) * mm, v(4216.54, 27582.92) * mm, v(4307.72, 27526.55) * mm, v(4358.46, 27432.14) * mm, v(4355.23, 27324.97) * mm, v(4298.83, 27233.73) * mm, v(4204.42, 27182.92) * mm, v(4097.28, 27186.09) * mm, v(4051.69, 27214.27) * mm]});
            skFitSpline(sketch, "E2039", {"points": [v(915.1, 33441.4) * mm, v(829.93, 33415.63) * mm, v(736.7, 33457.65) * mm]});
            skFitSpline(sketch, "E2040", {"points": [v(775.65, 33328.96) * mm, v(829.93, 33415.63) * mm, v(915.1, 33441.4) * mm]});
            skFitSpline(sketch, "E2041", {"points": [v(623.66, 34404.27) * mm, v(538.5, 34378.49) * mm, v(445.26, 34420.51) * mm]});
            skFitSpline(sketch, "E2042", {"points": [v(484.21, 34291.82) * mm, v(538.5, 34378.49) * mm, v(623.66, 34404.27) * mm]});
            skFitSpline(sketch, "E2043", {"points": [v(332.2, 35367.18) * mm, v(247.04, 35341.4) * mm, v(153.8, 35383.42) * mm]});
            skFitSpline(sketch, "E2044", {"points": [v(192.76, 35254.73) * mm, v(247.04, 35341.4) * mm, v(332.2, 35367.18) * mm]});
            skFitSpline(sketch, "E2045", {"points": [v(186.49, 35848.6) * mm, v(101.32, 35822.83) * mm, v(8.09, 35864.85) * mm]});
            skFitSpline(sketch, "E2046", {"points": [v(3317.81, 34493.6) * mm, v(3292.03, 34578.78) * mm, v(3334.06, 34672) * mm]});
            skFitSpline(sketch, "E2047", {"points": [v(3205.36, 34633.06) * mm, v(3292.03, 34578.78) * mm, v(3317.81, 34493.6) * mm]});
            skFitSpline(sketch, "E2048", {"points": [v(4280.67, 34785.05) * mm, v(4254.9, 34870.22) * mm, v(4296.91, 34963.45) * mm]});
            skFitSpline(sketch, "E2049", {"points": [v(4168.22, 34924.5) * mm, v(4254.9, 34870.22) * mm, v(4280.67, 34785.05) * mm]});
            skFitSpline(sketch, "E2050", {"points": [v(4770.27, 35107.64) * mm, v(4733.8, 35016.25) * mm, v(4759.53, 34931.27) * mm]});
            skSolve(sketch);
        }
        {
            var Q0;
            Q0=qCreatedBy(makeId("Top.planeOp"),FACE);
            var Q1;
            Q1=qCreatedBy(makeId("Top.planeOp"),FACE);
            var Q2;
            Q2=qCreatedBy(makeId("Top.planeOp"),FACE);
            var sketch = newSketch(context, id + "F1", { "sketchPlane" : qUnion([Q0, Q1, Q2])});
            skLineSegment(sketch, "E2051.0", {"start": v(8303.3, 25022.24) * mm, "end": v(8590.44, 25109.15) * mm});
            skLineSegment(sketch, "E2051.1", {"start": v(8275.24, 25028.58) * mm, "end": v(7643.52, 24837.37) * mm});
            skLineSegment(sketch, "E2051.4", {"start": v(8246.85, 25122.28) * mm, "end": v(7345.9, 28098.92) * mm});
            skLineSegment(sketch, "E2051.5", {"start": v(7345.9, 28098.92) * mm, "end": v(6714.19, 27907.71) * mm});
            skLineSegment(sketch, "E2051.6", {"start": v(6714.19, 27907.71) * mm, "end": v(6686.09, 28000.55) * mm});
            skLineSegment(sketch, "E2051.9", {"start": v(7106.28, 28127.74) * mm, "end": v(6323.55, 30713.74) * mm});
            skLineSegment(sketch, "E2051.10", {"start": v(6323.55, 30713.74) * mm, "end": v(6018.23, 30621.33) * mm});
            skLineSegment(sketch, "E2051.11", {"start": v(6018.23, 30621.33) * mm, "end": v(5596.86, 32013.45) * mm});
            skLineSegment(sketch, "E2051.13", {"start": v(6057.79, 32277.66) * mm, "end": v(3665, 31553.41) * mm});
            skLineSegment(sketch, "E2051.14", {"start": v(5539.28, 33990.02) * mm, "end": v(6057.79, 32277.66) * mm});
            skLineSegment(sketch, "E2051.16", {"start": v(1038.97, 28597.26) * mm, "end": v(1585.97, 29073.44) * mm});
            skLineSegment(sketch, "E2051.24", {"start": v(981.9, 30734.55) * mm, "end": v(-2157.46, 29784.33) * mm});
            skLineSegment(sketch, "E2051.25", {"start": v(-2157.46, 29784.33) * mm, "end": v(-2347.02, 30410.5) * mm});
            skLineSegment(sketch, "E2051.27", {"start": v(-3425.5, 33295.77) * mm, "end": v(-2534.67, 30352.63) * mm});
            skLineSegment(sketch, "E2051.29", {"start": v(-281.93, 34299.42) * mm, "end": v(578.47, 34559.84) * mm});
            skLineSegment(sketch, "E2051.31", {"start": v(-622.8, 35013.09) * mm, "end": v(-861.8, 34940.5) * mm});
            skLineSegment(sketch, "E2051.32", {"start": v(-977.95, 36186.57) * mm, "end": v(-902.73, 35938) * mm});
            skLineSegment(sketch, "E2051.33", {"start": v(-710, 34438.17) * mm, "end": v(-3559.9, 33575.84) * mm});
            skLineSegment(sketch, "E2051.34", {"start": v(-861.8, 34940.5) * mm, "end": v(-710, 34438.17) * mm});
            skLineSegment(sketch, "E2051.35", {"start": v(-3973.74, 34943.1) * mm, "end": v(-3685.65, 35030.3) * mm});
            skLineSegment(sketch, "E2051.36", {"start": v(-3559.9, 33575.84) * mm, "end": v(-3973.74, 34943.1) * mm});
            skLineSegment(sketch, "E2051.37", {"start": v(-3685.65, 35030.3) * mm, "end": v(-3957.95, 35930) * mm});
            skLineSegment(sketch, "E2051.41", {"start": v(7597.64, 21063) * mm, "end": v(9116.94, 21522.85) * mm});
            skLineSegment(sketch, "E2051.42", {"start": v(9116.94, 21522.85) * mm, "end": v(8459.27, 23695.52) * mm});
            skLineSegment(sketch, "E2051.43", {"start": v(8459.27, 23695.52) * mm, "end": v(8971.72, 23850.63) * mm});
            skLineSegment(sketch, "E2051.45", {"start": v(383.02, 32713.3) * mm, "end": v(681.08, 31728.48) * mm});
            skLineSegment(sketch, "E2051.46", {"start": v(688.47, 32038.93) * mm, "end": v(503.96, 32648.57) * mm});
            skLineSegment(sketch, "E2051.47", {"start": v(1870.5, 32396.71) * mm, "end": v(1711.8, 32348.67) * mm});
            skLineSegment(sketch, "E2051.48", {"start": v(3194.1, 32695.99) * mm, "end": v(2994.87, 32635.69) * mm});
            skLineSegment(sketch, "E2051.49", {"start": v(2368.65, 31137.53) * mm, "end": v(3556.94, 31497.2) * mm});
            skLineSegment(sketch, "E2051.50", {"start": v(2396.47, 31045.6) * mm, "end": v(2368.65, 31137.53) * mm});
            skLineSegment(sketch, "E2051.51", {"start": v(3665, 31553.41) * mm, "end": v(3596, 31781.37) * mm});
            skLineSegment(sketch, "E2051.52", {"start": v(3556.94, 31497.2) * mm, "end": v(3481.43, 31746.7) * mm});
            skLineSegment(sketch, "E2051.53", {"start": v(4630.34, 33714.9) * mm, "end": v(5539.28, 33990.02) * mm});
            skLineSegment(sketch, "E2051.54", {"start": v(4569.53, 33915.8) * mm, "end": v(4630.34, 33714.9) * mm});
            skLineSegment(sketch, "E2051.55", {"start": v(3803.84, 33684.03) * mm, "end": v(4569.53, 33915.8) * mm});
            skLineSegment(sketch, "E2051.56", {"start": v(3864.66, 33483.1) * mm, "end": v(3803.84, 33684.03) * mm});
            skLineSegment(sketch, "E2051.57", {"start": v(3146.69, 33265.8) * mm, "end": v(3864.66, 33483.1) * mm});
            skLineSegment(sketch, "E2051.58", {"start": v(2703.65, 34316.33) * mm, "end": v(3166, 32788.83) * mm});
            skLineSegment(sketch, "E2051.59", {"start": v(3166, 32788.83) * mm, "end": v(2966.77, 32728.53) * mm});
            skLineSegment(sketch, "E2051.60", {"start": v(1685.98, 33006.34) * mm, "end": v(1870.5, 32396.71) * mm});
            skLineSegment(sketch, "E2051.61", {"start": v(503.96, 32648.57) * mm, "end": v(1685.98, 33006.34) * mm});
            skLineSegment(sketch, "E2051.63", {"start": v(1657.88, 33099.18) * mm, "end": v(615.22, 36543.93) * mm});
            skLineSegment(sketch, "E2051.66", {"start": v(615.22, 36543.93) * mm, "end": v(-828.96, 36106.8) * mm});
            skLineSegment(sketch, "E2051.67", {"start": v(-831.43, 36230.92) * mm, "end": v(-977.95, 36186.57) * mm});
            skLineSegment(sketch, "E2051.68", {"start": v(-1009.44, 36822.46) * mm, "end": v(-831.43, 36230.92) * mm});
            skLineSegment(sketch, "E2051.69", {"start": v(-3957.95, 35930) * mm, "end": v(-1009.44, 36822.46) * mm});
            skLineSegment(sketch, "E2051.70", {"start": v(561.48, 37297.94) * mm, "end": v(2030.34, 32445.09) * mm});
            skLineSegment(sketch, "E2051.72", {"start": v(817.35, 37375.45) * mm, "end": v(4399.01, 37834.91) * mm});
            skLineSegment(sketch, "E2051.74", {"start": v(5411.97, 34488.28) * mm, "end": v(2976.11, 33751) * mm});
            skLineSegment(sketch, "E2051.76", {"start": v(2976.11, 33751) * mm, "end": v(2796.5, 34344.43) * mm});
            skLineSegment(sketch, "E2052.1", {"start": v(734.61, 37774.63) * mm, "end": v(3515.53, 38130.64) * mm});
            skLineSegment(sketch, "E2053", {"start": v(2396.47, 31045.6) * mm, "end": v(5596.86, 32013.45) * mm});
            skLineSegment(sketch, "E2054", {"start": v(-2534.67, 30352.63) * mm, "end": v(-2347.02, 30410.5) * mm});
            skLineSegment(sketch, "E2055", {"start": v(4693.12, 37985.2) * mm, "end": v(3515.53, 38130.64) * mm});
            skLineSegment(sketch, "E2056", {"start": v(2703.65, 34316.33) * mm, "end": v(2796.5, 34344.43) * mm});
            skLineSegment(sketch, "E2057", {"start": v(578.47, 34559.84) * mm, "end": v(592.96, 34511.99) * mm});
            skLineSegment(sketch, "E2058", {"start": v(-281.93, 34299.42) * mm, "end": v(-544.23, 35166.06) * mm});
            skLineSegment(sketch, "E2059", {"start": v(8275.24, 25028.58) * mm, "end": v(8303.3, 25022.24) * mm});
            skLineSegment(sketch, "E2060", {"start": v(6686.09, 28000.55) * mm, "end": v(7106.28, 28127.74) * mm});
            skLineSegment(sketch, "E2061", {"start": v(817.35, 37375.45) * mm, "end": v(561.48, 37297.94) * mm});
            skLineSegment(sketch, "E2062", {"start": v(-3425.5, 33295.77) * mm, "end": v(592.96, 34511.99) * mm});
            skLineSegment(sketch, "E2063", {"start": v(1038.97, 28597.26) * mm, "end": v(7597.64, 21063) * mm});
            skLineSegment(sketch, "E2064", {"start": v(383.02, 32713.3) * mm, "end": v(1657.88, 33099.18) * mm});
            skLineSegment(sketch, "E2065", {"start": v(1585.97, 29073.44) * mm, "end": v(1490.98, 29387.32) * mm});
            skLineSegment(sketch, "E2066", {"start": v(7643.52, 24837.37) * mm, "end": v(7615.16, 24931.08) * mm});
            skLineSegment(sketch, "E2067", {"start": v(8246.85, 25122.28) * mm, "end": v(7615.16, 24931.08) * mm});
            skLineSegment(sketch, "E2068", {"start": v(5411.97, 34488.28) * mm, "end": v(4399.01, 37834.91) * mm});
            skLineSegment(sketch, "E2069", {"start": v(4693.12, 37985.2) * mm, "end": v(8590.44, 25109.15) * mm});
            skLineSegment(sketch, "E2070", {"start": v(8971.72, 23850.63) * mm, "end": v(9919.68, 20721.66) * mm});
            skLineSegment(sketch, "E2071", {"start": v(9919.68, 20721.66) * mm, "end": v(7849.46, 20094.46) * mm});
            skLineSegment(sketch, "E2072", {"start": v(7849.46, 20094.46) * mm, "end": v(-620.1, 29823.84) * mm});
            skLineSegment(sketch, "E2073", {"start": v(-620.1, 29823.84) * mm, "end": v(-2682.94, 29199.46) * mm});
            skLineSegment(sketch, "E2074", {"start": v(-2682.94, 29199.46) * mm, "end": v(-4773.82, 36107.33) * mm});
            skLineSegment(sketch, "E2075", {"start": v(734.61, 37774.63) * mm, "end": v(-4773.82, 36107.33) * mm});
            skLineSegment(sketch, "E2076", {"start": v(187.3, 30366.58) * mm, "end": v(1017.23, 30617.78) * mm});
            skLineSegment(sketch, "E2077", {"start": v(187.3, 30366.58) * mm, "end": v(247, 30169.35) * mm});
            skLineSegment(sketch, "E2078", {"start": v(-209.3, 30031.2) * mm, "end": v(247, 30169.35) * mm});
            skLineSegment(sketch, "E2079", {"start": v(975.28, 28670.43) * mm, "end": v(-209.3, 30031.2) * mm});
            skLineSegment(sketch, "E2080", {"start": v(975.28, 28670.43) * mm, "end": v(1474.96, 29105.4) * mm});
            skLineSegment(sketch, "E2081", {"start": v(1474.96, 29105.4) * mm, "end": v(1398.14, 29359.22) * mm});
            skLineSegment(sketch, "E2082", {"start": v(1398.14, 29359.22) * mm, "end": v(1490.98, 29387.32) * mm});
            skLineSegment(sketch, "E2083", {"start": v(1093.63, 30365.34) * mm, "end": v(1186.48, 30393.43) * mm});
            skLineSegment(sketch, "E2084.trimOffspring", {"start": v(1186.48, 30393.43) * mm, "end": v(1003.85, 30996.86) * mm});
            skLineSegment(sketch, "E2085.trimOffspring", {"start": v(1093.63, 30365.34) * mm, "end": v(1017.23, 30617.78) * mm});
            skLineSegment(sketch, "E2086", {"start": v(911, 30968.76) * mm, "end": v(1003.85, 30996.86) * mm});
            skLineSegment(sketch, "E2087", {"start": v(681.08, 31728.48) * mm, "end": v(773.92, 31756.58) * mm});
            skLineSegment(sketch, "E2088.trimOffspring", {"start": v(773.92, 31756.58) * mm, "end": v(716.57, 31946.1) * mm});
            skLineSegment(sketch, "E2089.trimOffspring", {"start": v(911, 30968.76) * mm, "end": v(981.9, 30734.55) * mm});
            skLineSegment(sketch, "E2090.trimOffspring", {"start": v(3481.43, 31746.7) * mm, "end": v(3596, 31781.37) * mm});
            skLineSegment(sketch, "E2091.trimOffspring", {"start": v(3251.48, 32506.41) * mm, "end": v(3194.1, 32695.99) * mm});
            skLineSegment(sketch, "E2092.trimOffspring", {"start": v(3366.04, 32541.08) * mm, "end": v(3146.69, 33265.8) * mm});
            skLineSegment(sketch, "E2093.trimOffspring", {"start": v(3251.48, 32506.41) * mm, "end": v(3366.04, 32541.08) * mm});
            skLineSegment(sketch, "E2094", {"start": v(862.55, 31990.28) * mm, "end": v(834.45, 32083.12) * mm});
            skLineSegment(sketch, "E2095", {"start": v(1739.9, 32255.83) * mm, "end": v(1711.8, 32348.67) * mm});
            skLineSegment(sketch, "E2096.trimOffspring", {"start": v(862.55, 31990.28) * mm, "end": v(716.57, 31946.1) * mm});
            skLineSegment(sketch, "E2097.trimOffspring", {"start": v(834.45, 32083.12) * mm, "end": v(688.47, 32038.93) * mm});
            skLineSegment(sketch, "E2098", {"start": v(-788.35, 35972.62) * mm, "end": v(-902.73, 35938) * mm});
            skLineSegment(sketch, "E2099", {"start": v(-544.23, 35166.06) * mm, "end": v(-658.62, 35131.44) * mm});
            skLineSegment(sketch, "E2100.trimOffspring", {"start": v(-658.62, 35131.44) * mm, "end": v(-622.8, 35013.09) * mm});
            skLineSegment(sketch, "E2101.trimOffspring", {"start": v(-788.35, 35972.62) * mm, "end": v(-828.96, 36106.8) * mm});
            skLineSegment(sketch, "E2102", {"start": v(2241.17, 32407.56) * mm, "end": v(2213.07, 32500.4) * mm});
            skLineSegment(sketch, "E2103", {"start": v(2994.87, 32635.69) * mm, "end": v(2966.77, 32728.53) * mm});
            skLineSegment(sketch, "E2104.trimOffspring", {"start": v(2213.07, 32500.4) * mm, "end": v(2030.34, 32445.09) * mm});
            skLineSegment(sketch, "E2105.trimOffspring", {"start": v(2241.17, 32407.56) * mm, "end": v(1739.9, 32255.83) * mm});
            skFitSpline(sketch, "E2106.0", {"points": [v(4051.69, 27214.27) * mm, v(4006.1, 27242.45) * mm, v(3955.36, 27336.86) * mm, v(3958.58, 27444.03) * mm, v(4014.98, 27535.28) * mm, v(4109.4, 27586.09) * mm, v(4216.54, 27582.92) * mm, v(4307.72, 27526.55) * mm, v(4358.46, 27432.14) * mm, v(4355.23, 27324.97) * mm, v(4298.83, 27233.73) * mm, v(4204.42, 27182.92) * mm, v(4097.28, 27186.09) * mm, v(4051.69, 27214.27) * mm]});
            skSolve(sketch);
        }
        {
            var Q0;
            Q0 = qSketchRegion(id + "F1", true);
            extrude(context, id + "F2", {"entities" : qUnion([Q0]), "depth" : (2930 - 130) * mm, "offsetDistance" : 25 * mm});
        }
        {
            var Q0;
            Q0=qCreatedBy(makeId("Top.planeOp"),FACE);
            var Q1;
            Q1=qCreatedBy(makeId("Top.planeOp"),FACE);
            var sketch = newSketch(context, id + "F3", { "sketchPlane" : qUnion([Q0, Q1])});
            skLineSegment(sketch, "E2107.0", {"start": v(7849.46, 20094.46) * mm, "end": v(-620.1, 29823.84) * mm});
            skLineSegment(sketch, "E2107.1", {"start": v(9919.68, 20721.66) * mm, "end": v(7849.46, 20094.46) * mm});
            skLineSegment(sketch, "E2107.2", {"start": v(8971.72, 23850.63) * mm, "end": v(9919.68, 20721.66) * mm});
            skLineSegment(sketch, "E2107.3", {"start": v(4693.12, 37985.2) * mm, "end": v(8590.44, 25109.15) * mm});
            skLineSegment(sketch, "E2107.4", {"start": v(4693.12, 37985.2) * mm, "end": v(3515.53, 38130.64) * mm});
            skLineSegment(sketch, "E2107.5", {"start": v(734.61, 37774.63) * mm, "end": v(3515.53, 38130.64) * mm});
            skLineSegment(sketch, "E2107.6", {"start": v(734.61, 37774.63) * mm, "end": v(-4773.82, 36107.33) * mm});
            skLineSegment(sketch, "E2107.7", {"start": v(-2682.94, 29199.46) * mm, "end": v(-4773.82, 36107.33) * mm});
            skLineSegment(sketch, "E2107.8", {"start": v(-620.1, 29823.84) * mm, "end": v(-2682.94, 29199.46) * mm});
            skLineSegment(sketch, "E2108", {"start": v(8971.72, 23850.63) * mm, "end": v(8590.44, 25109.15) * mm});
            skSolve(sketch);
        }
        {
            var Q0;
            Q0 = qSketchRegion(id + "F3", true);
            extrude(context, id + "F4", {"entities" : qUnion([Q0]), "operationType" : NewBodyOperationType.ADD, "oppositeDirection" : true, "depth" : 130 * mm, "offsetDistance" : 25 * mm});
        }
        {
            var Q0;
            Q0=makeQuery(id+"F4.boolean.opBoolean","MERGE",FACE,{"derivedFrom":[makeQuery(id+"F2.opExtrude","SWEPT_FACE",FACE,{"disambiguationData":[OSD([sQuery(id+"F1.wireOp",EDGE,"E2069")])]}),makeQuery(id+"F4.opExtrude","SWEPT_FACE",FACE,{"disambiguationData":[OSD([sQuery(id+"F3.wireOp",EDGE,"E2107.3")])]})]});
            var sketch = newSketch(context, id + "F5", { "sketchPlane" : qUnion([Q0])});
            skArc(sketch, "E2109", {"start": v(20805.83, 2757.57) * mm, "mid": v(20780.83, 2782.57) * mm, "end": v(20755.83, 2757.57) * mm});
            skArc(sketch, "E2110.1.0.0", {"start": v(20855.83, 2757.57) * mm, "mid": v(20830.83, 2782.57) * mm, "end": v(20805.83, 2757.57) * mm});
            skArc(sketch, "E2110.2.0.0", {"start": v(20905.83, 2757.57) * mm, "mid": v(20880.83, 2782.57) * mm, "end": v(20855.83, 2757.57) * mm});
            skArc(sketch, "E2110.3.0.0", {"start": v(20955.83, 2757.57) * mm, "mid": v(20930.83, 2782.57) * mm, "end": v(20905.83, 2757.57) * mm});
            skLineSegment(sketch, "E2110.direction1", {"start": v(20780.83, 2757.57) * mm, "end": v(20830.83, 2757.57) * mm, "construction": true});
            skLineSegment(sketch, "E2111", {"start": v(20745.83, 2800) * mm, "end": v(20745.83, 2740) * mm});
            skLineSegment(sketch, "E2112", {"start": v(20745.83, 2740) * mm, "end": v(20965.83, 2740) * mm});
            skLineSegment(sketch, "E2113", {"start": v(20965.83, 2740) * mm, "end": v(20965.83, 2800) * mm});
            skLineSegment(sketch, "E2114.0", {"start": v(27069.95, 2800) * mm, "end": v(17958.73, 2800) * mm, "construction": true});
            skLineSegment(sketch, "E2115", {"start": v(20745.83, 2800) * mm, "end": v(20755.83, 2800) * mm});
            skLineSegment(sketch, "E2116", {"start": v(20955.83, 2800) * mm, "end": v(20965.83, 2800) * mm});
            skLineSegment(sketch, "E2117", {"start": v(20745.83, 2757.57) * mm, "end": v(20965.83, 2757.57) * mm, "construction": true});
            skLineSegment(sketch, "E2118", {"start": v(20955.83, 2757.57) * mm, "end": v(20955.83, 2800) * mm});
            skLineSegment(sketch, "E2119", {"start": v(20755.83, 2800) * mm, "end": v(20755.83, 2757.57) * mm});
            skSolve(sketch);
        }
        {
            var Q0;
            Q0=makeQuery(id+"F2.opExtrude","CAP_FACE",FACE,{"disambiguationData":[OSD([sQuery(id+"F1.wireOp",EDGE,"E2051.0"),sQuery(id+"F1.wireOp",EDGE,"E2051.1"),sQuery(id+"F1.wireOp",EDGE,"E2051.4"),sQuery(id+"F1.wireOp",EDGE,"E2051.5"),sQuery(id+"F1.wireOp",EDGE,"E2051.6"),sQuery(id+"F1.wireOp",EDGE,"E2051.9"),sQuery(id+"F1.wireOp",EDGE,"E2051.10"),sQuery(id+"F1.wireOp",EDGE,"E2051.11"),sQuery(id+"F1.wireOp",EDGE,"E2051.13"),sQuery(id+"F1.wireOp",EDGE,"E2051.14"),sQuery(id+"F1.wireOp",EDGE,"E2051.16"),sQuery(id+"F1.wireOp",EDGE,"E2051.24"),sQuery(id+"F1.wireOp",EDGE,"E2051.25"),sQuery(id+"F1.wireOp",EDGE,"E2051.27"),sQuery(id+"F1.wireOp",EDGE,"E2051.29"),sQuery(id+"F1.wireOp",EDGE,"E2051.31"),sQuery(id+"F1.wireOp",EDGE,"E2051.32"),sQuery(id+"F1.wireOp",EDGE,"E2051.33"),sQuery(id+"F1.wireOp",EDGE,"E2051.34"),sQuery(id+"F1.wireOp",EDGE,"E2051.35"),sQuery(id+"F1.wireOp",EDGE,"E2051.36"),sQuery(id+"F1.wireOp",EDGE,"E2051.37"),sQuery(id+"F1.wireOp",EDGE,"E2051.41"),sQuery(id+"F1.wireOp",EDGE,"E2051.42"),sQuery(id+"F1.wireOp",EDGE,"E2051.43"),sQuery(id+"F1.wireOp",EDGE,"E2051.45"),sQuery(id+"F1.wireOp",EDGE,"E2051.46"),sQuery(id+"F1.wireOp",EDGE,"E2051.47"),sQuery(id+"F1.wireOp",EDGE,"E2051.48"),sQuery(id+"F1.wireOp",EDGE,"E2051.49"),sQuery(id+"F1.wireOp",EDGE,"E2051.50"),sQuery(id+"F1.wireOp",EDGE,"E2051.51"),sQuery(id+"F1.wireOp",EDGE,"E2051.52"),sQuery(id+"F1.wireOp",EDGE,"E2051.53"),sQuery(id+"F1.wireOp",EDGE,"E2051.54"),sQuery(id+"F1.wireOp",EDGE,"E2051.55"),sQuery(id+"F1.wireOp",EDGE,"E2051.56"),sQuery(id+"F1.wireOp",EDGE,"E2051.57"),sQuery(id+"F1.wireOp",EDGE,"E2051.58"),sQuery(id+"F1.wireOp",EDGE,"E2051.59"),sQuery(id+"F1.wireOp",EDGE,"E2051.60"),sQuery(id+"F1.wireOp",EDGE,"E2051.61"),sQuery(id+"F1.wireOp",EDGE,"E2051.63"),sQuery(id+"F1.wireOp",EDGE,"E2051.66"),sQuery(id+"F1.wireOp",EDGE,"E2051.67"),sQuery(id+"F1.wireOp",EDGE,"E2051.68"),sQuery(id+"F1.wireOp",EDGE,"E2051.69"),sQuery(id+"F1.wireOp",EDGE,"E2051.70"),sQuery(id+"F1.wireOp",EDGE,"E2051.72"),sQuery(id+"F1.wireOp",EDGE,"E2051.74"),sQuery(id+"F1.wireOp",EDGE,"E2051.76"),sQuery(id+"F1.wireOp",EDGE,"E2052.1"),sQuery(id+"F1.wireOp",EDGE,"E2053"),sQuery(id+"F1.wireOp",EDGE,"E2054"),sQuery(id+"F1.wireOp",EDGE,"E2055"),sQuery(id+"F1.wireOp",EDGE,"E2056"),sQuery(id+"F1.wireOp",EDGE,"E2057"),sQuery(id+"F1.wireOp",EDGE,"E2058"),sQuery(id+"F1.wireOp",EDGE,"E2059"),sQuery(id+"F1.wireOp",EDGE,"E2060"),sQuery(id+"F1.wireOp",EDGE,"E2061"),sQuery(id+"F1.wireOp",EDGE,"E2062"),sQuery(id+"F1.wireOp",EDGE,"E2063"),sQuery(id+"F1.wireOp",EDGE,"E2064"),sQuery(id+"F1.wireOp",EDGE,"E2065"),sQuery(id+"F1.wireOp",EDGE,"E2066"),sQuery(id+"F1.wireOp",EDGE,"E2067"),sQuery(id+"F1.wireOp",EDGE,"E2068"),sQuery(id+"F1.wireOp",EDGE,"E2069"),sQuery(id+"F1.wireOp",EDGE,"E2070"),sQuery(id+"F1.wireOp",EDGE,"E2071"),sQuery(id+"F1.wireOp",EDGE,"E2072"),sQuery(id+"F1.wireOp",EDGE,"E2073"),sQuery(id+"F1.wireOp",EDGE,"E2074"),sQuery(id+"F1.wireOp",EDGE,"E2075"),sQuery(id+"F1.wireOp",EDGE,"E2076"),sQuery(id+"F1.wireOp",EDGE,"E2077"),sQuery(id+"F1.wireOp",EDGE,"E2078"),sQuery(id+"F1.wireOp",EDGE,"E2079"),sQuery(id+"F1.wireOp",EDGE,"E2080"),sQuery(id+"F1.wireOp",EDGE,"E2081"),sQuery(id+"F1.wireOp",EDGE,"E2082"),sQuery(id+"F1.wireOp",EDGE,"E2083"),sQuery(id+"F1.wireOp",EDGE,"E2084.trimOffspring"),sQuery(id+"F1.wireOp",EDGE,"E2085.trimOffspring"),sQuery(id+"F1.wireOp",EDGE,"E2086"),sQuery(id+"F1.wireOp",EDGE,"E2087"),sQuery(id+"F1.wireOp",EDGE,"E2088.trimOffspring"),sQuery(id+"F1.wireOp",EDGE,"E2089.trimOffspring"),sQuery(id+"F1.wireOp",EDGE,"E2090.trimOffspring"),sQuery(id+"F1.wireOp",EDGE,"E2091.trimOffspring"),sQuery(id+"F1.wireOp",EDGE,"E2092.trimOffspring"),sQuery(id+"F1.wireOp",EDGE,"E2093.trimOffspring"),sQuery(id+"F1.wireOp",EDGE,"E2094"),sQuery(id+"F1.wireOp",EDGE,"E2095"),sQuery(id+"F1.wireOp",EDGE,"E2096.trimOffspring"),sQuery(id+"F1.wireOp",EDGE,"E2097.trimOffspring"),sQuery(id+"F1.wireOp",EDGE,"E2098"),sQuery(id+"F1.wireOp",EDGE,"E2099"),sQuery(id+"F1.wireOp",EDGE,"E2100.trimOffspring"),sQuery(id+"F1.wireOp",EDGE,"E2101.trimOffspring"),sQuery(id+"F1.wireOp",EDGE,"E2102"),sQuery(id+"F1.wireOp",EDGE,"E2103"),sQuery(id+"F1.wireOp",EDGE,"E2104.trimOffspring"),sQuery(id+"F1.wireOp",EDGE,"E2105.trimOffspring")])],"isStart":false});
            var sketch = newSketch(context, id + "F6", { "sketchPlane" : qUnion([Q0])});
            skPoint(sketch, "E2120.0", {"position": v(8768.61, 24520.52) * mm});
            skLineSegment(sketch, "E2121", {"start": v(8768.61, 24520.52) * mm, "end": v(7720.51, 24203.28) * mm});
            skLineSegment(sketch, "E2122", {"start": v(5896.87, 25740.92) * mm, "end": v(4320.56, 30948.85) * mm});
            skLineSegment(sketch, "E2123", {"start": v(4320.56, 30948.85) * mm, "end": v(1531.95, 30104.8) * mm});
            skLineSegment(sketch, "E2124", {"start": v(1531.95, 30104.8) * mm, "end": v(1060.45, 31662.56) * mm});
            skLineSegment(sketch, "E2125", {"start": v(5896.87, 25740.92) * mm, "end": v(7141.12, 26117.52) * mm});
            skLineSegment(sketch, "E2126", {"start": v(7141.12, 26117.52) * mm, "end": v(7720.51, 24203.28) * mm});
            skSolve(sketch);
        }
        {
            var Q0;
            Q0 = qSketchRegion(id + "F5", true);
            var Q1;
            Q1 = qConstructionFilter(qBodyType(qCreatedBy(id + "F6" ,EDGE), BodyType.WIRE), ConstructionObject.NO);
            sweep(context, id + "F7", {"profiles" : qUnion([Q0]), "path" : qUnion([Q1])});
        }
        {
            var Q0;
            Q0=makeQuery(id+"F2.opExtrude","CAP_FACE",FACE,{"disambiguationData":[OSD([sQuery(id+"F1.wireOp",EDGE,"E2051.0"),sQuery(id+"F1.wireOp",EDGE,"E2051.1"),sQuery(id+"F1.wireOp",EDGE,"E2051.4"),sQuery(id+"F1.wireOp",EDGE,"E2051.5"),sQuery(id+"F1.wireOp",EDGE,"E2051.6"),sQuery(id+"F1.wireOp",EDGE,"E2051.9"),sQuery(id+"F1.wireOp",EDGE,"E2051.10"),sQuery(id+"F1.wireOp",EDGE,"E2051.11"),sQuery(id+"F1.wireOp",EDGE,"E2051.13"),sQuery(id+"F1.wireOp",EDGE,"E2051.14"),sQuery(id+"F1.wireOp",EDGE,"E2051.16"),sQuery(id+"F1.wireOp",EDGE,"E2051.24"),sQuery(id+"F1.wireOp",EDGE,"E2051.25"),sQuery(id+"F1.wireOp",EDGE,"E2051.27"),sQuery(id+"F1.wireOp",EDGE,"E2051.29"),sQuery(id+"F1.wireOp",EDGE,"E2051.31"),sQuery(id+"F1.wireOp",EDGE,"E2051.32"),sQuery(id+"F1.wireOp",EDGE,"E2051.33"),sQuery(id+"F1.wireOp",EDGE,"E2051.34"),sQuery(id+"F1.wireOp",EDGE,"E2051.35"),sQuery(id+"F1.wireOp",EDGE,"E2051.36"),sQuery(id+"F1.wireOp",EDGE,"E2051.37"),sQuery(id+"F1.wireOp",EDGE,"E2051.41"),sQuery(id+"F1.wireOp",EDGE,"E2051.42"),sQuery(id+"F1.wireOp",EDGE,"E2051.43"),sQuery(id+"F1.wireOp",EDGE,"E2051.45"),sQuery(id+"F1.wireOp",EDGE,"E2051.46"),sQuery(id+"F1.wireOp",EDGE,"E2051.47"),sQuery(id+"F1.wireOp",EDGE,"E2051.48"),sQuery(id+"F1.wireOp",EDGE,"E2051.49"),sQuery(id+"F1.wireOp",EDGE,"E2051.50"),sQuery(id+"F1.wireOp",EDGE,"E2051.51"),sQuery(id+"F1.wireOp",EDGE,"E2051.52"),sQuery(id+"F1.wireOp",EDGE,"E2051.53"),sQuery(id+"F1.wireOp",EDGE,"E2051.54"),sQuery(id+"F1.wireOp",EDGE,"E2051.55"),sQuery(id+"F1.wireOp",EDGE,"E2051.56"),sQuery(id+"F1.wireOp",EDGE,"E2051.57"),sQuery(id+"F1.wireOp",EDGE,"E2051.58"),sQuery(id+"F1.wireOp",EDGE,"E2051.59"),sQuery(id+"F1.wireOp",EDGE,"E2051.60"),sQuery(id+"F1.wireOp",EDGE,"E2051.61"),sQuery(id+"F1.wireOp",EDGE,"E2051.63"),sQuery(id+"F1.wireOp",EDGE,"E2051.66"),sQuery(id+"F1.wireOp",EDGE,"E2051.67"),sQuery(id+"F1.wireOp",EDGE,"E2051.68"),sQuery(id+"F1.wireOp",EDGE,"E2051.69"),sQuery(id+"F1.wireOp",EDGE,"E2051.70"),sQuery(id+"F1.wireOp",EDGE,"E2051.72"),sQuery(id+"F1.wireOp",EDGE,"E2051.74"),sQuery(id+"F1.wireOp",EDGE,"E2051.76"),sQuery(id+"F1.wireOp",EDGE,"E2052.1"),sQuery(id+"F1.wireOp",EDGE,"E2053"),sQuery(id+"F1.wireOp",EDGE,"E2054"),sQuery(id+"F1.wireOp",EDGE,"E2055"),sQuery(id+"F1.wireOp",EDGE,"E2056"),sQuery(id+"F1.wireOp",EDGE,"E2057"),sQuery(id+"F1.wireOp",EDGE,"E2058"),sQuery(id+"F1.wireOp",EDGE,"E2059"),sQuery(id+"F1.wireOp",EDGE,"E2060"),sQuery(id+"F1.wireOp",EDGE,"E2061"),sQuery(id+"F1.wireOp",EDGE,"E2062"),sQuery(id+"F1.wireOp",EDGE,"E2063"),sQuery(id+"F1.wireOp",EDGE,"E2064"),sQuery(id+"F1.wireOp",EDGE,"E2065"),sQuery(id+"F1.wireOp",EDGE,"E2066"),sQuery(id+"F1.wireOp",EDGE,"E2067"),sQuery(id+"F1.wireOp",EDGE,"E2068"),sQuery(id+"F1.wireOp",EDGE,"E2069"),sQuery(id+"F1.wireOp",EDGE,"E2070"),sQuery(id+"F1.wireOp",EDGE,"E2071"),sQuery(id+"F1.wireOp",EDGE,"E2072"),sQuery(id+"F1.wireOp",EDGE,"E2073"),sQuery(id+"F1.wireOp",EDGE,"E2074"),sQuery(id+"F1.wireOp",EDGE,"E2075"),sQuery(id+"F1.wireOp",EDGE,"E2076"),sQuery(id+"F1.wireOp",EDGE,"E2077"),sQuery(id+"F1.wireOp",EDGE,"E2078"),sQuery(id+"F1.wireOp",EDGE,"E2079"),sQuery(id+"F1.wireOp",EDGE,"E2080"),sQuery(id+"F1.wireOp",EDGE,"E2081"),sQuery(id+"F1.wireOp",EDGE,"E2082"),sQuery(id+"F1.wireOp",EDGE,"E2083"),sQuery(id+"F1.wireOp",EDGE,"E2084.trimOffspring"),sQuery(id+"F1.wireOp",EDGE,"E2085.trimOffspring"),sQuery(id+"F1.wireOp",EDGE,"E2086"),sQuery(id+"F1.wireOp",EDGE,"E2087"),sQuery(id+"F1.wireOp",EDGE,"E2088.trimOffspring"),sQuery(id+"F1.wireOp",EDGE,"E2089.trimOffspring"),sQuery(id+"F1.wireOp",EDGE,"E2090.trimOffspring"),sQuery(id+"F1.wireOp",EDGE,"E2091.trimOffspring"),sQuery(id+"F1.wireOp",EDGE,"E2092.trimOffspring"),sQuery(id+"F1.wireOp",EDGE,"E2093.trimOffspring"),sQuery(id+"F1.wireOp",EDGE,"E2094"),sQuery(id+"F1.wireOp",EDGE,"E2095"),sQuery(id+"F1.wireOp",EDGE,"E2096.trimOffspring"),sQuery(id+"F1.wireOp",EDGE,"E2097.trimOffspring"),sQuery(id+"F1.wireOp",EDGE,"E2098"),sQuery(id+"F1.wireOp",EDGE,"E2099"),sQuery(id+"F1.wireOp",EDGE,"E2100.trimOffspring"),sQuery(id+"F1.wireOp",EDGE,"E2101.trimOffspring"),sQuery(id+"F1.wireOp",EDGE,"E2102"),sQuery(id+"F1.wireOp",EDGE,"E2103"),sQuery(id+"F1.wireOp",EDGE,"E2104.trimOffspring"),sQuery(id+"F1.wireOp",EDGE,"E2105.trimOffspring")])],"isStart":false});
            var sketch = newSketch(context, id + "F8", { "sketchPlane" : qUnion([Q0])});
            skLineSegment(sketch, "E2127.0", {"start": v(8275.24, 25028.58) * mm, "end": v(7643.52, 24837.37) * mm, "construction": true});
            skLineSegment(sketch, "E2128", {"start": v(6747.46, 25036.31) * mm, "end": v(6221.05, 24876.98) * mm});
            skLineSegment(sketch, "E2129", {"start": v(6221.05, 24876.98) * mm, "end": v(6467.3, 24063.43) * mm});
            skLineSegment(sketch, "E2130", {"start": v(6467.3, 24063.43) * mm, "end": v(6993.7, 24222.76) * mm});
            skLineSegment(sketch, "E2131", {"start": v(6993.7, 24222.76) * mm, "end": v(6747.46, 25036.31) * mm});
            skSolve(sketch);
        }
        {
            var Q0;
            Q0 = qSketchRegion(id + "F8", true);
            extrude(context, id + "F9", {"entities" : qUnion([Q0]), "oppositeDirection" : true, "depth" : 270 * mm, "offsetDistance" : 25 * mm});
        }
        {
            var Q0;
            Q0=makeQuery(id+"F6.imprint","IMPRINT",FACE,{"disambiguationData":[TD([[makeQuery(id+"F6.imprint","IMPRINT",EDGE,{"derivedFrom":makeQuery(id+"F2.opExtrude","CAP_EDGE",EDGE,{"disambiguationData":[OSD([sQuery(id+"F1.wireOp",EDGE,"E2051.0")])],"isStart":false})}),1.0]])]});
            var sketch = newSketch(context, id + "F10", { "sketchPlane" : qUnion([Q0])});
            skLineSegment(sketch, "E2132.0", {"start": v(7345.9, 28098.92) * mm, "end": v(6714.19, 27907.71) * mm, "construction": true});
            skLineSegment(sketch, "E2133", {"start": v(6765.73, 27599.43) * mm, "end": v(6239.31, 27440.1) * mm});
            skLineSegment(sketch, "E2134", {"start": v(6239.31, 27440.1) * mm, "end": v(6485.56, 26626.54) * mm});
            skLineSegment(sketch, "E2135", {"start": v(6485.56, 26626.54) * mm, "end": v(7011.97, 26785.88) * mm});
            skLineSegment(sketch, "E2136", {"start": v(7011.97, 26785.88) * mm, "end": v(6765.73, 27599.43) * mm});
            skSolve(sketch);
        }
        {
            var Q0;
            Q0 = qSketchRegion(id + "F10", true);
            extrude(context, id + "F11", {"entities" : qUnion([Q0]), "oppositeDirection" : true, "depth" : 270 * mm, "offsetDistance" : 25 * mm});
        }
    });
